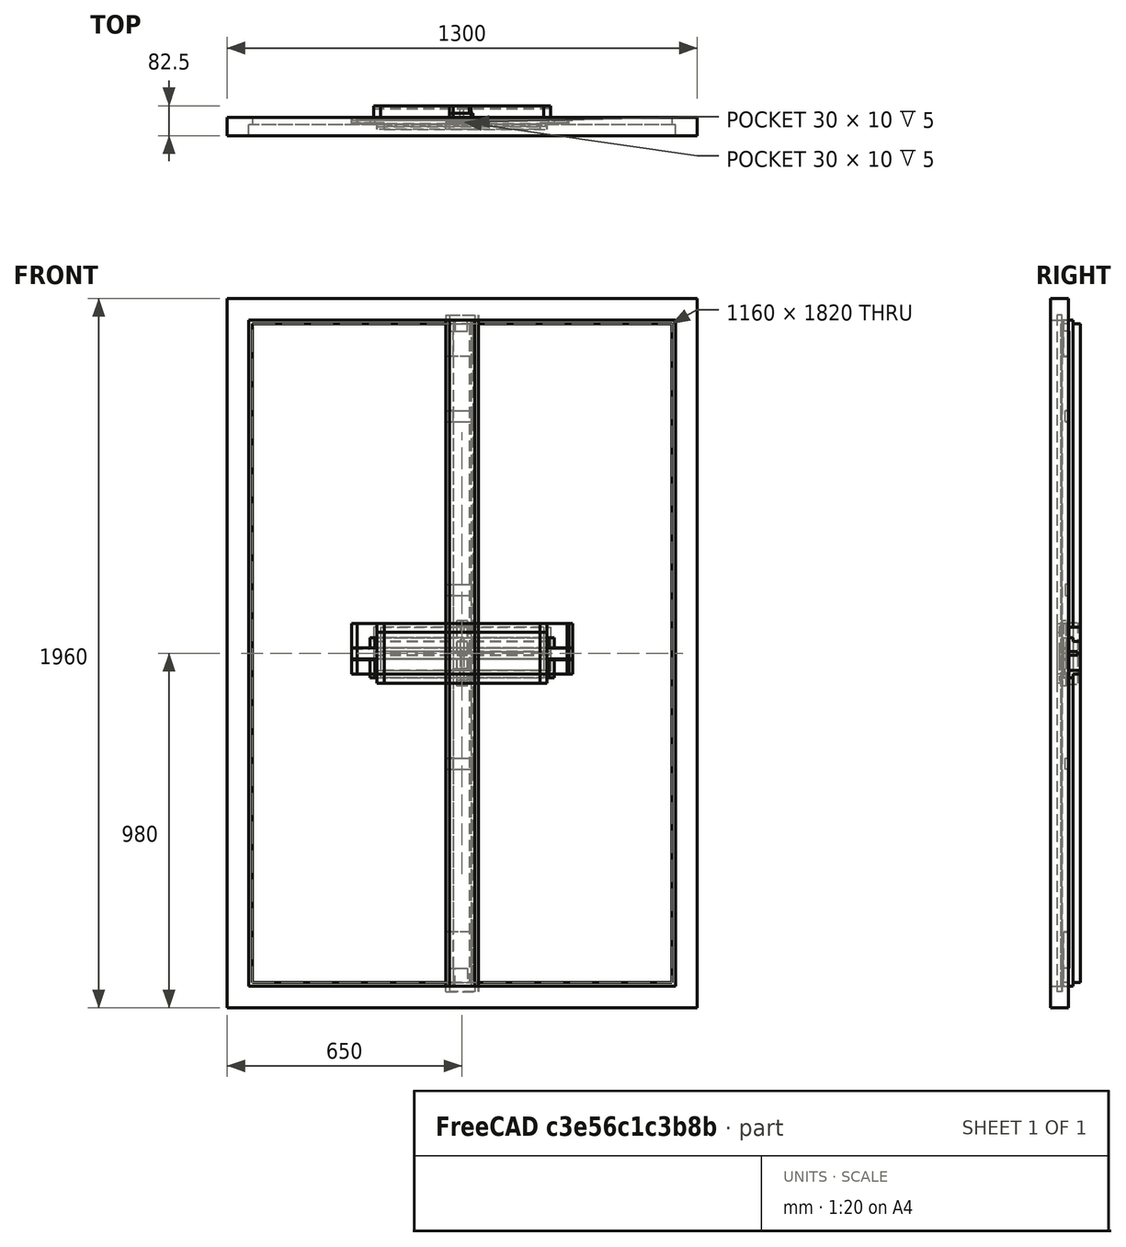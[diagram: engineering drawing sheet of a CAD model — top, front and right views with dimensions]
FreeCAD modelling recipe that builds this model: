
FCSTD DOCUMENT  (FreeCAD 1.1R38898 (Git))
Label: F4.0
License: All rights reserved
LicenseURL: https://en.wikipedia.org/wiki/All_rights_reserved
objects: Sketcher::SketchObject×54, PartDesign::Pocket×45, PartDesign::Plane×39, App::Link×27, App::FeaturePython×27, PartDesign::Body×14, PartDesign::Pad×7, PartDesign::FeatureBase×7, PartDesign::SubShapeBinder×6, Part::Mirroring×6, App::DocumentObjectGroup×6, PartDesign::Mirrored×5, App::VarSet×1, Assembly::JointGroup×1, Assembly::AssemblyObject×1
note: 353 computed .brp shape members not serialized (recipe doc carries the construction recipe); baked Part::Feature solids carry a one-line shape summary decoded from their .brp
EXTERNAL_REF file=F4.2.FCStd obj=Assembly
EXTERNAL_REF file=F4.1.FCStd obj=Assembly

FEATURE [App::VarSet] VarSet  label="Parameters"
  FrameThickness = 50
  GlassFullLength = 470
  GlassFullWidth = 470
  GlassLength = 470
  GlassOpeningHeigth = 450
  GlassOpeningWidth = 450
  GlassRebateDepth = 32
  GlassRebateWidth = 10
  GlassThickness = 24
  GlassThirdLength = 230
  GlassThirdWidth = 170
  GlassWidth = 470
  IntersectionRebateDepth = 10
  IntersectionRebateWidth = 32.5
  MuntinBarLength = 180
  MuntinBarTenonLength = 15
  MuntinTenonThickness = 10
  MuntinThickness = 50
  MuntinWidth = 30
  RailBottomTenonWidth = 100
  RailBottomWidth = 165
  RailLength = 610
  RailTenonThickness = 15
  RailTopTenonWidth = 70
  RailTopWidth = 115
  StileInnerHaunchDepth = 20
  StileInnerWidth = 70
  StileLength = 1870
  StileOuterHaunchDepth = 25
  StileOuterWidth = 90
  WindowFrameRebateDepth = 25
  WindowFrameRebateWidth = 20
  WindowInnerLipWidth = 15
  WindowThickness = 65
  expr: GlassFullLength = GlassOpeningHeigth + 2 * GlassRebateWidth
  expr: GlassFullWidth = GlassOpeningWidth + 2 * GlassRebateWidth
  expr: IntersectionRebateWidth = WindowThickness / 2
FEATURE [PartDesign::Plane] DatumPlane  label="DatumPlane top"
  AttachmentOffset = pos=(0,0,90) rot=(0,0,1;0rad)
  AttachmentSupport = -> [X_Axis]
  Length = 30
  MapMode = 2
  Placement = pos=(0,0,90) rot=(0,0,1;0rad)
  ResizeMode = 1
  Width = 50
  expr: .AttachmentOffset.Base.z = <<Parameters>>.MuntinBarLength / 2
  expr: Length = <<Parameters>>.MuntinWidth
  expr: Width = <<Parameters>>.MuntinThickness
FEATURE [PartDesign::Plane] DatumPlane001  label="DatumPlane right"
  AttachmentOffset = pos=(0,0,15) rot=(0,0,1;0rad)
  AttachmentSupport = -> [X_Axis]
  Length = 50
  MapMode = 4
  Placement = pos=(15,0,0) rot=(0.57735,0.57735,0.57735;2.0944rad)
  ResizeMode = 1
  Width = 180
  expr: .AttachmentOffset.Base.z = <<Parameters>>.MuntinWidth / 2
  expr: Length = <<Parameters>>.MuntinThickness
  expr: Width = <<Parameters>>.MuntinBarLength
FEATURE [PartDesign::Plane] DatumPlane002  label="DatumPlane front"
  AttachmentOffset = pos=(0,0,25) rot=(0,0,1;0rad)
  AttachmentSupport = -> [X_Axis]
  Length = 30
  MapMode = 3
  Placement = pos=(0,-25,5.6e-15) rot=(1,0,0;1.5708rad)
  ResizeMode = 1
  Width = 180
  expr: .AttachmentOffset.Base.z = <<Parameters>>.MuntinThickness / 2
  expr: Length = <<Parameters>>.MuntinWidth
  expr: Width = <<Parameters>>.MuntinBarLength
FEATURE [Sketcher::SketchObject] Sketch
  ArcFitTolerance = 0
  AttachmentSupport = -> [DatumPlane]
  FullyConstrained = true
  MakeInternals = false
  MapMode = 5
  Placement = pos=(0,0,90) rot=(0,0,1;0rad)
  expr: Constraints[10] = <<Parameters>>.MuntinWidth
  expr: Constraints[11] = <<Parameters>>.MuntinThickness
  sketch-geometry (5):
    g0: LineSegment StartX=-15 StartY=25 StartZ=0 EndX=-15 EndY=-25 EndZ=0
    g1: LineSegment StartX=-15 StartY=-25 StartZ=0 EndX=15 EndY=-25 EndZ=0
    g2: LineSegment StartX=15 StartY=-25 StartZ=0 EndX=15 EndY=25 EndZ=0
    g3: LineSegment StartX=15 StartY=25 StartZ=0 EndX=-15 EndY=25 EndZ=0
    g4: GeomPoint [constr] X=0 Y=0 Z=0
  constraints (12):
    c: Coincident(g0,g1)
    c: Coincident(g1,g2)
    c: Coincident(g2,g3)
    c: Coincident(g3,g0)
    c: Vertical(g0)
    c: Vertical(g2)
    c: Horizontal(g1)
    c: Horizontal(g3)
    c: Symmetric(g2,g0,g4)
    c: Coincident(g4,g-1)
    c: DistanceX(g3,g3) = 30
    c: DistanceY(g0,g0) = 50
FEATURE [PartDesign::Pad] Pad  label="Stock"
  Direction = (0,0,1)
  Length = 180
  Length2 = 10
  Placement = pos=(0,0,90) rot=(0,0,1;0rad)
  Profile = -> Sketch
  ReferenceAxis = -> Sketch [N_Axis]
  Refine = true
  Reversed = true
  Suppressed = false
  Type = 0
  expr: Length = <<Parameters>>.MuntinBarLength
FEATURE [Sketcher::SketchObject] Sketch001
  ArcFitTolerance = 0
  AttachmentSupport = -> [DatumPlane001]
  ExternalGeometry = -> [DatumPlane,DatumPlane002]
  FullyConstrained = true
  MakeInternals = false
  MapMode = 5
  Placement = pos=(15,0,0) rot=(0.57735,0.57735,0.57735;2.0944rad)
  expr: Constraints[14] = <<Parameters>>.MuntinBarTenonLength
  expr: Constraints[16] = <<Parameters>>.GlassRebateDepth
  expr: Constraints[18] = <<Parameters>>.MuntinThickness
  expr: Constraints[19] = <<Parameters>>.MuntinTenonThickness
  expr: Constraints[20] = <<Parameters>>.MuntinBarTenonLength - <<Parameters>>.GlassRebateWidth
  sketch-geometry (8):
    g0: LineSegment StartX=-17 StartY=90 StartZ=0 EndX=-17 EndY=75 EndZ=0
    g1: LineSegment StartX=-17 StartY=75 StartZ=0 EndX=-25 EndY=75 EndZ=0
    g2: LineSegment StartX=-25 StartY=75 StartZ=0 EndX=-25 EndY=90 EndZ=0
    g3: LineSegment StartX=-25 StartY=90 StartZ=0 EndX=-17 EndY=90 EndZ=0
    g4: LineSegment StartX=-7 StartY=90 StartZ=0 EndX=-7 EndY=85 EndZ=0
    g5: LineSegment StartX=-7 StartY=85 StartZ=0 EndX=25 EndY=85 EndZ=0
    g6: LineSegment StartX=25 StartY=85 StartZ=0 EndX=25 EndY=90 EndZ=0
    g7: LineSegment StartX=25 StartY=90 StartZ=0 EndX=-7 EndY=90 EndZ=0
  constraints (23):
    c: Coincident(g0,g1)
    c: Coincident(g1,g2)
    c: Coincident(g2,g3)
    c: Coincident(g3,g0)
    c: Vertical(g0)
    c: Horizontal(g1)
    c: Coincident(g4,g5)
    c: Coincident(g5,g6)
    c: Coincident(g6,g7)
    c: Coincident(g7,g4)
    c: Vertical(g4)
    c: Vertical(g6)
    c: Horizontal(g5)
    c: Horizontal(g7)
    c: DistanceY(g0,g0) = 15
    c: DistanceX(g1,g1) = -8
    c: DistanceX(g7,g7) = 32
    c: Horizontal(g4,g2)
    c: DistanceX(g2,g6) = 50
    c: DistanceX(g0,g4) = 10
    c: DistanceY(g6,g6) = 5
    c: Tangent(g2,g-4)
    c: Tangent(g3,g-3)
FEATURE [PartDesign::Pocket] Pocket  label="Tenon top"
  BaseFeature = -> Pad
  Direction = (-1,0,0)
  Length = 5
  Length2 = 5
  Placement = pos=(0,0,90) rot=(0,0,1;0rad)
  Profile = -> Sketch001
  ReferenceAxis = -> Sketch001 [N_Axis]
  Refine = true
  Suppressed = false
  Type = 1
FEATURE [PartDesign::Mirrored] Mirrored  label="Tenon bottom"
  BaseFeature = -> Pocket
  MirrorPlane = -> XY_Plane
  Originals = -> [Pocket]
  Placement = pos=(0,0,90) rot=(0,0,1;0rad)
  Refine = true
  Suppressed = false
  TransformMode = 0
FEATURE [Sketcher::SketchObject] Sketch002
  ArcFitTolerance = 0
  AttachmentSupport = -> [DatumPlane]
  ExternalGeometry = -> [DatumPlane001,DatumPlane002]
  FullyConstrained = true
  MakeInternals = false
  MapMode = 5
  Placement = pos=(0,0,90) rot=(0,0,1;0rad)
  expr: Constraints[7] = <<Parameters>>.GlassRebateDepth
  expr: Constraints[8] = <<Parameters>>.GlassRebateWidth
  expr: Constraints[9] = <<Parameters>>.MuntinThickness
  sketch-geometry (4):
    g0: LineSegment StartX=5 StartY=25 StartZ=0 EndX=5 EndY=-7 EndZ=0
    g1: LineSegment StartX=5 StartY=-7 StartZ=0 EndX=15 EndY=-7 EndZ=0
    g2: LineSegment StartX=15 StartY=-7 StartZ=0 EndX=15 EndY=25 EndZ=0
    g3: LineSegment StartX=15 StartY=25 StartZ=0 EndX=5 EndY=25 EndZ=0
  constraints (11):
    c: Coincident(g0,g1)
    c: Coincident(g1,g2)
    c: Coincident(g2,g3)
    c: Coincident(g3,g0)
    c: Vertical(g0)
    c: Horizontal(g1)
    c: Horizontal(g3)
    c: DistanceY(g0,g0) = 32
    c: DistanceX(g3,g3) = 10
    c: Distance(g2,g-4) = 50
    c: Tangent(g2,g-3)
FEATURE [PartDesign::Pocket] Pocket001  label="Glass rebate right"
  BaseFeature = -> Mirrored
  Direction = (0,0,-1)
  Length = 5
  Length2 = 5
  Placement = pos=(0,0,90) rot=(0,0,1;0rad)
  Profile = -> Sketch002
  ReferenceAxis = -> Sketch002 [N_Axis]
  Refine = true
  Suppressed = false
  Type = 1
FEATURE [PartDesign::Mirrored] Mirrored001  label="Glass rebate left"
  BaseFeature = -> Pocket001
  MirrorPlane = -> Sketch002 [V_Axis]
  Originals = -> [Pocket001]
  Placement = pos=(0,0,90) rot=(0,0,1;0rad)
  Refine = true
  Suppressed = false
  TransformMode = 0
FEATURE [PartDesign::Body] Body  label="Muntin bar"
  AllowCompound = false
  Group = -> [DatumPlane,DatumPlane001,DatumPlane002,Sketch,Pad,Sketch001,Pocket,Mirrored,Sketch002,Pocket001,Mirrored001]
  Origin = -> Origin
  Tip = -> Mirrored001
FEATURE [PartDesign::Plane] DatumPlane003  label="DatumPlane top001"
  AttachmentOffset = pos=(0,0,935) rot=(0,0,1;0rad)
  AttachmentSupport = -> [X_Axis001]
  Length = 90
  MapMode = 2
  Placement = pos=(0,0,935) rot=(0,0,1;0rad)
  ResizeMode = 1
  Width = 65
  expr: .AttachmentOffset.Base.z = <<Parameters>>.StileLength / 2
  expr: Length = <<Parameters>>.StileOuterWidth
  expr: Width = <<Parameters>>.WindowThickness
FEATURE [PartDesign::Plane] DatumPlane004  label="DatumPlane right001"
  AttachmentOffset = pos=(0,0,45) rot=(0,0,1;0rad)
  AttachmentSupport = -> [X_Axis001]
  Length = 65
  MapMode = 4
  Placement = pos=(45,0,0) rot=(0.57735,0.57735,0.57735;2.0944rad)
  ResizeMode = 1
  Width = 1870
  expr: .AttachmentOffset.Base.z = <<Parameters>>.StileOuterWidth / 2
  expr: Length = <<Parameters>>.WindowThickness
  expr: Width = <<Parameters>>.StileLength
FEATURE [PartDesign::Plane] DatumPlane005  label="DatumPlane rear"
  AttachmentOffset = pos=(0,0,32.5) rot=(0,0,1;0rad)
  AttachmentSupport = -> [X_Axis001]
  Length = 90
  MapMode = 3
  Placement = pos=(0,32.5,-7.2e-15) rot=(0,0.707107,0.707107;3.14159rad)
  ResizeMode = 1
  Width = 1870
  expr: .AttachmentOffset.Base.z = <<Parameters>>.WindowThickness / 2
  expr: Length = <<Parameters>>.StileOuterWidth
  expr: Width = <<Parameters>>.StileLength
FEATURE [Sketcher::SketchObject] Sketch003
  ArcFitTolerance = 0
  AttachmentSupport = -> [DatumPlane003]
  FullyConstrained = true
  MakeInternals = false
  MapMode = 5
  Placement = pos=(0,0,935) rot=(0,0,1;0rad)
  expr: Constraints[10] = <<Parameters>>.StileOuterWidth
  expr: Constraints[11] = <<Parameters>>.WindowThickness
  sketch-geometry (5):
    g0: LineSegment StartX=-45 StartY=32.5 StartZ=0 EndX=-45 EndY=-32.5 EndZ=0
    g1: LineSegment StartX=-45 StartY=-32.5 StartZ=0 EndX=45 EndY=-32.5 EndZ=0
    g2: LineSegment StartX=45 StartY=-32.5 StartZ=0 EndX=45 EndY=32.5 EndZ=0
    g3: LineSegment StartX=45 StartY=32.5 StartZ=0 EndX=-45 EndY=32.5 EndZ=0
    g4: GeomPoint [constr] X=0 Y=0 Z=0
  constraints (12):
    c: Coincident(g0,g1)
    c: Coincident(g1,g2)
    c: Coincident(g2,g3)
    c: Coincident(g3,g0)
    c: Vertical(g0)
    c: Vertical(g2)
    c: Horizontal(g1)
    c: Horizontal(g3)
    c: Symmetric(g2,g0,g4)
    c: Coincident(g4,g-1)
    c: DistanceX(g3,g3) = 90
    c: DistanceY(g0,g0) = 65
FEATURE [PartDesign::Pad] Pad001  label="Stock001"
  Direction = (0,0,1)
  Length = 1870
  Length2 = 10
  Placement = pos=(0,0,935) rot=(0,0,1;0rad)
  Profile = -> Sketch003
  ReferenceAxis = -> Sketch003 [N_Axis]
  Refine = true
  Reversed = true
  Suppressed = false
  Type = 0
  expr: Length = <<Parameters>>.StileLength
FEATURE [PartDesign::Plane] DatumPlane006  label="DatumPlane bottom"
  AttachmentOffset = pos=(0,0,935) rot=(0,0,1;0rad)
  AttachmentSupport = -> [X_Axis001]
  Length = 90
  MapMode = 2
  Placement = pos=(0,0,-935) rot=(0,1,0;3.14159rad)
  ResizeMode = 1
  Width = 65
  expr: .AttachmentOffset.Base.z = <<Parameters>>.StileLength / 2
  expr: Length = <<Parameters>>.StileOuterWidth
  expr: Width = <<Parameters>>.WindowThickness
FEATURE [Sketcher::SketchObject] Sketch006
  ArcFitTolerance = 0
  AttachmentSupport = -> [DatumPlane004]
  ExternalGeometry = -> [DatumPlane005,DatumPlane006]
  FullyConstrained = true
  MakeInternals = false
  MapMode = 5
  Placement = pos=(45,0,0) rot=(0.57735,0.57735,0.57735;2.0944rad)
  expr: Constraints[30] = <<Parameters>>.GlassOpeningHeigth
  expr: Constraints[31] = <<Parameters>>.MuntinTenonThickness
  expr: Constraints[32] = <<Parameters>>.GlassRebateDepth
  expr: Constraints[34] = <<Parameters>>.GlassOpeningHeigth + <<Parameters>>.RailBottomWidth
  expr: Constraints[35] = <<Parameters>>.GlassOpeningHeigth
  expr: Constraints[8] = <<Parameters>>.MuntinWidth
  sketch-geometry (12):
    g0: LineSegment StartX=-9.5 StartY=-290 StartZ=0 EndX=-9.5 EndY=-320 EndZ=0
    g1: LineSegment StartX=-9.5 StartY=-320 StartZ=0 EndX=0.5 EndY=-320 EndZ=0
    g2: LineSegment StartX=0.5 StartY=-320 StartZ=0 EndX=0.5 EndY=-290 EndZ=0
    g3: LineSegment StartX=0.5 StartY=-290 StartZ=0 EndX=-9.5 EndY=-290 EndZ=0
    g4: LineSegment StartX=-9.5 StartY=160 StartZ=0 EndX=-9.5 EndY=190 EndZ=0
    g5: LineSegment StartX=-9.5 StartY=190 StartZ=0 EndX=0.5 EndY=190 EndZ=0
    g6: LineSegment StartX=0.5 StartY=190 StartZ=0 EndX=0.5 EndY=160 EndZ=0
    g7: LineSegment StartX=0.5 StartY=160 StartZ=0 EndX=-9.5 EndY=160 EndZ=0
    g8: LineSegment StartX=-9.5 StartY=640 StartZ=0 EndX=-9.5 EndY=670 EndZ=0
    g9: LineSegment StartX=-9.5 StartY=670 StartZ=0 EndX=0.5 EndY=670 EndZ=0
    g10: LineSegment StartX=0.5 StartY=670 StartZ=0 EndX=0.5 EndY=640 EndZ=0
    g11: LineSegment StartX=0.5 StartY=640 StartZ=0 EndX=-9.5 EndY=640 EndZ=0
  constraints (36):
    c: Coincident(g0,g1)
    c: Coincident(g1,g2)
    c: Coincident(g2,g3)
    c: Coincident(g3,g0)
    c: Vertical(g0)
    c: Vertical(g2)
    c: Horizontal(g1)
    c: Horizontal(g3)
    c: DistanceY(g0,g0) = 30
    c: Coincident(g4,g5)
    c: Coincident(g8,g9)
    c: Coincident(g5,g6)
    c: Coincident(g9,g10)
    c: Coincident(g6,g7)
    c: Coincident(g10,g11)
    c: Coincident(g7,g4)
    c: Coincident(g11,g8)
    c: Vertical(g4)
    c: Vertical(g8)
    c: Vertical(g6)
    c: Vertical(g10)
    c: Horizontal(g5)
    c: Horizontal(g9)
    c: Horizontal(g7)
    c: Horizontal(g11)
    c: Equal(g0,g4)
    c: Equal(g0,g8)
    c: Equal(g11,g7)
    c: Equal(g7,g3)
    c: Vertical(g5,g9)
    c: DistanceY(g0,g4) = 450
    c: DistanceX(g1,g1) = 10
    c: Distance(g1,g-3) = 32
    c: Vertical(g9,g2)
    c: Distance(g0,g-4) = 615
    c: DistanceY(g4,g8) = 450
FEATURE [Sketcher::SketchObject] Sketch007  label="Frame rebate opening top002"
  ArcFitTolerance = 0
  AttachmentSupport = -> [DatumPlane004]
  ExternalGeometry = -> [DatumPlane003,DatumPlane005]
  FullyConstrained = true
  MakeInternals = false
  MapMode = 5
  Placement = pos=(45,0,0) rot=(0.57735,0.57735,0.57735;2.0944rad)
  expr: Constraints[6] = <<Parameters>>.WindowFrameRebateWidth
  expr: Constraints[7] = <<Parameters>>.WindowFrameRebateDepth
  sketch-geometry (4):
    g0: LineSegment StartX=12.5 StartY=935 StartZ=0 EndX=12.5 EndY=910 EndZ=0
    g1: LineSegment StartX=12.5 StartY=910 StartZ=0 EndX=32.5 EndY=910 EndZ=0
    g2: LineSegment StartX=32.5 StartY=910 StartZ=0 EndX=32.5 EndY=935 EndZ=0
    g3: LineSegment StartX=32.5 StartY=935 StartZ=0 EndX=12.5 EndY=935 EndZ=0
  constraints (10):
    c: Coincident(g0,g1)
    c: Coincident(g1,g2)
    c: Coincident(g2,g3)
    c: Coincident(g3,g0)
    c: Vertical(g0)
    c: Horizontal(g1)
    c: DistanceX(g3,g3) = 20
    c: Distance(g2,g2) = 25
    c: Tangent(g2,g-4)
    c: Tangent(g3,g-3)
FEATURE [Sketcher::SketchObject] Sketch008  label="Frame rebate closure top002"
  ArcFitTolerance = 0
  AttachmentSupport = -> [DatumPlane004]
  ExternalGeometry = -> [DatumPlane003,DatumPlane005]
  FullyConstrained = true
  MakeInternals = false
  MapMode = 5
  Placement = pos=(45,0,0) rot=(0.57735,0.57735,0.57735;2.0944rad)
  expr: Constraints[6] = <<Parameters>>.WindowInnerLipWidth
  expr: Constraints[7] = <<Parameters>>.FrameThickness
  sketch-geometry (4):
    g0: LineSegment StartX=-17.5 StartY=935 StartZ=0 EndX=-17.5 EndY=920 EndZ=0
    g1: LineSegment StartX=-17.5 StartY=920 StartZ=0 EndX=32.5 EndY=920 EndZ=0
    g2: LineSegment StartX=32.5 StartY=920 StartZ=0 EndX=32.5 EndY=935 EndZ=0
    g3: LineSegment StartX=32.5 StartY=935 StartZ=0 EndX=-17.5 EndY=935 EndZ=0
  constraints (10):
    c: Coincident(g0,g1)
    c: Coincident(g1,g2)
    c: Coincident(g2,g3)
    c: Coincident(g3,g0)
    c: Vertical(g0)
    c: Horizontal(g1)
    c: DistanceY(g2,g2) = 15
    c: DistanceX(g3,g3) = 50
    c: Tangent(g3,g-3)
    c: Tangent(g-4,g2)
FEATURE [PartDesign::Plane] DatumPlane007  label="DatumPlane left"
  AttachmentOffset = pos=(0,0,45) rot=(0,0,1;0rad)
  AttachmentSupport = -> [X_Axis001]
  Length = 65
  MapMode = 4
  Placement = pos=(-45,0,0) rot=(0.57735,-0.57735,-0.57735;2.0944rad)
  ResizeMode = 1
  Width = 1870
  expr: .AttachmentOffset.Base.z = <<Parameters>>.StileOuterWidth / 2
  expr: Length = <<Parameters>>.WindowThickness
  expr: Width = <<Parameters>>.StileLength
FEATURE [Sketcher::SketchObject] Sketch009  label="Frame rebate opening side002"
  ArcFitTolerance = 0
  AttachmentSupport = -> [DatumPlane003]
  ExternalGeometry = -> [DatumPlane005,DatumPlane007]
  FullyConstrained = true
  MakeInternals = false
  MapMode = 5
  Placement = pos=(0,0,935) rot=(0,0,1;0rad)
  expr: Constraints[6] = <<Parameters>>.WindowFrameRebateDepth
  expr: Constraints[7] = <<Parameters>>.WindowFrameRebateWidth
  sketch-geometry (4):
    g0: LineSegment StartX=-45 StartY=32.5 StartZ=0 EndX=-45 EndY=12.5 EndZ=0
    g1: LineSegment StartX=-45 StartY=12.5 StartZ=0 EndX=-20 EndY=12.5 EndZ=0
    g2: LineSegment StartX=-20 StartY=12.5 StartZ=0 EndX=-20 EndY=32.5 EndZ=0
    g3: LineSegment StartX=-20 StartY=32.5 StartZ=0 EndX=-45 EndY=32.5 EndZ=0
  constraints (10):
    c: Coincident(g0,g1)
    c: Coincident(g1,g2)
    c: Coincident(g2,g3)
    c: Coincident(g3,g0)
    c: Vertical(g2)
    c: Horizontal(g1)
    c: DistanceX(g3,g3) = 25
    c: DistanceY(g0,g0) = 20
    c: Tangent(g3,g-3)
    c: Tangent(g0,g-4)
FEATURE [Sketcher::SketchObject] Sketch010  label="Frame rebate closure right002"
  ArcFitTolerance = 0
  AttachmentSupport = -> [DatumPlane003]
  ExternalGeometry = -> [DatumPlane005,DatumPlane007]
  FullyConstrained = true
  MakeInternals = false
  MapMode = 5
  Placement = pos=(0,0,935) rot=(0,0,1;0rad)
  expr: Constraints[6] = <<Parameters>>.WindowInnerLipWidth
  expr: Constraints[7] = <<Parameters>>.FrameThickness
  sketch-geometry (4):
    g0: LineSegment StartX=-45 StartY=32.5 StartZ=0 EndX=-45 EndY=-17.5 EndZ=0
    g1: LineSegment StartX=-45 StartY=-17.5 StartZ=0 EndX=-30 EndY=-17.5 EndZ=0
    g2: LineSegment StartX=-30 StartY=-17.5 StartZ=0 EndX=-30 EndY=32.5 EndZ=0
    g3: LineSegment StartX=-30 StartY=32.5 StartZ=0 EndX=-45 EndY=32.5 EndZ=0
  constraints (10):
    c: Coincident(g0,g1)
    c: Coincident(g1,g2)
    c: Coincident(g2,g3)
    c: Coincident(g3,g0)
    c: Vertical(g2)
    c: Horizontal(g1)
    c: DistanceX(g3,g3) = 15
    c: DistanceY(g0,g0) = 50
    c: Tangent(g3,g-3)
    c: Tangent(g0,g-4)
FEATURE [PartDesign::SubShapeBinder] Binder  label="Stile outer left binder"
  BindCopyOnChange = 0
  BindMode = 0
  ClaimChildren = false
  Context = -> Body001 [Binder.]
  Fuse = false
  MakeFace = true
  OffsetFill = false
  OffsetIntersection = false
  OffsetJoinType = 0
  OffsetOpenResult = false
  PartialLoad = false
  Refine = true
  Relative = true
  Support = -> [Body001[Pocket017.]]
  _Version = 2
FEATURE [Part::Mirroring] Part__Mirroring  label="Stile outer right (Mirror #1)"
  Base = (0,0,0)
  Normal = (1,0,0)
  Source = -> Binder
FEATURE [PartDesign::FeatureBase] BaseFeature
  BaseFeature = -> Part__Mirroring
  Suppressed = false
FEATURE [PartDesign::Body] Body002  label="Stile outer right"
  AllowCompound = false
  BaseFeature = -> Part__Mirroring
  Group = -> [BaseFeature]
  Origin = -> Origin002
  Tip = -> BaseFeature
FEATURE [Sketcher::SketchObject] Sketch019  label="Mortise rail top002"
  ArcFitTolerance = 0
  AttachmentOffset = pos=(0,0,-32) rot=(0,0,1;0rad)
  AttachmentSupport = -> [DatumPlane005]
  ExternalGeometry = -> [DatumPlane007,DatumPlane003]
  FullyConstrained = true
  MakeInternals = false
  MapMode = 5
  Placement = pos=(0,0.5,-1e-16) rot=(0,0.707107,0.707107;3.14159rad)
  expr: .AttachmentOffset.Base.z = -<<Parameters>>.GlassRebateDepth
  expr: Constraints[10] = <<Parameters>>.StileOuterWidth
  expr: Constraints[11] = <<Parameters>>.RailTopTenonWidth
  expr: Constraints[12] = <<Parameters>>.RailTopWidth
  expr: Constraints[13] = <<Parameters>>.StileOuterHaunchDepth
  sketch-geometry (6):
    g0: LineSegment StartX=-45 StartY=935 StartZ=0 EndX=-20 EndY=935 EndZ=0
    g1: LineSegment StartX=-20 StartY=935 StartZ=0 EndX=-20 EndY=890 EndZ=0
    g2: LineSegment StartX=-20 StartY=890 StartZ=0 EndX=45 EndY=890 EndZ=0
    g3: LineSegment StartX=45 StartY=890 StartZ=0 EndX=45 EndY=820 EndZ=0
    g4: LineSegment StartX=45 StartY=820 StartZ=0 EndX=-45 EndY=820 EndZ=0
    g5: LineSegment StartX=-45 StartY=820 StartZ=0 EndX=-45 EndY=935 EndZ=0
  constraints (16):
    c: Coincident(g0,g1)
    c: Vertical(g1)
    c: Coincident(g1,g2)
    c: Horizontal(g2)
    c: Coincident(g2,g3)
    c: Coincident(g3,g4)
    c: Horizontal(g4)
    c: Coincident(g4,g5)
    c: Coincident(g5,g0)
    c: Vertical(g5)
    c: DistanceX(g4,g4) = 90
    c: DistanceY(g3,g3) = 70
    c: DistanceY(g5,g5) = 115
    c: DistanceX(g0,g0) = 25
    c: Tangent(g-3,g3)
    c: Tangent(g0,g-4)
FEATURE [PartDesign::Pocket] Pocket016  label="Mortise rail top003"
  BaseFeature = -> Pad001
  Direction = (0,-1,2e-16)
  Length = 15
  Length2 = 5
  Placement = pos=(0,0,935) rot=(0,0,1;0rad)
  Profile = -> Sketch019
  ReferenceAxis = -> Sketch019 [N_Axis]
  Refine = true
  Suppressed = false
  Type = 0
  expr: Length = <<Parameters>>.RailTenonThickness
FEATURE [Sketcher::SketchObject] Sketch020
  ArcFitTolerance = 0
  AttachmentSupport = -> [DatumPlane003]
  ExternalGeometry = -> [DatumPlane005,DatumPlane004]
  FullyConstrained = true
  MakeInternals = false
  MapMode = 5
  Placement = pos=(0,0,935) rot=(0,0,1;0rad)
  expr: Constraints[6] = <<Parameters>>.GlassRebateDepth
  expr: Constraints[7] = <<Parameters>>.GlassRebateWidth
  sketch-geometry (4):
    g0: LineSegment StartX=35 StartY=32.5 StartZ=0 EndX=35 EndY=0.5 EndZ=0
    g1: LineSegment StartX=35 StartY=0.5 StartZ=0 EndX=45 EndY=0.5 EndZ=0
    g2: LineSegment StartX=45 StartY=0.5 StartZ=0 EndX=45 EndY=32.5 EndZ=0
    g3: LineSegment StartX=45 StartY=32.5 StartZ=0 EndX=35 EndY=32.5 EndZ=0
  constraints (10):
    c: Coincident(g0,g1)
    c: Coincident(g1,g2)
    c: Coincident(g2,g3)
    c: Coincident(g3,g0)
    c: Vertical(g0)
    c: Horizontal(g1)
    c: DistanceY(g2,g2) = 32
    c: DistanceX(g3,g3) = 10
    c: Tangent(g3,g-3)
    c: Tangent(g2,g-4)
FEATURE [Sketcher::SketchObject] Sketch021
  ArcFitTolerance = 0
  AttachmentOffset = pos=(0,0,-32) rot=(0,0,1;0rad)
  AttachmentSupport = -> [DatumPlane005]
  ExternalGeometry = -> [DatumPlane006,DatumPlane004]
  FullyConstrained = true
  MakeInternals = false
  MapMode = 5
  Placement = pos=(0,0.5,-1e-16) rot=(0,0.707107,0.707107;3.14159rad)
  expr: .AttachmentOffset.Base.z = -<<Parameters>>.GlassRebateDepth
  expr: Constraints[10] = <<Parameters>>.StileOuterWidth
  expr: Constraints[11] = <<Parameters>>.RailBottomTenonWidth
  expr: Constraints[12] = <<Parameters>>.RailBottomWidth
  expr: Constraints[13] = <<Parameters>>.StileOuterHaunchDepth
  sketch-geometry (6):
    g0: LineSegment StartX=45 StartY=-770 StartZ=0 EndX=-45 EndY=-770 EndZ=0
    g1: LineSegment StartX=-45 StartY=-770 StartZ=0 EndX=-45 EndY=-935 EndZ=0
    g2: LineSegment StartX=-45 StartY=-935 StartZ=0 EndX=-20 EndY=-935 EndZ=0
    g3: LineSegment StartX=-20 StartY=-935 StartZ=0 EndX=-20 EndY=-870 EndZ=0
    g4: LineSegment StartX=-20 StartY=-870 StartZ=0 EndX=45 EndY=-870 EndZ=0
    g5: LineSegment StartX=45 StartY=-870 StartZ=0 EndX=45 EndY=-770 EndZ=0
  constraints (16):
    c: Horizontal(g0)
    c: Coincident(g0,g1)
    c: Coincident(g1,g2)
    c: Coincident(g2,g3)
    c: Vertical(g3)
    c: Coincident(g3,g4)
    c: Horizontal(g4)
    c: Coincident(g4,g5)
    c: Coincident(g5,g0)
    c: Vertical(g5)
    c: DistanceX(g0,g0) = 90
    c: DistanceY(g5,g5) = 100
    c: DistanceY(g1,g1) = 165
    c: DistanceX(g2,g2) = 25
    c: Tangent(g2,g-3)
    c: Tangent(g1,g-4)
FEATURE [PartDesign::Pocket] Pocket018  label="Mortise rail bottom002"
  BaseFeature = -> Pocket016
  Direction = (0,-1,2e-16)
  Length = 15
  Length2 = 5
  Placement = pos=(0,0,935) rot=(0,0,1;0rad)
  Profile = -> Sketch021
  ReferenceAxis = -> Sketch021 [N_Axis]
  Refine = true
  Suppressed = false
  Type = 0
  expr: Length = <<Parameters>>.RailTenonThickness
FEATURE [PartDesign::Pocket] Pocket004  label="Mortises muntin"
  BaseFeature = -> Pocket018
  Direction = (-1,0,0)
  Length = 5
  Length2 = 5
  Placement = pos=(0,0,935) rot=(0,0,1;0rad)
  Profile = -> Sketch006
  ReferenceAxis = -> Sketch006 [N_Axis]
  Refine = true
  Suppressed = false
  Type = 1
FEATURE [PartDesign::Pocket] Pocket005  label="Frame rebate opening top"
  BaseFeature = -> Pocket004
  Direction = (-1,0,0)
  Length = 5
  Length2 = 5
  Placement = pos=(0,0,935) rot=(0,0,1;0rad)
  Profile = -> Sketch007
  ReferenceAxis = -> Sketch007 [N_Axis]
  Refine = true
  Suppressed = false
  Type = 1
FEATURE [PartDesign::Pocket] Pocket006  label="Frame rebate lip top"
  BaseFeature = -> Pocket005
  Direction = (-1,0,0)
  Length = 5
  Length2 = 5
  Placement = pos=(0,0,935) rot=(0,0,1;0rad)
  Profile = -> Sketch008
  ReferenceAxis = -> Sketch008 [N_Axis]
  Refine = true
  Suppressed = false
  Type = 1
FEATURE [PartDesign::Mirrored] Mirrored002  label="Frame rebates bottom"
  BaseFeature = -> Pocket006
  MirrorPlane = -> XY_Plane001
  Originals = -> [Pocket005,Pocket006]
  Placement = pos=(0,0,935) rot=(0,0,1;0rad)
  Refine = true
  Suppressed = false
  TransformMode = 0
FEATURE [PartDesign::Pocket] Pocket007  label="Frame rebate opening left"
  BaseFeature = -> Mirrored002
  Direction = (0,0,-1)
  Length = 5
  Length2 = 5
  Placement = pos=(0,0,935) rot=(0,0,1;0rad)
  Profile = -> Sketch009
  ReferenceAxis = -> Sketch009 [N_Axis]
  Refine = true
  Suppressed = false
  Type = 1
FEATURE [PartDesign::Pocket] Pocket008  label="Frame rebate lip left001"
  BaseFeature = -> Pocket007
  Direction = (0,0,-1)
  Length = 5
  Length2 = 5
  Placement = pos=(0,0,935) rot=(0,0,1;0rad)
  Profile = -> Sketch010
  ReferenceAxis = -> Sketch010 [N_Axis]
  Refine = true
  Suppressed = false
  Type = 1
FEATURE [PartDesign::Pocket] Pocket017  label="Glass rebate"
  BaseFeature = -> Pocket008
  Direction = (0,0,-1)
  Length = 5
  Length2 = 5
  Placement = pos=(0,0,935) rot=(0,0,1;0rad)
  Profile = -> Sketch020
  ReferenceAxis = -> Sketch020 [N_Axis]
  Refine = true
  Suppressed = false
  Type = 1
FEATURE [PartDesign::Body] Body001  label="Stile outer left"
  AllowCompound = false
  Group = -> [DatumPlane003,DatumPlane004,DatumPlane005,DatumPlane006,DatumPlane007,Sketch003,Pad001,Pocket016,Pocket018,Sketch006,Pocket004,Sketch007,Pocket005,Sketch008,Pocket006,Mirrored002,Sketch009,Sketch010,Pocket007,Pocket008,Sketch019,Sketch020,Pocket017,Sketch021]
  Origin = -> Origin001
  Tip = -> Pocket017
FEATURE [PartDesign::Plane] DatumPlane008  label="DatumPlane top002"
  AttachmentOffset = pos=(0,0,935) rot=(0,0,1;0rad)
  AttachmentSupport = -> [X_Axis003]
  Length = 70
  MapMode = 2
  Placement = pos=(0,0,935) rot=(0,0,1;0rad)
  ResizeMode = 1
  Width = 65
  expr: .AttachmentOffset.Base.z = <<Parameters>>.StileLength / 2
  expr: Length = <<Parameters>>.StileInnerWidth
  expr: Width = <<Parameters>>.WindowThickness
FEATURE [PartDesign::Plane] DatumPlane009  label="DatumPlane right002"
  AttachmentOffset = pos=(0,0,35) rot=(0,0,1;0rad)
  AttachmentSupport = -> [X_Axis003]
  Length = 65
  MapMode = 4
  Placement = pos=(35,0,0) rot=(0.57735,0.57735,0.57735;2.0944rad)
  ResizeMode = 1
  Width = 1870
  expr: .AttachmentOffset.Base.z = <<Parameters>>.StileInnerWidth / 2
  expr: Length = <<Parameters>>.WindowThickness
  expr: Width = <<Parameters>>.StileLength
FEATURE [PartDesign::Plane] DatumPlane010  label="DatumPlane rear001"
  AttachmentOffset = pos=(0,0,32.5) rot=(0,0,1;0rad)
  AttachmentSupport = -> [X_Axis003]
  Length = 70
  MapMode = 3
  Placement = pos=(0,32.5,-7.2e-15) rot=(0,0.707107,0.707107;3.14159rad)
  ResizeMode = 1
  Width = 1870
  expr: .AttachmentOffset.Base.z = <<Parameters>>.WindowThickness / 2
  expr: Length = <<Parameters>>.StileInnerWidth
  expr: Width = <<Parameters>>.StileLength
FEATURE [PartDesign::Plane] DatumPlane011  label="DatumPlane bottom001"
  AttachmentOffset = pos=(0,0,935) rot=(0,0,1;0rad)
  AttachmentSupport = -> [X_Axis003]
  Length = 70
  MapMode = 2
  Placement = pos=(0,0,-935) rot=(0,1,0;3.14159rad)
  ResizeMode = 1
  Width = 65
  expr: .AttachmentOffset.Base.z = <<Parameters>>.StileLength / 2
  expr: Length = <<Parameters>>.StileInnerWidth
  expr: Width = <<Parameters>>.WindowThickness
FEATURE [PartDesign::Plane] DatumPlane012  label="DatumPlane left001"
  AttachmentOffset = pos=(0,0,35) rot=(0,0,1;0rad)
  AttachmentSupport = -> [X_Axis003]
  Length = 65
  MapMode = 4
  Placement = pos=(-35,0,0) rot=(0.57735,-0.57735,-0.57735;2.0944rad)
  ResizeMode = 1
  Width = 1870
  expr: .AttachmentOffset.Base.z = <<Parameters>>.StileInnerWidth / 2
  expr: Length = <<Parameters>>.WindowThickness
  expr: Width = <<Parameters>>.StileLength
FEATURE [Sketcher::SketchObject] Sketch022
  ArcFitTolerance = 0
  AttachmentSupport = -> [DatumPlane008]
  FullyConstrained = true
  MakeInternals = false
  MapMode = 5
  Placement = pos=(0,0,935) rot=(0,0,1;0rad)
  expr: Constraints[10] = <<Parameters>>.StileInnerWidth
  expr: Constraints[11] = <<Parameters>>.WindowThickness
  sketch-geometry (5):
    g0: LineSegment StartX=-35 StartY=32.5 StartZ=0 EndX=-35 EndY=-32.5 EndZ=0
    g1: LineSegment StartX=-35 StartY=-32.5 StartZ=0 EndX=35 EndY=-32.5 EndZ=0
    g2: LineSegment StartX=35 StartY=-32.5 StartZ=0 EndX=35 EndY=32.5 EndZ=0
    g3: LineSegment StartX=35 StartY=32.5 StartZ=0 EndX=-35 EndY=32.5 EndZ=0
    g4: GeomPoint [constr] X=0 Y=0 Z=0
  constraints (12):
    c: Coincident(g0,g1)
    c: Coincident(g1,g2)
    c: Coincident(g2,g3)
    c: Coincident(g3,g0)
    c: Vertical(g0)
    c: Vertical(g2)
    c: Horizontal(g1)
    c: Horizontal(g3)
    c: Symmetric(g2,g0,g4)
    c: Coincident(g4,g-1)
    c: DistanceX(g3,g3) = 70
    c: DistanceY(g0,g0) = 65
FEATURE [PartDesign::Pad] Pad002  label="Stock002"
  Direction = (0,0,1)
  Length = 1870
  Length2 = 10
  Placement = pos=(0,0,935) rot=(0,0,1;0rad)
  Profile = -> Sketch022
  ReferenceAxis = -> Sketch022 [N_Axis]
  Refine = true
  Reversed = true
  Suppressed = false
  Type = 0
  expr: Length = <<Parameters>>.StileLength
FEATURE [Sketcher::SketchObject] Sketch023
  ArcFitTolerance = 0
  AttachmentSupport = -> [DatumPlane009]
  ExternalGeometry = -> [DatumPlane010,DatumPlane011]
  FullyConstrained = true
  MakeInternals = false
  MapMode = 5
  Placement = pos=(35,0,0) rot=(0.57735,0.57735,0.57735;2.0944rad)
  expr: Constraints[30] = <<Parameters>>.GlassOpeningHeigth
  expr: Constraints[31] = <<Parameters>>.GlassOpeningHeigth
  expr: Constraints[32] = <<Parameters>>.MuntinTenonThickness
  expr: Constraints[33] = <<Parameters>>.GlassRebateDepth
  expr: Constraints[34] = <<Parameters>>.GlassOpeningHeigth + <<Parameters>>.RailBottomWidth
  expr: Constraints[8] = <<Parameters>>.MuntinWidth
  sketch-geometry (12):
    g0: LineSegment StartX=-9.5 StartY=-290 StartZ=0 EndX=-9.5 EndY=-320 EndZ=0
    g1: LineSegment StartX=-9.5 StartY=-320 StartZ=0 EndX=0.5 EndY=-320 EndZ=0
    g2: LineSegment StartX=0.5 StartY=-320 StartZ=0 EndX=0.5 EndY=-290 EndZ=0
    g3: LineSegment StartX=0.5 StartY=-290 StartZ=0 EndX=-9.5 EndY=-290 EndZ=0
    g4: LineSegment StartX=-9.5 StartY=160 StartZ=0 EndX=-9.5 EndY=190 EndZ=0
    g5: LineSegment StartX=-9.5 StartY=190 StartZ=0 EndX=0.5 EndY=190 EndZ=0
    g6: LineSegment StartX=0.5 StartY=190 StartZ=0 EndX=0.5 EndY=160 EndZ=0
    g7: LineSegment StartX=0.5 StartY=160 StartZ=0 EndX=-9.5 EndY=160 EndZ=0
    g8: LineSegment StartX=-9.5 StartY=670 StartZ=0 EndX=-9.5 EndY=640 EndZ=0
    g9: LineSegment StartX=-9.5 StartY=640 StartZ=0 EndX=0.5 EndY=640 EndZ=0
    g10: LineSegment StartX=0.5 StartY=640 StartZ=0 EndX=0.5 EndY=670 EndZ=0
    g11: LineSegment StartX=0.5 StartY=670 StartZ=0 EndX=-9.5 EndY=670 EndZ=0
  constraints (36):
    c: Coincident(g0,g1)
    c: Coincident(g1,g2)
    c: Coincident(g2,g3)
    c: Coincident(g3,g0)
    c: Vertical(g0)
    c: Vertical(g2)
    c: Horizontal(g1)
    c: Horizontal(g3)
    c: DistanceY(g0,g0) = 30
    c: Coincident(g4,g5)
    c: Coincident(g8,g9)
    c: Coincident(g5,g6)
    c: Coincident(g9,g10)
    c: Coincident(g6,g7)
    c: Coincident(g10,g11)
    c: Coincident(g7,g4)
    c: Coincident(g11,g8)
    c: Vertical(g4)
    c: Vertical(g8)
    c: Vertical(g6)
    c: Vertical(g10)
    c: Horizontal(g5)
    c: Horizontal(g9)
    c: Horizontal(g7)
    c: Horizontal(g11)
    c: Equal(g0,g4)
    c: Equal(g0,g8)
    c: Equal(g11,g7)
    c: Equal(g7,g3)
    c: Vertical(g5,g9)
    c: DistanceY(g0,g4) = 450
    c: DistanceY(g4,g8) = 450
    c: DistanceX(g1,g1) = 10
    c: Distance(g1,g-3) = 32
    c: Distance(g0,g-4) = 615
    c: Vertical(g6,g2)
FEATURE [Sketcher::SketchObject] Sketch024  label="Frame rebate opening top004"
  ArcFitTolerance = 0
  AttachmentSupport = -> [DatumPlane009]
  ExternalGeometry = -> [DatumPlane008,DatumPlane010]
  FullyConstrained = true
  MakeInternals = false
  MapMode = 5
  Placement = pos=(35,0,0) rot=(0.57735,0.57735,0.57735;2.0944rad)
  expr: Constraints[6] = <<Parameters>>.WindowFrameRebateWidth
  expr: Constraints[7] = <<Parameters>>.WindowFrameRebateDepth
  sketch-geometry (4):
    g0: LineSegment StartX=12.5 StartY=935 StartZ=0 EndX=12.5 EndY=910 EndZ=0
    g1: LineSegment StartX=12.5 StartY=910 StartZ=0 EndX=32.5 EndY=910 EndZ=0
    g2: LineSegment StartX=32.5 StartY=910 StartZ=0 EndX=32.5 EndY=935 EndZ=0
    g3: LineSegment StartX=32.5 StartY=935 StartZ=0 EndX=12.5 EndY=935 EndZ=0
  constraints (10):
    c: Coincident(g0,g1)
    c: Coincident(g1,g2)
    c: Coincident(g2,g3)
    c: Coincident(g3,g0)
    c: Vertical(g0)
    c: Horizontal(g1)
    c: DistanceX(g3,g3) = 20
    c: Distance(g2,g2) = 25
    c: Tangent(g2,g-4)
    c: Tangent(g3,g-3)
FEATURE [Sketcher::SketchObject] Sketch025  label="Frame rebate closure top004"
  ArcFitTolerance = 0
  AttachmentSupport = -> [DatumPlane009]
  ExternalGeometry = -> [DatumPlane008,DatumPlane010]
  FullyConstrained = true
  MakeInternals = false
  MapMode = 5
  Placement = pos=(35,0,0) rot=(0.57735,0.57735,0.57735;2.0944rad)
  expr: Constraints[6] = <<Parameters>>.WindowInnerLipWidth
  expr: Constraints[7] = <<Parameters>>.FrameThickness
  sketch-geometry (4):
    g0: LineSegment StartX=-17.5 StartY=935 StartZ=0 EndX=-17.5 EndY=920 EndZ=0
    g1: LineSegment StartX=-17.5 StartY=920 StartZ=0 EndX=32.5 EndY=920 EndZ=0
    g2: LineSegment StartX=32.5 StartY=920 StartZ=0 EndX=32.5 EndY=935 EndZ=0
    g3: LineSegment StartX=32.5 StartY=935 StartZ=0 EndX=-17.5 EndY=935 EndZ=0
  constraints (10):
    c: Coincident(g0,g1)
    c: Coincident(g1,g2)
    c: Coincident(g2,g3)
    c: Coincident(g3,g0)
    c: Vertical(g0)
    c: Horizontal(g1)
    c: DistanceY(g2,g2) = 15
    c: DistanceX(g3,g3) = 50
    c: Tangent(g3,g-3)
    c: Tangent(g-4,g2)
FEATURE [Sketcher::SketchObject] Sketch026  label="Frame rebate opening right"
  ArcFitTolerance = 0
  AttachmentSupport = -> [DatumPlane008]
  ExternalGeometry = -> [DatumPlane010,DatumPlane012]
  FullyConstrained = true
  MakeInternals = false
  MapMode = 5
  Placement = pos=(0,0,935) rot=(0,0,1;0rad)
  expr: Constraints[6] = <<Parameters>>.WindowFrameRebateDepth
  expr: Constraints[7] = <<Parameters>>.WindowFrameRebateWidth
  sketch-geometry (4):
    g0: LineSegment StartX=-35 StartY=32.5 StartZ=0 EndX=-35 EndY=12.5 EndZ=0
    g1: LineSegment StartX=-35 StartY=12.5 StartZ=0 EndX=-10 EndY=12.5 EndZ=0
    g2: LineSegment StartX=-10 StartY=12.5 StartZ=0 EndX=-10 EndY=32.5 EndZ=0
    g3: LineSegment StartX=-10 StartY=32.5 StartZ=0 EndX=-35 EndY=32.5 EndZ=0
  constraints (10):
    c: Coincident(g0,g1)
    c: Coincident(g1,g2)
    c: Coincident(g2,g3)
    c: Coincident(g3,g0)
    c: Vertical(g2)
    c: Horizontal(g1)
    c: DistanceX(g3,g3) = 25
    c: DistanceY(g0,g0) = 20
    c: Tangent(g3,g-3)
    c: Tangent(g0,g-4)
FEATURE [Sketcher::SketchObject] Sketch027  label="Frame rebate lip right004"
  ArcFitTolerance = 0
  AttachmentSupport = -> [DatumPlane008]
  ExternalGeometry = -> [DatumPlane010,DatumPlane012]
  FullyConstrained = true
  MakeInternals = false
  MapMode = 5
  Placement = pos=(0,0,935) rot=(0,0,1;0rad)
  expr: Constraints[6] = <<Parameters>>.WindowInnerLipWidth
  expr: Constraints[7] = <<Parameters>>.FrameThickness
  sketch-geometry (4):
    g0: LineSegment StartX=-35 StartY=32.5 StartZ=0 EndX=-35 EndY=-17.5 EndZ=0
    g1: LineSegment StartX=-35 StartY=-17.5 StartZ=0 EndX=-20 EndY=-17.5 EndZ=0
    g2: LineSegment StartX=-20 StartY=-17.5 StartZ=0 EndX=-20 EndY=32.5 EndZ=0
    g3: LineSegment StartX=-20 StartY=32.5 StartZ=0 EndX=-35 EndY=32.5 EndZ=0
  constraints (10):
    c: Coincident(g0,g1)
    c: Coincident(g1,g2)
    c: Coincident(g2,g3)
    c: Coincident(g3,g0)
    c: Vertical(g2)
    c: Horizontal(g1)
    c: DistanceX(g3,g3) = 15
    c: DistanceY(g0,g0) = 50
    c: Tangent(g3,g-3)
    c: Tangent(g0,g-4)
FEATURE [Sketcher::SketchObject] Sketch028  label="Mortise rail top005"
  ArcFitTolerance = 0
  AttachmentOffset = pos=(0,0,-32) rot=(0,0,1;0rad)
  AttachmentSupport = -> [DatumPlane010]
  ExternalGeometry = -> [DatumPlane012,DatumPlane008]
  FullyConstrained = true
  MakeInternals = false
  MapMode = 5
  Placement = pos=(0,0.5,-1e-16) rot=(0,0.707107,0.707107;3.14159rad)
  expr: .AttachmentOffset.Base.z = -<<Parameters>>.GlassRebateDepth
  expr: Constraints[10] = <<Parameters>>.RailTopWidth
  expr: Constraints[11] = <<Parameters>>.RailTopTenonWidth
  expr: Constraints[13] = <<Parameters>>.StileInnerHaunchDepth
  expr: Constraints[9] = <<Parameters>>.StileInnerWidth
  sketch-geometry (6):
    g0: LineSegment StartX=-35 StartY=890 StartZ=0 EndX=15 EndY=890 EndZ=0
    g1: LineSegment StartX=15 StartY=890 StartZ=0 EndX=15 EndY=935 EndZ=0
    g2: LineSegment StartX=15 StartY=935 StartZ=0 EndX=35 EndY=935 EndZ=0
    g3: LineSegment StartX=35 StartY=935 StartZ=0 EndX=35 EndY=820 EndZ=0
    g4: LineSegment StartX=35 StartY=820 StartZ=0 EndX=-35 EndY=820 EndZ=0
    g5: LineSegment StartX=-35 StartY=820 StartZ=0 EndX=-35 EndY=890 EndZ=0
  constraints (16):
    c: Coincident(g0,g1)
    c: Vertical(g1)
    c: Coincident(g1,g2)
    c: Coincident(g2,g3)
    c: Coincident(g3,g4)
    c: Horizontal(g4)
    c: Coincident(g4,g5)
    c: Coincident(g5,g0)
    c: Vertical(g5)
    c: DistanceX(g4,g4) = 70
    c: DistanceY(g3,g3) = 115
    c: DistanceY(g5,g5) = 70
    c: Tangent(g-3,g3)
    c: DistanceX(g2,g2) = 20
    c: Horizontal(g0,g0)
    c: Tangent(g2,g-4)
FEATURE [PartDesign::Pocket] Pocket024  label="Mortise rail top004"
  BaseFeature = -> Pad002
  Direction = (0,-1,2e-16)
  Length = 15
  Length2 = 5
  Placement = pos=(0,0,935) rot=(0,0,1;0rad)
  Profile = -> Sketch028
  ReferenceAxis = -> Sketch028 [N_Axis]
  Refine = true
  Suppressed = false
  Type = 0
  expr: Length = <<Parameters>>.RailTenonThickness
FEATURE [Sketcher::SketchObject] Sketch029
  ArcFitTolerance = 0
  AttachmentSupport = -> [DatumPlane008]
  ExternalGeometry = -> [DatumPlane010,DatumPlane012]
  FullyConstrained = true
  MakeInternals = false
  MapMode = 5
  Placement = pos=(0,0,935) rot=(0,0,1;0rad)
  expr: Constraints[5] = <<Parameters>>.GlassRebateDepth
  expr: Constraints[6] = <<Parameters>>.GlassRebateWidth
  sketch-geometry (4):
    g0: LineSegment StartX=-35 StartY=32.5 StartZ=0 EndX=-35 EndY=0.5 EndZ=0
    g1: LineSegment StartX=-35 StartY=0.5 StartZ=0 EndX=-25 EndY=0.5 EndZ=0
    g2: LineSegment StartX=-25 StartY=0.5 StartZ=0 EndX=-25 EndY=32.5 EndZ=0
    g3: LineSegment StartX=-25 StartY=32.5 StartZ=0 EndX=-35 EndY=32.5 EndZ=0
  constraints (10):
    c: Coincident(g0,g1)
    c: Coincident(g1,g2)
    c: Coincident(g2,g3)
    c: Coincident(g3,g0)
    c: Horizontal(g1)
    c: DistanceY(g2,g2) = 32
    c: DistanceX(g3,g3) = 10
    c: Tangent(g3,g-3)
    c: Vertical(g1,g2)
    c: Tangent(g0,g-4)
FEATURE [Sketcher::SketchObject] Sketch030
  ArcFitTolerance = 0
  AttachmentOffset = pos=(0,0,-32) rot=(0,0,1;0rad)
  AttachmentSupport = -> [DatumPlane010]
  ExternalGeometry = -> [DatumPlane011,DatumPlane009]
  FullyConstrained = true
  MakeInternals = false
  MapMode = 5
  Placement = pos=(0,0.5,-1e-16) rot=(0,0.707107,0.707107;3.14159rad)
  expr: .AttachmentOffset.Base.z = -<<Parameters>>.GlassRebateDepth
  expr: Constraints[10] = <<Parameters>>.RailBottomWidth
  expr: Constraints[11] = <<Parameters>>.RailBottomTenonWidth
  expr: Constraints[14] = <<Parameters>>.StileInnerHaunchDepth
  expr: Constraints[9] = <<Parameters>>.StileInnerWidth
  sketch-geometry (6):
    g0: LineSegment StartX=35 StartY=-770 StartZ=0 EndX=-35 EndY=-770 EndZ=0
    g1: LineSegment StartX=-35 StartY=-770 StartZ=0 EndX=-35 EndY=-870 EndZ=0
    g2: LineSegment StartX=-35 StartY=-870 StartZ=0 EndX=15 EndY=-870 EndZ=0
    g3: LineSegment StartX=15 StartY=-870 StartZ=0 EndX=15 EndY=-935 EndZ=0
    g4: LineSegment StartX=15 StartY=-935 StartZ=0 EndX=35 EndY=-935 EndZ=0
    g5: LineSegment StartX=35 StartY=-935 StartZ=0 EndX=35 EndY=-770 EndZ=0
  constraints (16):
    c: Horizontal(g0)
    c: Coincident(g0,g1)
    c: Coincident(g1,g2)
    c: Coincident(g2,g3)
    c: Vertical(g3)
    c: Coincident(g3,g4)
    c: Coincident(g4,g5)
    c: Coincident(g5,g0)
    c: Vertical(g5)
    c: DistanceX(g0,g0) = 70
    c: DistanceY(g5,g5) = 165
    c: DistanceY(g1,g1) = 100
    c: Tangent(g1,g-4)
    c: Horizontal(g2,g1)
    c: DistanceX(g4,g4) = 20
    c: Tangent(g4,g-3)
FEATURE [PartDesign::Pocket] Pocket026  label="Mortise rail bottom003"
  BaseFeature = -> Pocket024
  Direction = (0,-1,2e-16)
  Length = 15
  Length2 = 5
  Placement = pos=(0,0,935) rot=(0,0,1;0rad)
  Profile = -> Sketch030
  ReferenceAxis = -> Sketch030 [N_Axis]
  Refine = true
  Suppressed = false
  Type = 0
  expr: Length = <<Parameters>>.RailTenonThickness
FEATURE [PartDesign::Pocket] Pocket019  label="Mortises muntin001"
  BaseFeature = -> Pocket026
  Direction = (-1,0,0)
  Length = 5
  Length2 = 5
  Placement = pos=(0,0,935) rot=(0,0,1;0rad)
  Profile = -> Sketch023
  ReferenceAxis = -> Sketch023 [N_Axis]
  Refine = true
  Suppressed = false
  Type = 1
FEATURE [PartDesign::Pocket] Pocket020  label="Frame rebate opening top003"
  BaseFeature = -> Pocket019
  Direction = (-1,0,0)
  Length = 5
  Length2 = 5
  Placement = pos=(0,0,935) rot=(0,0,1;0rad)
  Profile = -> Sketch024
  ReferenceAxis = -> Sketch024 [N_Axis]
  Refine = true
  Suppressed = false
  Type = 1
FEATURE [PartDesign::Pocket] Pocket021  label="Frame rebate lip top003"
  BaseFeature = -> Pocket020
  Direction = (-1,0,0)
  Length = 5
  Length2 = 5
  Placement = pos=(0,0,935) rot=(0,0,1;0rad)
  Profile = -> Sketch025
  ReferenceAxis = -> Sketch025 [N_Axis]
  Refine = true
  Suppressed = false
  Type = 1
FEATURE [PartDesign::Mirrored] Mirrored003  label="Frame rebates bottom001"
  BaseFeature = -> Pocket021
  MirrorPlane = -> XY_Plane003
  Originals = -> [Pocket020,Pocket021]
  Placement = pos=(0,0,935) rot=(0,0,1;0rad)
  Refine = true
  Suppressed = false
  TransformMode = 0
FEATURE [PartDesign::Pocket] Pocket025  label="Glass rebate001"
  BaseFeature = -> Mirrored003
  Direction = (0,0,-1)
  Length = 5
  Length2 = 5
  Placement = pos=(0,0,935) rot=(0,0,1;0rad)
  Profile = -> Sketch029
  ReferenceAxis = -> Sketch029 [N_Axis]
  Refine = true
  Suppressed = false
  Type = 1
FEATURE [PartDesign::Plane] DatumPlane013  label="DatumPlane front001"
  AttachmentOffset = pos=(0,0,32.5) rot=(0,0,1;0rad)
  AttachmentSupport = -> [X_Axis003]
  Length = 70
  MapMode = 3
  Placement = pos=(0,-32.5,7.2e-15) rot=(1,0,0;1.5708rad)
  ResizeMode = 1
  Width = 1870
  expr: .AttachmentOffset.Base.z = <<Parameters>>.WindowThickness / 2
  expr: Length = <<Parameters>>.StileInnerWidth
  expr: Width = <<Parameters>>.StileLength
FEATURE [Sketcher::SketchObject] Sketch031
  ArcFitTolerance = 0
  AttachmentSupport = -> [DatumPlane008]
  ExternalGeometry = -> [DatumPlane009,DatumPlane013]
  FullyConstrained = true
  MakeInternals = false
  MapMode = 5
  Placement = pos=(0,0,935) rot=(0,0,1;0rad)
  expr: Constraints[6] = <<Parameters>>.IntersectionRebateWidth
  expr: Constraints[7] = <<Parameters>>.IntersectionRebateDepth
  sketch-geometry (4):
    g0: LineSegment StartX=25 StartY=-7.1e-15 StartZ=0 EndX=25 EndY=-32.5 EndZ=0
    g1: LineSegment StartX=25 StartY=-32.5 StartZ=0 EndX=35 EndY=-32.5 EndZ=0
    g2: LineSegment StartX=35 StartY=-32.5 StartZ=0 EndX=35 EndY=-7.1e-15 EndZ=0
    g3: LineSegment StartX=35 StartY=-7.1e-15 StartZ=0 EndX=25 EndY=-7.1e-15 EndZ=0
  constraints (10):
    c: Coincident(g0,g1)
    c: Coincident(g1,g2)
    c: Coincident(g2,g3)
    c: Coincident(g3,g0)
    c: Vertical(g0)
    c: Horizontal(g3)
    c: DistanceY(g2,g2) = 32.5
    c: Distance(g1,g1) = 10
    c: Tangent(g2,g-3)
    c: Tangent(g1,g-4)
FEATURE [PartDesign::Pocket] Pocket027  label="Rebate intersection left"
  BaseFeature = -> Pocket025
  Direction = (0,0,-1)
  Length = 5
  Length2 = 5
  Placement = pos=(0,0,935) rot=(0,0,1;0rad)
  Profile = -> Sketch031
  ReferenceAxis = -> Sketch031 [N_Axis]
  Refine = true
  Suppressed = false
  Type = 1
FEATURE [PartDesign::Body] Body003  label="Stile inner left"
  AllowCompound = false
  Group = -> [DatumPlane008,DatumPlane009,DatumPlane010,DatumPlane011,DatumPlane012,DatumPlane013,Sketch022,Pad002,Pocket024,Pocket026,Sketch023,Pocket019,Sketch024,Pocket020,Sketch025,Pocket021,Mirrored003,Sketch026,Sketch027,Sketch028,Sketch029,Pocket025,Sketch030,Sketch031,Pocket027]
  Origin = -> Origin003
  Tip = -> Pocket027
FEATURE [PartDesign::SubShapeBinder] Binder001  label="Stile inner left001"
  BindCopyOnChange = 0
  BindMode = 0
  ClaimChildren = false
  Context = -> Body003 [Binder001.]
  Fuse = false
  MakeFace = true
  OffsetFill = false
  OffsetIntersection = false
  OffsetJoinType = 0
  OffsetOpenResult = false
  PartialLoad = false
  Refine = true
  Relative = true
  Support = -> [Pocket025]
  _Version = 2
FEATURE [Part::Mirroring] Part__Mirroring001  label="Stile inner right (Mirror #2)"
  Base = (0,0,0)
  Normal = (1,0,0)
  Source = -> Binder001
FEATURE [PartDesign::FeatureBase] BaseFeature001
  BaseFeature = -> Part__Mirroring001
  Suppressed = false
FEATURE [PartDesign::Plane] DatumPlane014  label="DatumPlane top003"
  AttachmentOffset = pos=(0,0,935) rot=(0,0,1;0rad)
  AttachmentSupport = -> [X_Axis004]
  Length = 70
  MapMode = 2
  Placement = pos=(0,0,935) rot=(0,0,1;0rad)
  ResizeMode = 1
  Width = 65
  expr: .AttachmentOffset.Base.z = <<Parameters>>.StileLength / 2
  expr: Length = <<Parameters>>.StileInnerWidth
  expr: Width = <<Parameters>>.WindowThickness
FEATURE [PartDesign::Plane] DatumPlane016  label="DatumPlane rear002"
  AttachmentOffset = pos=(0,0,32.5) rot=(0,0,1;0rad)
  AttachmentSupport = -> [X_Axis004]
  Length = 70
  MapMode = 3
  Placement = pos=(0,32.5,-7.2e-15) rot=(0,0.707107,0.707107;3.14159rad)
  ResizeMode = 1
  Width = 1870
  expr: .AttachmentOffset.Base.z = <<Parameters>>.WindowThickness / 2
  expr: Length = <<Parameters>>.StileInnerWidth
  expr: Width = <<Parameters>>.StileLength
FEATURE [PartDesign::Plane] DatumPlane017  label="DatumPlane left002"
  AttachmentOffset = pos=(0,0,35) rot=(0,0,1;0rad)
  AttachmentSupport = -> [X_Axis004]
  Length = 65
  MapMode = 4
  Placement = pos=(-35,0,0) rot=(0.57735,-0.57735,-0.57735;2.0944rad)
  ResizeMode = 1
  Width = 1870
  expr: .AttachmentOffset.Base.z = <<Parameters>>.StileInnerWidth / 2
  expr: Length = <<Parameters>>.WindowThickness
  expr: Width = <<Parameters>>.StileLength
FEATURE [Sketcher::SketchObject] Sketch032
  ArcFitTolerance = 0
  AttachmentSupport = -> [DatumPlane014]
  ExternalGeometry = -> [DatumPlane016,DatumPlane017]
  FullyConstrained = true
  MakeInternals = false
  MapMode = 5
  Placement = pos=(0,0,935) rot=(0,0,1;0rad)
  expr: Constraints[6] = <<Parameters>>.IntersectionRebateDepth
  expr: Constraints[7] = <<Parameters>>.IntersectionRebateWidth
  sketch-geometry (4):
    g0: LineSegment StartX=-35 StartY=32.5 StartZ=0 EndX=-35 EndY=0 EndZ=0
    g1: LineSegment StartX=-35 StartY=0 StartZ=0 EndX=-25 EndY=0 EndZ=0
    g2: LineSegment StartX=-25 StartY=0 StartZ=0 EndX=-25 EndY=32.5 EndZ=0
    g3: LineSegment StartX=-25 StartY=32.5 StartZ=0 EndX=-35 EndY=32.5 EndZ=0
  constraints (10):
    c: Coincident(g0,g1)
    c: Coincident(g1,g2)
    c: Coincident(g2,g3)
    c: Coincident(g3,g0)
    c: Vertical(g2)
    c: Horizontal(g1)
    c: DistanceX(g3,g3) = 10
    c: DistanceY(g0,g0) = 32.5
    c: Tangent(g0,g-4)
    c: Tangent(g3,g-3)
FEATURE [PartDesign::Pocket] Pocket028  label="Rebate intersection right"
  BaseFeature = -> BaseFeature001
  Direction = (0,0,-1)
  Length = 5
  Length2 = 5
  Profile = -> Sketch032
  ReferenceAxis = -> Sketch032 [N_Axis]
  Refine = true
  Suppressed = false
  Type = 1
FEATURE [PartDesign::Body] Body004  label="Stile inner right"
  AllowCompound = false
  BaseFeature = -> Part__Mirroring001
  Group = -> [BaseFeature001,DatumPlane014,DatumPlane016,DatumPlane017,Sketch032,Pocket028]
  Origin = -> Origin004
  Tip = -> Pocket028
FEATURE [PartDesign::Plane] DatumPlane018  label="DatumPlane top004"
  AttachmentOffset = pos=(0,0,15) rot=(0,0,1;0rad)
  AttachmentSupport = -> [X_Axis005]
  Length = 610
  MapMode = 2
  Placement = pos=(0,0,15) rot=(0,0,1;0rad)
  ResizeMode = 1
  Width = 50
  expr: .AttachmentOffset.Base.z = <<Parameters>>.MuntinWidth / 2
  expr: Length = <<Parameters>>.RailLength
  expr: Width = <<Parameters>>.MuntinThickness
FEATURE [PartDesign::Plane] DatumPlane019  label="DatumPlane right003"
  AttachmentOffset = pos=(0,0,305) rot=(0,0,1;0rad)
  AttachmentSupport = -> [X_Axis005]
  Length = 50
  MapMode = 4
  Placement = pos=(305,0,0) rot=(0.57735,0.57735,0.57735;2.0944rad)
  ResizeMode = 1
  Width = 30
  expr: .AttachmentOffset.Base.z = <<Parameters>>.RailLength / 2
  expr: Length = <<Parameters>>.MuntinThickness
  expr: Width = <<Parameters>>.MuntinWidth
FEATURE [PartDesign::Plane] DatumPlane020  label="DatumPlane front002"
  AttachmentOffset = pos=(0,0,25) rot=(0,0,1;0rad)
  AttachmentSupport = -> [X_Axis005]
  Length = 610
  MapMode = 3
  Placement = pos=(0,-25,5.6e-15) rot=(1,0,0;1.5708rad)
  ResizeMode = 1
  Width = 30
  expr: .AttachmentOffset.Base.z = <<Parameters>>.MuntinThickness / 2
  expr: Length = <<Parameters>>.RailLength
  expr: Width = <<Parameters>>.MuntinWidth
FEATURE [Sketcher::SketchObject] Sketch033
  ArcFitTolerance = 0
  AttachmentSupport = -> [DatumPlane019]
  FullyConstrained = true
  MakeInternals = false
  MapMode = 5
  Placement = pos=(305,0,0) rot=(0.57735,0.57735,0.57735;2.0944rad)
  expr: Constraints[10] = <<Parameters>>.MuntinThickness
  expr: Constraints[11] = <<Parameters>>.MuntinWidth
  sketch-geometry (5):
    g0: LineSegment StartX=-25 StartY=15 StartZ=0 EndX=-25 EndY=-15 EndZ=0
    g1: LineSegment StartX=-25 StartY=-15 StartZ=0 EndX=25 EndY=-15 EndZ=0
    g2: LineSegment StartX=25 StartY=-15 StartZ=0 EndX=25 EndY=15 EndZ=0
    g3: LineSegment StartX=25 StartY=15 StartZ=0 EndX=-25 EndY=15 EndZ=0
    g4: GeomPoint [constr] X=0 Y=0 Z=0
  constraints (12):
    c: Coincident(g0,g1)
    c: Coincident(g1,g2)
    c: Coincident(g2,g3)
    c: Coincident(g3,g0)
    c: Vertical(g0)
    c: Vertical(g2)
    c: Horizontal(g1)
    c: Horizontal(g3)
    c: Symmetric(g2,g0,g4)
    c: Coincident(g4,g-1)
    c: DistanceX(g3,g3) = 50
    c: DistanceY(g0,g0) = 30
FEATURE [PartDesign::Pad] Pad003  label="Stock003"
  Direction = (1,0,0)
  Length = 610
  Length2 = 10
  Placement = pos=(305,0,0) rot=(0.57735,0.57735,0.57735;2.0944rad)
  Profile = -> Sketch033
  ReferenceAxis = -> Sketch033 [N_Axis]
  Refine = true
  Reversed = true
  Suppressed = false
  Type = 0
  expr: Length = <<Parameters>>.RailLength
FEATURE [Sketcher::SketchObject] Sketch034
  ArcFitTolerance = 0
  AttachmentSupport = -> [DatumPlane018]
  ExternalGeometry = -> [DatumPlane019,DatumPlane020]
  FullyConstrained = true
  MakeInternals = false
  MapMode = 5
  Placement = pos=(0,0,15) rot=(0,0,1;0rad)
  expr: Constraints[14] = <<Parameters>>.StileInnerWidth - <<Parameters>>.GlassRebateWidth
  expr: Constraints[15] = <<Parameters>>.MuntinThickness
  expr: Constraints[16] = <<Parameters>>.GlassRebateDepth
  expr: Constraints[17] = <<Parameters>>.MuntinTenonThickness
  expr: Constraints[18] = <<Parameters>>.StileInnerWidth
  sketch-geometry (8):
    g0: LineSegment StartX=305 StartY=-17 StartZ=0 EndX=235 EndY=-17 EndZ=0
    g1: LineSegment StartX=235 StartY=-17 StartZ=0 EndX=235 EndY=-25 EndZ=0
    g2: LineSegment StartX=235 StartY=-25 StartZ=0 EndX=305 EndY=-25 EndZ=0
    g3: LineSegment StartX=305 StartY=-25 StartZ=0 EndX=305 EndY=-17 EndZ=0
    g4: LineSegment StartX=305 StartY=25 StartZ=0 EndX=245 EndY=25 EndZ=0
    g5: LineSegment StartX=245 StartY=25 StartZ=0 EndX=245 EndY=-7 EndZ=0
    g6: LineSegment StartX=245 StartY=-7 StartZ=0 EndX=305 EndY=-7 EndZ=0
    g7: LineSegment StartX=305 StartY=-7 StartZ=0 EndX=305 EndY=25 EndZ=0
  constraints (22):
    c: Coincident(g0,g1)
    c: Coincident(g1,g2)
    c: Coincident(g2,g3)
    c: Coincident(g3,g0)
    c: Horizontal(g0)
    c: Vertical(g1)
    c: Vertical(g3)
    c: Coincident(g4,g5)
    c: Coincident(g5,g6)
    c: Coincident(g6,g7)
    c: Coincident(g7,g4)
    c: Horizontal(g4)
    c: Horizontal(g6)
    c: Vertical(g5)
    c: DistanceX(g4,g4) = 60
    c: DistanceY(g2,g4) = 50
    c: DistanceY(g7,g7) = 32
    c: DistanceY(g0,g6) = 10
    c: Distance(g2,g2) = 70
    c: Tangent(g7,g-3)
    c: Vertical(g0,g6)
    c: Tangent(g2,g-4)
FEATURE [PartDesign::Pocket] Pocket029  label="Tenon inner"
  BaseFeature = -> Pad003
  Direction = (0,0,-1)
  Length = 5
  Length2 = 5
  Placement = pos=(305,0,0) rot=(0.57735,0.57735,0.57735;2.0944rad)
  Profile = -> Sketch034
  ReferenceAxis = -> Sketch034 [N_Axis]
  Refine = true
  Suppressed = false
  Type = 1
FEATURE [PartDesign::Plane] DatumPlane021  label="DatumPlane left003"
  AttachmentOffset = pos=(0,0,305) rot=(0,0,1;0rad)
  AttachmentSupport = -> [X_Axis005]
  Length = 50
  MapMode = 4
  Placement = pos=(-305,0,0) rot=(0.57735,-0.57735,-0.57735;2.0944rad)
  ResizeMode = 1
  Width = 30
  expr: .AttachmentOffset.Base.z = <<Parameters>>.RailLength / 2
  expr: Length = <<Parameters>>.MuntinThickness
  expr: Width = <<Parameters>>.MuntinWidth
FEATURE [Sketcher::SketchObject] Sketch036
  ArcFitTolerance = 0
  AttachmentSupport = -> [DatumPlane018]
  ExternalGeometry = -> [DatumPlane021,DatumPlane020]
  FullyConstrained = true
  MakeInternals = false
  MapMode = 5
  Placement = pos=(0,0,15) rot=(0,0,1;0rad)
  expr: Constraints[14] = <<Parameters>>.StileOuterWidth
  expr: Constraints[16] = <<Parameters>>.StileOuterWidth - <<Parameters>>.GlassRebateWidth
  expr: Constraints[17] = <<Parameters>>.GlassRebateDepth
  expr: Constraints[18] = <<Parameters>>.MuntinTenonThickness
  expr: Constraints[19] = <<Parameters>>.MuntinThickness
  sketch-geometry (8):
    g0: LineSegment StartX=-305 StartY=25 StartZ=0 EndX=-305 EndY=-7 EndZ=0
    g1: LineSegment StartX=-305 StartY=-7 StartZ=0 EndX=-225 EndY=-7 EndZ=0
    g2: LineSegment StartX=-225 StartY=-7 StartZ=0 EndX=-225 EndY=25 EndZ=0
    g3: LineSegment StartX=-225 StartY=25 StartZ=0 EndX=-305 EndY=25 EndZ=0
    g4: LineSegment StartX=-305 StartY=-17 StartZ=0 EndX=-305 EndY=-25 EndZ=0
    g5: LineSegment StartX=-305 StartY=-25 StartZ=0 EndX=-215 EndY=-25 EndZ=0
    g6: LineSegment StartX=-215 StartY=-25 StartZ=0 EndX=-215 EndY=-17 EndZ=0
    g7: LineSegment StartX=-215 StartY=-17 StartZ=0 EndX=-305 EndY=-17 EndZ=0
  constraints (22):
    c: Coincident(g0,g1)
    c: Coincident(g1,g2)
    c: Coincident(g2,g3)
    c: Coincident(g3,g0)
    c: Vertical(g2)
    c: Horizontal(g1)
    c: Horizontal(g3)
    c: Coincident(g4,g5)
    c: Coincident(g5,g6)
    c: Coincident(g6,g7)
    c: Coincident(g7,g4)
    c: Vertical(g4)
    c: Vertical(g6)
    c: Horizontal(g7)
    c: DistanceX(g5,g5) = 90
    c: Vertical(g4,g0)
    c: DistanceX(g3,g3) = 80
    c: DistanceY(g0,g0) = 32
    c: Distance(g0,g4) = 10
    c: DistanceY(g4,g0) = 50
    c: Tangent(g0,g-3)
    c: Tangent(g5,g-4)
FEATURE [PartDesign::Pocket] Pocket031  label="Tenon outer"
  BaseFeature = -> Pocket029
  Direction = (0,0,-1)
  Length = 5
  Length2 = 5
  Placement = pos=(305,0,0) rot=(0.57735,0.57735,0.57735;2.0944rad)
  Profile = -> Sketch036
  ReferenceAxis = -> Sketch036 [N_Axis]
  Refine = true
  Suppressed = false
  Type = 1
FEATURE [PartDesign::Plane] DatumPlane022  label="DatumPlane rear003"
  AttachmentOffset = pos=(0,0,25) rot=(0,0,1;0rad)
  AttachmentSupport = -> [X_Axis005]
  Length = 610
  MapMode = 3
  Placement = pos=(0,25,-5.6e-15) rot=(0,0.707107,0.707107;3.14159rad)
  ResizeMode = 1
  Width = 30
  expr: .AttachmentOffset.Base.z = <<Parameters>>.MuntinThickness / 2
  expr: Length = <<Parameters>>.RailLength
  expr: Width = <<Parameters>>.MuntinWidth
FEATURE [Sketcher::SketchObject] Sketch037
  ArcFitTolerance = 0
  AttachmentSupport = -> [DatumPlane019]
  ExternalGeometry = -> [DatumPlane018,DatumPlane022]
  FullyConstrained = true
  MakeInternals = false
  MapMode = 5
  Placement = pos=(305,0,0) rot=(0.57735,0.57735,0.57735;2.0944rad)
  expr: Constraints[6] = <<Parameters>>.GlassRebateDepth
  expr: Constraints[7] = <<Parameters>>.GlassRebateWidth
  sketch-geometry (4):
    g0: LineSegment StartX=25 StartY=15 StartZ=0 EndX=-7 EndY=15 EndZ=0
    g1: LineSegment StartX=-7 StartY=15 StartZ=0 EndX=-7 EndY=5 EndZ=0
    g2: LineSegment StartX=-7 StartY=5 StartZ=0 EndX=25 EndY=5 EndZ=0
    g3: LineSegment StartX=25 StartY=5 StartZ=0 EndX=25 EndY=15 EndZ=0
  constraints (10):
    c: Coincident(g0,g1)
    c: Coincident(g1,g2)
    c: Coincident(g2,g3)
    c: Coincident(g3,g0)
    c: Horizontal(g2)
    c: Vertical(g1)
    c: DistanceX(g0,g0) = 32
    c: DistanceY(g3,g3) = 10
    c: Tangent(g-4,g3)
    c: Tangent(g0,g-3)
FEATURE [PartDesign::Pocket] Pocket032  label="Glass rebate top"
  BaseFeature = -> Pocket031
  Direction = (-1,0,0)
  Length = 5
  Length2 = 5
  Placement = pos=(305,0,0) rot=(0.57735,0.57735,0.57735;2.0944rad)
  Profile = -> Sketch037
  ReferenceAxis = -> Sketch037 [N_Axis]
  Refine = true
  Suppressed = false
  Type = 1
FEATURE [PartDesign::Mirrored] Mirrored004  label="Glass rebate bottom"
  BaseFeature = -> Pocket032
  MirrorPlane = -> Sketch037 [H_Axis]
  Originals = -> [Pocket032]
  Placement = pos=(305,0,0) rot=(0.57735,0.57735,0.57735;2.0944rad)
  Refine = true
  Suppressed = false
  TransformMode = 0
FEATURE [Sketcher::SketchObject] Sketch038
  ArcFitTolerance = 0
  AttachmentSupport = -> [DatumPlane018]
  ExternalGeometry = -> [DatumPlane021,DatumPlane020]
  FullyConstrained = true
  MakeInternals = false
  MapMode = 5
  Placement = pos=(0,0,15) rot=(0,0,1;0rad)
  expr: Constraints[6] = <<Parameters>>.WindowInnerLipWidth
  expr: Constraints[7] = <<Parameters>>.MuntinThickness
  sketch-geometry (4):
    g0: LineSegment StartX=-305 StartY=25 StartZ=0 EndX=-305 EndY=-25 EndZ=0
    g1: LineSegment StartX=-305 StartY=-25 StartZ=0 EndX=-290 EndY=-25 EndZ=0
    g2: LineSegment StartX=-290 StartY=-25 StartZ=0 EndX=-290 EndY=25 EndZ=0
    g3: LineSegment StartX=-290 StartY=25 StartZ=0 EndX=-305 EndY=25 EndZ=0
  constraints (10):
    c: Coincident(g0,g1)
    c: Coincident(g1,g2)
    c: Coincident(g2,g3)
    c: Coincident(g3,g0)
    c: Vertical(g2)
    c: Horizontal(g3)
    c: Distance(g3,g3) = 15
    c: DistanceY(g0,g0) = 50
    c: Tangent(g0,g-3)
    c: Tangent(g1,g-4)
FEATURE [Sketcher::SketchObject] Sketch039
  ArcFitTolerance = 0
  AttachmentSupport = -> [DatumPlane018]
  ExternalGeometry = -> [DatumPlane019,DatumPlane022]
  FullyConstrained = true
  MakeInternals = false
  MapMode = 5
  Placement = pos=(0,0,15) rot=(0,0,1;0rad)
  expr: Constraints[10] = <<Parameters>>.IntersectionRebateWidth
  expr: Constraints[5] = <<Parameters>>.IntersectionRebateDepth
  expr: Constraints[6] = <<Parameters>>.IntersectionRebateWidth
  sketch-geometry (4):
    g0: LineSegment StartX=295 StartY=-7.5 StartZ=0 EndX=295 EndY=-40 EndZ=0
    g1: LineSegment StartX=295 StartY=-40 StartZ=0 EndX=305 EndY=-40 EndZ=0
    g2: LineSegment StartX=305 StartY=-40 StartZ=0 EndX=305 EndY=-7.5 EndZ=0
    g3: LineSegment StartX=305 StartY=-7.5 StartZ=0 EndX=295 EndY=-7.5 EndZ=0
  constraints (11):
    c: Coincident(g0,g1)
    c: Coincident(g1,g2)
    c: Coincident(g2,g3)
    c: Coincident(g3,g0)
    c: Horizontal(g3)
    c: Distance(g3,g3) = 10
    c: DistanceY(g0,g0) = 32.5
    c: Vertical(g0,g0)
    c: Tangent(g2,g-3)
    c: Horizontal(g0,g1)
    c: Distance(g2,g-4) = 32.5
FEATURE [PartDesign::Pocket] Pocket033  label="Frame outer rebate"
  BaseFeature = -> Mirrored004
  Direction = (0,0,-1)
  Length = 5
  Length2 = 5
  Placement = pos=(305,0,0) rot=(0.57735,0.57735,0.57735;2.0944rad)
  Profile = -> Sketch038
  ReferenceAxis = -> Sketch038 [N_Axis]
  Refine = true
  Suppressed = false
  Type = 1
FEATURE [PartDesign::Pocket] Pocket034  label="Frame inner intersection rebate"
  BaseFeature = -> Pocket033
  Direction = (0,0,-1)
  Length = 5
  Length2 = 5
  Placement = pos=(305,0,0) rot=(0.57735,0.57735,0.57735;2.0944rad)
  Profile = -> Sketch039
  ReferenceAxis = -> Sketch039 [N_Axis]
  Refine = true
  Suppressed = false
  Type = 1
FEATURE [PartDesign::Body] Body005  label="Muntin single left"
  AllowCompound = false
  Group = -> [DatumPlane018,DatumPlane019,DatumPlane020,DatumPlane021,DatumPlane022,Sketch033,Pad003,Sketch034,Pocket029,Pocket031,Sketch036,Sketch037,Pocket032,Mirrored004,Sketch038,Sketch039,Pocket033,Pocket034]
  Origin = -> Origin005
  Tip = -> Pocket034
FEATURE [PartDesign::SubShapeBinder] Binder002  label="Muntin single left binder"
  BindCopyOnChange = 0
  BindMode = 0
  ClaimChildren = false
  Context = -> Body005 [Binder002.]
  Fuse = false
  MakeFace = true
  OffsetFill = false
  OffsetIntersection = false
  OffsetJoinType = 0
  OffsetOpenResult = false
  PartialLoad = false
  Refine = true
  Relative = true
  Support = -> [Pocket033]
  _Version = 2
FEATURE [PartDesign::FeatureBase] BaseFeature002
  BaseFeature = -> Binder002
  Suppressed = false
FEATURE [PartDesign::Plane] DatumPlane023  label="DatumPlane top005"
  AttachmentOffset = pos=(0,0,15) rot=(0,0,1;0rad)
  AttachmentSupport = -> [X_Axis006]
  Length = 610
  MapMode = 2
  Placement = pos=(0,0,15) rot=(0,0,1;0rad)
  ResizeMode = 1
  Width = 50
  expr: .AttachmentOffset.Base.z = <<Parameters>>.MuntinWidth / 2
  expr: Length = <<Parameters>>.RailLength
  expr: Width = <<Parameters>>.MuntinThickness
FEATURE [PartDesign::Plane] DatumPlane024  label="DatumPlane right004"
  AttachmentOffset = pos=(0,0,305) rot=(0,0,1;0rad)
  AttachmentSupport = -> [X_Axis006]
  Length = 50
  MapMode = 4
  Placement = pos=(305,0,0) rot=(0.57735,0.57735,0.57735;2.0944rad)
  ResizeMode = 1
  Width = 30
  expr: .AttachmentOffset.Base.z = <<Parameters>>.RailLength / 2
  expr: Length = <<Parameters>>.MuntinThickness
  expr: Width = <<Parameters>>.MuntinWidth
FEATURE [PartDesign::Plane] DatumPlane025  label="DatumPlane front003"
  AttachmentOffset = pos=(0,0,25) rot=(0,0,1;0rad)
  AttachmentSupport = -> [X_Axis006]
  Length = 610
  MapMode = 3
  Placement = pos=(0,-25,5.6e-15) rot=(1,0,0;1.5708rad)
  ResizeMode = 1
  Width = 30
  expr: .AttachmentOffset.Base.z = <<Parameters>>.MuntinThickness / 2
  expr: Length = <<Parameters>>.RailLength
  expr: Width = <<Parameters>>.MuntinWidth
FEATURE [PartDesign::Plane] DatumPlane026  label="DatumPlane left004"
  AttachmentOffset = pos=(0,0,305) rot=(0,0,1;0rad)
  AttachmentSupport = -> [X_Axis006]
  Length = 50
  MapMode = 4
  Placement = pos=(-305,0,0) rot=(0.57735,-0.57735,-0.57735;2.0944rad)
  ResizeMode = 1
  Width = 30
  expr: .AttachmentOffset.Base.z = <<Parameters>>.RailLength / 2
  expr: Length = <<Parameters>>.MuntinThickness
  expr: Width = <<Parameters>>.MuntinWidth
FEATURE [PartDesign::Plane] DatumPlane027  label="DatumPlane rear004"
  AttachmentOffset = pos=(0,0,25) rot=(0,0,1;0rad)
  AttachmentSupport = -> [X_Axis006]
  Length = 610
  MapMode = 3
  Placement = pos=(0,25,-5.6e-15) rot=(0,0.707107,0.707107;3.14159rad)
  ResizeMode = 1
  Width = 30
  expr: .AttachmentOffset.Base.z = <<Parameters>>.MuntinThickness / 2
  expr: Length = <<Parameters>>.RailLength
  expr: Width = <<Parameters>>.MuntinWidth
FEATURE [Sketcher::SketchObject] Sketch040
  ArcFitTolerance = 0
  AttachmentSupport = -> [DatumPlane023]
  ExternalGeometry = -> [DatumPlane027,DatumPlane024]
  FullyConstrained = true
  MakeInternals = false
  MapMode = 5
  Placement = pos=(0,0,15) rot=(0,0,1;0rad)
  expr: Constraints[10] = <<Parameters>>.GlassRebateDepth
  expr: Constraints[11] = <<Parameters>>.GlassOpeningWidth / 2 - <<Parameters>>.MuntinWidth / 2 + <<Parameters>>.StileInnerWidth
  expr: Constraints[8] = <<Parameters>>.MuntinTenonThickness
  expr: Constraints[9] = <<Parameters>>.MuntinWidth
  sketch-geometry (4):
    g0: LineSegment StartX=-5 StartY=-7 StartZ=0 EndX=-5 EndY=-17 EndZ=0
    g1: LineSegment StartX=-5 StartY=-17 StartZ=0 EndX=25 EndY=-17 EndZ=0
    g2: LineSegment StartX=25 StartY=-17 StartZ=0 EndX=25 EndY=-7 EndZ=0
    g3: LineSegment StartX=25 StartY=-7 StartZ=0 EndX=-5 EndY=-7 EndZ=0
  constraints (12):
    c: Coincident(g0,g1)
    c: Coincident(g1,g2)
    c: Coincident(g2,g3)
    c: Coincident(g3,g0)
    c: Vertical(g0)
    c: Vertical(g2)
    c: Horizontal(g1)
    c: Horizontal(g3)
    c: DistanceY(g2,g2) = 10
    c: DistanceX(g1,g1) = 30
    c: Distance(g0,g-3) = 32
    c: Distance(g2,g-4) = 280
FEATURE [PartDesign::Pocket] Pocket035  label="Muntin bar mortise"
  BaseFeature = -> BaseFeature002
  Direction = (0,0,-1)
  Length = 15
  Length2 = 5
  Profile = -> Sketch040
  ReferenceAxis = -> Sketch040 [N_Axis]
  Refine = true
  Suppressed = false
  Type = 0
  expr: Length = <<Parameters>>.MuntinBarTenonLength
FEATURE [Sketcher::SketchObject] Sketch041
  ArcFitTolerance = 0
  AttachmentSupport = -> [DatumPlane023]
  ExternalGeometry = -> [DatumPlane024,DatumPlane027]
  FullyConstrained = true
  MakeInternals = false
  MapMode = 5
  Placement = pos=(0,0,15) rot=(0,0,1;0rad)
  expr: Constraints[10] = <<Parameters>>.IntersectionRebateWidth
  expr: Constraints[5] = <<Parameters>>.IntersectionRebateDepth
  expr: Constraints[6] = <<Parameters>>.IntersectionRebateWidth
  sketch-geometry (4):
    g0: LineSegment StartX=295 StartY=-7.5 StartZ=0 EndX=295 EndY=-40 EndZ=0
    g1: LineSegment StartX=295 StartY=-40 StartZ=0 EndX=305 EndY=-40 EndZ=0
    g2: LineSegment StartX=305 StartY=-40 StartZ=0 EndX=305 EndY=-7.5 EndZ=0
    g3: LineSegment StartX=305 StartY=-7.5 StartZ=0 EndX=295 EndY=-7.5 EndZ=0
  constraints (11):
    c: Coincident(g0,g1)
    c: Coincident(g1,g2)
    c: Coincident(g2,g3)
    c: Coincident(g3,g0)
    c: Horizontal(g3)
    c: Distance(g3,g3) = 10
    c: DistanceY(g0,g0) = 32.5
    c: Vertical(g0,g0)
    c: Horizontal(g0,g1)
    c: Tangent(g2,g-3)
    c: Distance(g2,g-4) = 32.5
FEATURE [PartDesign::Pocket] Pocket036  label="Frame inner intersection rebate001"
  BaseFeature = -> Pocket035
  Direction = (0,0,-1)
  Length = 5
  Length2 = 5
  Profile = -> Sketch041
  ReferenceAxis = -> Sketch041 [N_Axis]
  Refine = true
  Suppressed = false
  Type = 1
FEATURE [PartDesign::Body] Body006  label="Muntin partitioned left"
  AllowCompound = false
  Group = -> [DatumPlane023,DatumPlane024,DatumPlane025,DatumPlane026,DatumPlane027,BaseFeature002,Sketch040,Pocket035,Sketch041,Pocket036]
  Origin = -> Origin006
  Tip = -> Pocket036
FEATURE [Part::Mirroring] Part__Mirroring002  label="Muntin single right (Mirror #3)"
  Base = (0,0,0)
  Normal = (1,0,0)
  Source = -> Binder002
FEATURE [PartDesign::FeatureBase] BaseFeature003
  BaseFeature = -> Part__Mirroring002
  Suppressed = false
FEATURE [PartDesign::Body] Body007  label="Muntin single right"
  AllowCompound = false
  BaseFeature = -> Part__Mirroring002
  Group = -> [BaseFeature003]
  Origin = -> Origin007
  Tip = -> BaseFeature003
FEATURE [PartDesign::SubShapeBinder] Binder003  label="Muntin single left partitioned binder"
  BindCopyOnChange = 0
  BindMode = 0
  ClaimChildren = false
  Context = -> Body007 [Binder003.]
  Fuse = false
  MakeFace = true
  OffsetFill = false
  OffsetIntersection = false
  OffsetJoinType = 0
  OffsetOpenResult = false
  PartialLoad = false
  Refine = true
  Relative = true
  Support = -> [Body006[Pocket035.]]
  _Version = 2
FEATURE [Part::Mirroring] Part__Mirroring003  label="Muntin partitioned right (Mirror #4)"
  Base = (0,0,0)
  Normal = (1,0,0)
  Source = -> Binder003
FEATURE [PartDesign::FeatureBase] BaseFeature004
  BaseFeature = -> Part__Mirroring003
  Suppressed = false
FEATURE [PartDesign::Body] Body008  label="Muntin partitioned right"
  AllowCompound = false
  BaseFeature = -> Part__Mirroring003
  Group = -> [BaseFeature004]
  Origin = -> Origin008
  Tip = -> BaseFeature004
FEATURE [PartDesign::Plane] DatumPlane028  label="DatumPlane top006"
  AttachmentOffset = pos=(0,0,57.5) rot=(0,0,1;0rad)
  AttachmentSupport = -> [X_Axis009]
  Length = 610
  MapMode = 2
  Placement = pos=(0,0,57.5) rot=(0,0,1;0rad)
  ResizeMode = 1
  Width = 65
  expr: .AttachmentOffset.Base.z = <<Parameters>>.RailTopWidth / 2
  expr: Length = <<Parameters>>.RailLength
  expr: Width = <<Parameters>>.WindowThickness
FEATURE [PartDesign::Plane] DatumPlane029  label="DatumPlane right005"
  AttachmentOffset = pos=(0,0,305) rot=(0,0,1;0rad)
  AttachmentSupport = -> [X_Axis009]
  Length = 65
  MapMode = 4
  Placement = pos=(305,0,0) rot=(0.57735,0.57735,0.57735;2.0944rad)
  ResizeMode = 1
  Width = 115
  expr: .AttachmentOffset.Base.z = <<Parameters>>.RailLength / 2
  expr: Length = <<Parameters>>.WindowThickness
  expr: Width = <<Parameters>>.RailTopWidth
FEATURE [PartDesign::Plane] DatumPlane031  label="DatumPlane front004"
  AttachmentOffset = pos=(0,0,32.5) rot=(0,0,1;0rad)
  AttachmentSupport = -> [X_Axis009]
  Length = 610
  MapMode = 3
  Placement = pos=(0,-32.5,7.2e-15) rot=(1,0,0;1.5708rad)
  ResizeMode = 1
  Width = 115
  expr: .AttachmentOffset.Base.z = <<Parameters>>.WindowThickness / 2
  expr: Length = <<Parameters>>.RailLength
  expr: Width = <<Parameters>>.RailTopWidth
FEATURE [Sketcher::SketchObject] Sketch042
  ArcFitTolerance = 0
  AttachmentSupport = -> [DatumPlane031]
  FullyConstrained = true
  MakeInternals = false
  MapMode = 5
  Placement = pos=(0,-32.5,7.2e-15) rot=(1,0,0;1.5708rad)
  expr: Constraints[10] = <<Parameters>>.RailLength
  expr: Constraints[11] = <<Parameters>>.RailTopWidth
  sketch-geometry (5):
    g0: LineSegment StartX=-305 StartY=57.5 StartZ=0 EndX=-305 EndY=-57.5 EndZ=0
    g1: LineSegment StartX=-305 StartY=-57.5 StartZ=0 EndX=305 EndY=-57.5 EndZ=0
    g2: LineSegment StartX=305 StartY=-57.5 StartZ=0 EndX=305 EndY=57.5 EndZ=0
    g3: LineSegment StartX=305 StartY=57.5 StartZ=0 EndX=-305 EndY=57.5 EndZ=0
    g4: GeomPoint [constr] X=0 Y=0 Z=0
  constraints (12):
    c: Coincident(g0,g1)
    c: Coincident(g1,g2)
    c: Coincident(g2,g3)
    c: Coincident(g3,g0)
    c: Vertical(g0)
    c: Vertical(g2)
    c: Horizontal(g1)
    c: Horizontal(g3)
    c: Symmetric(g2,g0,g4)
    c: Coincident(g4,g-1)
    c: DistanceX(g3,g3) = 610
    c: DistanceY(g2,g2) = 115
FEATURE [PartDesign::Pad] Pad004  label="Stock004"
  Direction = (0,-1,2e-16)
  Length = 65
  Length2 = 10
  Placement = pos=(0,-32.5,7.2e-15) rot=(1,0,0;1.5708rad)
  Profile = -> Sketch042
  ReferenceAxis = -> Sketch042 [N_Axis]
  Refine = true
  Reversed = true
  Suppressed = false
  Type = 0
  expr: Length = <<Parameters>>.WindowThickness
FEATURE [Sketcher::SketchObject] Sketch043
  ArcFitTolerance = 0
  AttachmentSupport = -> [DatumPlane028]
  ExternalGeometry = -> [DatumPlane029,DatumPlane031]
  FullyConstrained = true
  MakeInternals = false
  MapMode = 5
  Placement = pos=(0,0,57.5) rot=(0,0,1;0rad)
  expr: Constraints[15] = <<Parameters>>.StileInnerWidth
  expr: Constraints[16] = <<Parameters>>.StileInnerWidth - <<Parameters>>.GlassRebateWidth
  expr: Constraints[17] = <<Parameters>>.GlassRebateDepth
  expr: Constraints[18] = <<Parameters>>.RailTenonThickness
  expr: Constraints[19] = <<Parameters>>.WindowThickness
  sketch-geometry (8):
    g0: LineSegment StartX=305 StartY=32.5 StartZ=0 EndX=245 EndY=32.5 EndZ=0
    g1: LineSegment StartX=245 StartY=32.5 StartZ=0 EndX=245 EndY=0.5 EndZ=0
    g2: LineSegment StartX=245 StartY=0.5 StartZ=0 EndX=305 EndY=0.5 EndZ=0
    g3: LineSegment StartX=305 StartY=0.5 StartZ=0 EndX=305 EndY=32.5 EndZ=0
    g4: LineSegment StartX=305 StartY=-32.5 StartZ=0 EndX=305 EndY=-14.5 EndZ=0
    g5: LineSegment StartX=305 StartY=-14.5 StartZ=0 EndX=235 EndY=-14.5 EndZ=0
    g6: LineSegment StartX=235 StartY=-14.5 StartZ=0 EndX=235 EndY=-32.5 EndZ=0
    g7: LineSegment StartX=235 StartY=-32.5 StartZ=0 EndX=305 EndY=-32.5 EndZ=0
  constraints (22):
    c: Coincident(g0,g1)
    c: Coincident(g1,g2)
    c: Coincident(g2,g3)
    c: Coincident(g3,g0)
    c: Horizontal(g0)
    c: Horizontal(g2)
    c: Vertical(g1)
    c: Coincident(g4,g5)
    c: Coincident(g5,g6)
    c: Coincident(g6,g7)
    c: Coincident(g7,g4)
    c: Vertical(g4)
    c: Vertical(g6)
    c: Horizontal(g5)
    c: Vertical(g4,g2)
    c: DistanceX(g7,g7) = 70
    c: DistanceX(g0,g0) = 60
    c: DistanceY(g3,g3) = 32
    c: Distance(g2,g4) = 15
    c: DistanceY(g4,g0) = 65
    c: Tangent(g3,g-3)
    c: Tangent(g7,g-4)
FEATURE [PartDesign::Plane] DatumPlane032  label="DatumPlane left005"
  AttachmentOffset = pos=(0,0,305) rot=(0,0,1;0rad)
  AttachmentSupport = -> [X_Axis009]
  Length = 65
  MapMode = 4
  Placement = pos=(-305,0,0) rot=(0.57735,-0.57735,-0.57735;2.0944rad)
  ResizeMode = 1
  Width = 115
  expr: .AttachmentOffset.Base.z = <<Parameters>>.RailLength / 2
  expr: Length = <<Parameters>>.WindowThickness
  expr: Width = <<Parameters>>.RailTopWidth
FEATURE [PartDesign::Pocket] Pocket037  label="Tenon inner001"
  BaseFeature = -> Pad004
  Direction = (0,0,-1)
  Length = 5
  Length2 = 5
  Placement = pos=(0,-32.5,7.2e-15) rot=(1,0,0;1.5708rad)
  Profile = -> Sketch043
  ReferenceAxis = -> Sketch043 [N_Axis]
  Refine = true
  Suppressed = false
  Type = 1
FEATURE [Sketcher::SketchObject] Sketch044
  ArcFitTolerance = 0
  AttachmentSupport = -> [DatumPlane028]
  ExternalGeometry = -> [DatumPlane031,DatumPlane032]
  FullyConstrained = true
  MakeInternals = false
  MapMode = 5
  Placement = pos=(0,0,57.5) rot=(0,0,1;0rad)
  expr: Constraints[15] = <<Parameters>>.WindowThickness
  expr: Constraints[16] = <<Parameters>>.GlassRebateDepth
  expr: Constraints[17] = <<Parameters>>.RailTenonThickness
  expr: Constraints[18] = <<Parameters>>.StileOuterWidth
  expr: Constraints[19] = <<Parameters>>.StileOuterWidth - <<Parameters>>.GlassRebateWidth
  sketch-geometry (8):
    g0: LineSegment StartX=-305 StartY=32.5 StartZ=0 EndX=-305 EndY=0.5 EndZ=0
    g1: LineSegment StartX=-305 StartY=0.5 StartZ=0 EndX=-225 EndY=0.5 EndZ=0
    g2: LineSegment StartX=-225 StartY=0.5 StartZ=0 EndX=-225 EndY=32.5 EndZ=0
    g3: LineSegment StartX=-225 StartY=32.5 StartZ=0 EndX=-305 EndY=32.5 EndZ=0
    g4: LineSegment StartX=-305 StartY=-14.5 StartZ=0 EndX=-305 EndY=-32.5 EndZ=0
    g5: LineSegment StartX=-305 StartY=-32.5 StartZ=0 EndX=-215 EndY=-32.5 EndZ=0
    g6: LineSegment StartX=-215 StartY=-32.5 StartZ=0 EndX=-215 EndY=-14.5 EndZ=0
    g7: LineSegment StartX=-215 StartY=-14.5 StartZ=0 EndX=-305 EndY=-14.5 EndZ=0
  constraints (22):
    c: Coincident(g0,g1)
    c: Coincident(g1,g2)
    c: Coincident(g2,g3)
    c: Coincident(g3,g0)
    c: Vertical(g2)
    c: Horizontal(g1)
    c: Horizontal(g3)
    c: Coincident(g4,g5)
    c: Coincident(g5,g6)
    c: Coincident(g6,g7)
    c: Coincident(g7,g4)
    c: Vertical(g4)
    c: Vertical(g6)
    c: Horizontal(g7)
    c: Vertical(g4,g0)
    c: DistanceY(g4,g0) = 65
    c: DistanceY(g2,g2) = 32
    c: DistanceY(g4,g0) = 15
    c: DistanceX(g5,g5) = 90
    c: DistanceX(g3,g3) = 80
    c: Tangent(g0,g-4)
    c: Tangent(g5,g-3)
FEATURE [PartDesign::Pocket] Pocket038  label="Tenon outer001"
  BaseFeature = -> Pocket037
  Direction = (0,0,-1)
  Length = 5
  Length2 = 5
  Placement = pos=(0,-32.5,7.2e-15) rot=(1,0,0;1.5708rad)
  Profile = -> Sketch044
  ReferenceAxis = -> Sketch044 [N_Axis]
  Refine = true
  Suppressed = false
  Type = 1
FEATURE [Sketcher::SketchObject] Sketch045
  ArcFitTolerance = 0
  AttachmentSupport = -> [DatumPlane031]
  ExternalGeometry = -> [DatumPlane028,DatumPlane029]
  FullyConstrained = true
  MakeInternals = false
  MapMode = 5
  Placement = pos=(0,-32.5,7.2e-15) rot=(1,0,0;1.5708rad)
  expr: Constraints[6] = <<Parameters>>.RailTopWidth - <<Parameters>>.RailTopTenonWidth
  expr: Constraints[7] = <<Parameters>>.StileInnerWidth - <<Parameters>>.StileInnerHaunchDepth
  sketch-geometry (4):
    g0: LineSegment StartX=305 StartY=57.5 StartZ=0 EndX=255 EndY=57.5 EndZ=0
    g1: LineSegment StartX=255 StartY=57.5 StartZ=0 EndX=255 EndY=12.5 EndZ=0
    g2: LineSegment StartX=255 StartY=12.5 StartZ=0 EndX=305 EndY=12.5 EndZ=0
    g3: LineSegment StartX=305 StartY=12.5 StartZ=0 EndX=305 EndY=57.5 EndZ=0
  constraints (10):
    c: Coincident(g0,g1)
    c: Coincident(g1,g2)
    c: Coincident(g2,g3)
    c: Coincident(g3,g0)
    c: Horizontal(g2)
    c: Vertical(g1)
    c: DistanceY(g3,g3) = 45
    c: DistanceX(g0,g0) = 50
    c: Tangent(g3,g-4)
    c: Tangent(g0,g-3)
FEATURE [PartDesign::Pocket] Pocket039  label="Haunch inner"
  BaseFeature = -> Pocket038
  Direction = (0,1,-2e-16)
  Length = 5
  Length2 = 5
  Placement = pos=(0,-32.5,7.2e-15) rot=(1,0,0;1.5708rad)
  Profile = -> Sketch045
  ReferenceAxis = -> Sketch045 [N_Axis]
  Refine = true
  Suppressed = false
  Type = 1
FEATURE [Sketcher::SketchObject] Sketch046
  ArcFitTolerance = 0
  AttachmentSupport = -> [DatumPlane031]
  ExternalGeometry = -> [DatumPlane028,DatumPlane032]
  FullyConstrained = true
  MakeInternals = false
  MapMode = 5
  Placement = pos=(0,-32.5,7.2e-15) rot=(1,0,0;1.5708rad)
  expr: Constraints[6] = <<Parameters>>.StileOuterWidth - <<Parameters>>.StileOuterHaunchDepth
  expr: Constraints[7] = <<Parameters>>.RailTopWidth - <<Parameters>>.RailTopTenonWidth
  sketch-geometry (4):
    g0: LineSegment StartX=-305 StartY=57.5 StartZ=0 EndX=-305 EndY=12.5 EndZ=0
    g1: LineSegment StartX=-305 StartY=12.5 StartZ=0 EndX=-240 EndY=12.5 EndZ=0
    g2: LineSegment StartX=-240 StartY=12.5 StartZ=0 EndX=-240 EndY=57.5 EndZ=0
    g3: LineSegment StartX=-240 StartY=57.5 StartZ=0 EndX=-305 EndY=57.5 EndZ=0
  constraints (10):
    c: Coincident(g0,g1)
    c: Coincident(g1,g2)
    c: Coincident(g2,g3)
    c: Coincident(g3,g0)
    c: Vertical(g2)
    c: Horizontal(g1)
    c: DistanceX(g3,g3) = 65
    c: DistanceY(g0,g0) = 45
    c: Tangent(g3,g-3)
    c: Tangent(g-4,g0)
FEATURE [PartDesign::Pocket] Pocket040  label="Haunch outer"
  BaseFeature = -> Pocket039
  Direction = (0,1,-2e-16)
  Length = 5
  Length2 = 5
  Placement = pos=(0,-32.5,7.2e-15) rot=(1,0,0;1.5708rad)
  Profile = -> Sketch046
  ReferenceAxis = -> Sketch046 [N_Axis]
  Refine = true
  Suppressed = false
  Type = 1
FEATURE [PartDesign::Plane] DatumPlane033  label="DatumPlane bottom002"
  AttachmentOffset = pos=(0,0,57.5) rot=(0,0,1;0rad)
  AttachmentSupport = -> [X_Axis009]
  Length = 610
  MapMode = 2
  Placement = pos=(0,0,-57.5) rot=(0,1,0;3.14159rad)
  ResizeMode = 1
  Width = 65
  expr: .AttachmentOffset.Base.z = <<Parameters>>.RailTopWidth / 2
  expr: Length = <<Parameters>>.RailLength
  expr: Width = <<Parameters>>.WindowThickness
FEATURE [PartDesign::Plane] DatumPlane034  label="DatumPlane front005"
  AttachmentOffset = pos=(0,0,32.5) rot=(0,0,1;0rad)
  AttachmentSupport = -> [X_Axis009]
  Length = 610
  MapMode = 3
  Placement = pos=(0,32.5,-7.2e-15) rot=(0,0.707107,0.707107;3.14159rad)
  ResizeMode = 1
  Width = 115
  expr: .AttachmentOffset.Base.z = <<Parameters>>.WindowThickness / 2
  expr: Length = <<Parameters>>.RailLength
  expr: Width = <<Parameters>>.RailTopWidth
FEATURE [Sketcher::SketchObject] Sketch047
  ArcFitTolerance = 0
  AttachmentSupport = -> [DatumPlane033]
  ExternalGeometry = -> [DatumPlane034,DatumPlane029]
  FullyConstrained = true
  MakeInternals = false
  MapMode = 5
  Placement = pos=(0,0,-57.5) rot=(0,1,0;3.14159rad)
  expr: Constraints[10] = <<Parameters>>.GlassRebateDepth
  expr: Constraints[11] = <<Parameters>>.GlassOpeningWidth / 2 - <<Parameters>>.MuntinWidth / 2 + <<Parameters>>.StileInnerWidth
  expr: Constraints[8] = <<Parameters>>.MuntinWidth
  expr: Constraints[9] = <<Parameters>>.MuntinTenonThickness
  sketch-geometry (4):
    g0: LineSegment StartX=-25 StartY=0.5 StartZ=0 EndX=-25 EndY=-9.5 EndZ=0
    g1: LineSegment StartX=-25 StartY=-9.5 StartZ=0 EndX=5 EndY=-9.5 EndZ=0
    g2: LineSegment StartX=5 StartY=-9.5 StartZ=0 EndX=5 EndY=0.5 EndZ=0
    g3: LineSegment StartX=5 StartY=0.5 StartZ=0 EndX=-25 EndY=0.5 EndZ=0
  constraints (12):
    c: Coincident(g0,g1)
    c: Coincident(g1,g2)
    c: Coincident(g2,g3)
    c: Coincident(g3,g0)
    c: Vertical(g0)
    c: Vertical(g2)
    c: Horizontal(g1)
    c: Horizontal(g3)
    c: DistanceX(g1,g1) = 30
    c: DistanceY(g2,g2) = 10
    c: Distance(g2,g-3) = 32
    c: Distance(g0,g-4) = 280
FEATURE [PartDesign::Pocket] Pocket041  label="Muntin bar mortise001"
  BaseFeature = -> Pocket040
  Direction = (0,0,1)
  Length = 15
  Length2 = 5
  Placement = pos=(0,-32.5,7.2e-15) rot=(1,0,0;1.5708rad)
  Profile = -> Sketch047
  ReferenceAxis = -> Sketch047 [N_Axis]
  Refine = true
  Suppressed = false
  Type = 0
  expr: Length = <<Parameters>>.MuntinBarTenonLength
FEATURE [Sketcher::SketchObject] Sketch048
  ArcFitTolerance = 0
  AttachmentSupport = -> [DatumPlane033]
  ExternalGeometry = -> [DatumPlane034]
  FullyConstrained = true
  MakeInternals = false
  MapMode = 5
  Placement = pos=(0,0,-57.5) rot=(0,1,0;3.14159rad)
  expr: Constraints[10] = <<Parameters>>.GlassRebateDepth
  expr: Constraints[7] = <<Parameters>>.RailLength
  expr: Constraints[8] = <<Parameters>>.GlassRebateDepth
  sketch-geometry (4):
    g0: LineSegment StartX=-305 StartY=32.5 StartZ=0 EndX=-305 EndY=0.5 EndZ=0
    g1: LineSegment StartX=-305 StartY=0.5 StartZ=0 EndX=305 EndY=0.5 EndZ=0
    g2: LineSegment StartX=305 StartY=0.5 StartZ=0 EndX=305 EndY=32.5 EndZ=0
    g3: LineSegment StartX=305 StartY=32.5 StartZ=0 EndX=-305 EndY=32.5 EndZ=0
  constraints (11):
    c: Coincident(g0,g1)
    c: Coincident(g1,g2)
    c: Coincident(g2,g3)
    c: Coincident(g3,g0)
    c: Vertical(g0)
    c: Vertical(g2)
    c: Horizontal(g1)
    c: DistanceX(g3,g3) = 610
    c: DistanceY(g0,g0) = 32
    c: Symmetric(g0,g2,g-2)
    c: Distance(g0,g-3) = 32
FEATURE [PartDesign::Pocket] Pocket042  label="Glass rebate002"
  BaseFeature = -> Pocket041
  Direction = (0,0,1)
  Length = 10
  Length2 = 5
  Placement = pos=(0,-32.5,7.2e-15) rot=(1,0,0;1.5708rad)
  Profile = -> Sketch048
  ReferenceAxis = -> Sketch048 [N_Axis]
  Refine = true
  Suppressed = false
  Type = 0
  expr: Length = <<Parameters>>.GlassRebateWidth
FEATURE [Sketcher::SketchObject] Sketch049
  ArcFitTolerance = 0
  AttachmentSupport = -> [DatumPlane029]
  ExternalGeometry = -> [DatumPlane028,DatumPlane034]
  FullyConstrained = true
  MakeInternals = false
  MapMode = 5
  Placement = pos=(305,0,0) rot=(0.57735,0.57735,0.57735;2.0944rad)
  expr: Constraints[6] = <<Parameters>>.WindowFrameRebateWidth
  expr: Constraints[7] = <<Parameters>>.WindowFrameRebateDepth
  sketch-geometry (4):
    g0: LineSegment StartX=12.5 StartY=57.5 StartZ=0 EndX=12.5 EndY=32.5 EndZ=0
    g1: LineSegment StartX=12.5 StartY=32.5 StartZ=0 EndX=32.5 EndY=32.5 EndZ=0
    g2: LineSegment StartX=32.5 StartY=32.5 StartZ=0 EndX=32.5 EndY=57.5 EndZ=0
    g3: LineSegment StartX=32.5 StartY=57.5 StartZ=0 EndX=12.5 EndY=57.5 EndZ=0
  constraints (10):
    c: Coincident(g0,g1)
    c: Coincident(g1,g2)
    c: Coincident(g2,g3)
    c: Coincident(g3,g0)
    c: Vertical(g0)
    c: Horizontal(g1)
    c: DistanceX(g3,g3) = 20
    c: DistanceY(g2,g2) = 25
    c: Tangent(g2,g-4)
    c: Tangent(g3,g-3)
FEATURE [PartDesign::Pocket] Pocket043  label="Frame rebate opening top005"
  BaseFeature = -> Pocket042
  Direction = (-1,0,0)
  Length = 5
  Length2 = 5
  Placement = pos=(0,-32.5,7.2e-15) rot=(1,0,0;1.5708rad)
  Profile = -> Sketch049
  ReferenceAxis = -> Sketch049 [N_Axis]
  Refine = true
  Suppressed = false
  Type = 1
FEATURE [Sketcher::SketchObject] Sketch050
  ArcFitTolerance = 0
  AttachmentSupport = -> [DatumPlane029]
  ExternalGeometry = -> [DatumPlane034,DatumPlane028]
  FullyConstrained = true
  MakeInternals = false
  MapMode = 5
  Placement = pos=(305,0,0) rot=(0.57735,0.57735,0.57735;2.0944rad)
  expr: Constraints[6] = <<Parameters>>.WindowInnerLipWidth
  expr: Constraints[7] = <<Parameters>>.FrameThickness
  sketch-geometry (4):
    g0: LineSegment StartX=32.5 StartY=57.5 StartZ=0 EndX=-17.5 EndY=57.5 EndZ=0
    g1: LineSegment StartX=-17.5 StartY=57.5 StartZ=0 EndX=-17.5 EndY=42.5 EndZ=0
    g2: LineSegment StartX=-17.5 StartY=42.5 StartZ=0 EndX=32.5 EndY=42.5 EndZ=0
    g3: LineSegment StartX=32.5 StartY=42.5 StartZ=0 EndX=32.5 EndY=57.5 EndZ=0
  constraints (10):
    c: Coincident(g0,g1)
    c: Coincident(g1,g2)
    c: Coincident(g2,g3)
    c: Coincident(g3,g0)
    c: Horizontal(g2)
    c: Vertical(g1)
    c: DistanceY(g3,g3) = 15
    c: DistanceX(g0,g0) = 50
    c: Tangent(g0,g-4)
    c: Tangent(g3,g-3)
FEATURE [PartDesign::Pocket] Pocket044  label="Frame rebate lip top004"
  BaseFeature = -> Pocket043
  Direction = (-1,0,0)
  Length = 5
  Length2 = 5
  Placement = pos=(0,-32.5,7.2e-15) rot=(1,0,0;1.5708rad)
  Profile = -> Sketch050
  ReferenceAxis = -> Sketch050 [N_Axis]
  Refine = true
  Suppressed = false
  Type = 1
FEATURE [Sketcher::SketchObject] Sketch051
  ArcFitTolerance = 0
  AttachmentSupport = -> [DatumPlane028]
  ExternalGeometry = -> [DatumPlane034,DatumPlane032]
  FullyConstrained = true
  MakeInternals = false
  MapMode = 5
  Placement = pos=(0,0,57.5) rot=(0,0,1;0rad)
  expr: Constraints[6] = <<Parameters>>.WindowInnerLipWidth
  expr: Constraints[7] = <<Parameters>>.WindowThickness
  sketch-geometry (4):
    g0: LineSegment StartX=-305 StartY=32.5 StartZ=0 EndX=-305 EndY=-32.5 EndZ=0
    g1: LineSegment StartX=-305 StartY=-32.5 StartZ=0 EndX=-290 EndY=-32.5 EndZ=0
    g2: LineSegment StartX=-290 StartY=-32.5 StartZ=0 EndX=-290 EndY=32.5 EndZ=0
    g3: LineSegment StartX=-290 StartY=32.5 StartZ=0 EndX=-305 EndY=32.5 EndZ=0
  constraints (10):
    c: Coincident(g0,g1)
    c: Coincident(g1,g2)
    c: Coincident(g2,g3)
    c: Coincident(g3,g0)
    c: Vertical(g2)
    c: Horizontal(g1)
    c: DistanceX(g3,g3) = 15
    c: DistanceY(g0,g0) = 65
    c: Tangent(g3,g-3)
    c: Tangent(g0,g-4)
FEATURE [Sketcher::SketchObject] Sketch052
  ArcFitTolerance = 0
  AttachmentSupport = -> [DatumPlane028]
  ExternalGeometry = -> [DatumPlane029,DatumPlane031]
  FullyConstrained = true
  MakeInternals = false
  MapMode = 5
  Placement = pos=(0,0,57.5) rot=(0,0,1;0rad)
  expr: Constraints[6] = <<Parameters>>.IntersectionRebateDepth
  expr: Constraints[7] = <<Parameters>>.IntersectionRebateWidth
  sketch-geometry (4):
    g0: LineSegment StartX=305 StartY=-5.68e-14 StartZ=0 EndX=295 EndY=-5.68e-14 EndZ=0
    g1: LineSegment StartX=295 StartY=-5.68e-14 StartZ=0 EndX=295 EndY=-32.5 EndZ=0
    g2: LineSegment StartX=295 StartY=-32.5 StartZ=0 EndX=305 EndY=-32.5 EndZ=0
    g3: LineSegment StartX=305 StartY=-32.5 StartZ=0 EndX=305 EndY=-5.68e-14 EndZ=0
  constraints (10):
    c: Coincident(g0,g1)
    c: Coincident(g1,g2)
    c: Coincident(g2,g3)
    c: Coincident(g3,g0)
    c: Horizontal(g0)
    c: Vertical(g1)
    c: DistanceX(g2,g2) = 10
    c: DistanceY(g3,g3) = 32.5
    c: Tangent(g2,g-4)
    c: Tangent(g3,g-3)
FEATURE [PartDesign::Pocket] Pocket045  label="Frame rebate lip left"
  BaseFeature = -> Pocket044
  Direction = (0,0,-1)
  Length = 5
  Length2 = 5
  Placement = pos=(0,-32.5,7.2e-15) rot=(1,0,0;1.5708rad)
  Profile = -> Sketch051
  ReferenceAxis = -> Sketch051 [N_Axis]
  Refine = true
  Suppressed = false
  Type = 1
FEATURE [PartDesign::Pocket] Pocket046  label="Frame rebate intersection right"
  BaseFeature = -> Pocket045
  Direction = (0,0,-1)
  Length = 5
  Length2 = 5
  Placement = pos=(0,-32.5,7.2e-15) rot=(1,0,0;1.5708rad)
  Profile = -> Sketch052
  ReferenceAxis = -> Sketch052 [N_Axis]
  Refine = true
  Suppressed = false
  Type = 1
FEATURE [PartDesign::Body] Body009  label="Rail top left"
  AllowCompound = false
  Group = -> [DatumPlane028,DatumPlane029,DatumPlane031,DatumPlane032,DatumPlane033,DatumPlane034,Sketch042,Pad004,Sketch043,Pocket037,Sketch044,Pocket038,Sketch045,Pocket039,Sketch046,Pocket040,Sketch047,Pocket041,Sketch048,Pocket042,Sketch049,Pocket043,Sketch050,Pocket044,Sketch051,Sketch052,Pocket045,Pocket046]
  Origin = -> Origin009
  Tip = -> Pocket046
FEATURE [PartDesign::Plane] DatumPlane035  label="DatumPlane top007"
  AttachmentOffset = pos=(0,0,82.5) rot=(0,0,1;0rad)
  AttachmentSupport = -> [X_Axis010]
  Length = 610
  MapMode = 2
  Placement = pos=(0,0,82.5) rot=(0,0,1;0rad)
  ResizeMode = 1
  Width = 65
  expr: .AttachmentOffset.Base.z = <<Parameters>>.RailBottomWidth / 2
  expr: Length = <<Parameters>>.RailLength
  expr: Width = <<Parameters>>.WindowThickness
FEATURE [PartDesign::Plane] DatumPlane036  label="DatumPlane right006"
  AttachmentOffset = pos=(0,0,305) rot=(0,0,1;0rad)
  AttachmentSupport = -> [X_Axis010]
  Length = 65
  MapMode = 4
  Placement = pos=(305,0,0) rot=(0.57735,0.57735,0.57735;2.0944rad)
  ResizeMode = 1
  Width = 165
  expr: .AttachmentOffset.Base.z = <<Parameters>>.RailLength / 2
  expr: Length = <<Parameters>>.WindowThickness
  expr: Width = <<Parameters>>.RailBottomWidth
FEATURE [PartDesign::Plane] DatumPlane037  label="DatumPlane front006"
  AttachmentOffset = pos=(0,0,32.5) rot=(0,0,1;0rad)
  AttachmentSupport = -> [X_Axis010]
  Length = 610
  MapMode = 3
  Placement = pos=(0,-32.5,7.2e-15) rot=(1,0,0;1.5708rad)
  ResizeMode = 1
  Width = 165
  expr: .AttachmentOffset.Base.z = <<Parameters>>.WindowThickness / 2
  expr: Length = <<Parameters>>.RailLength
  expr: Width = <<Parameters>>.RailBottomWidth
FEATURE [PartDesign::Plane] DatumPlane038  label="DatumPlane left006"
  AttachmentOffset = pos=(0,0,305) rot=(0,0,1;0rad)
  AttachmentSupport = -> [X_Axis010]
  Length = 65
  MapMode = 4
  Placement = pos=(-305,0,0) rot=(0.57735,-0.57735,-0.57735;2.0944rad)
  ResizeMode = 1
  Width = 165
  expr: .AttachmentOffset.Base.z = <<Parameters>>.RailLength / 2
  expr: Length = <<Parameters>>.WindowThickness
  expr: Width = <<Parameters>>.RailBottomWidth
FEATURE [PartDesign::Plane] DatumPlane039  label="DatumPlane bottom003"
  AttachmentOffset = pos=(0,0,82.5) rot=(0,0,1;0rad)
  AttachmentSupport = -> [X_Axis010]
  Length = 610
  MapMode = 2
  Placement = pos=(0,0,-82.5) rot=(0,1,0;3.14159rad)
  ResizeMode = 1
  Width = 65
  expr: .AttachmentOffset.Base.z = <<Parameters>>.RailBottomWidth / 2
  expr: Length = <<Parameters>>.RailLength
  expr: Width = <<Parameters>>.WindowThickness
FEATURE [PartDesign::Plane] DatumPlane040  label="DatumPlane front007"
  AttachmentOffset = pos=(0,0,32.5) rot=(0,0,1;0rad)
  AttachmentSupport = -> [X_Axis010]
  Length = 610
  MapMode = 3
  Placement = pos=(0,32.5,-7.2e-15) rot=(0,0.707107,0.707107;3.14159rad)
  ResizeMode = 1
  Width = 165
  expr: .AttachmentOffset.Base.z = <<Parameters>>.WindowThickness / 2
  expr: Length = <<Parameters>>.RailLength
  expr: Width = <<Parameters>>.RailBottomWidth
FEATURE [Sketcher::SketchObject] Sketch053
  ArcFitTolerance = 0
  AttachmentSupport = -> [DatumPlane037]
  FullyConstrained = true
  MakeInternals = false
  MapMode = 5
  Placement = pos=(0,-32.5,7.2e-15) rot=(1,0,0;1.5708rad)
  expr: Constraints[10] = <<Parameters>>.RailLength
  expr: Constraints[11] = <<Parameters>>.RailBottomWidth
  sketch-geometry (5):
    g0: LineSegment StartX=-305 StartY=82.5 StartZ=0 EndX=-305 EndY=-82.5 EndZ=0
    g1: LineSegment StartX=-305 StartY=-82.5 StartZ=0 EndX=305 EndY=-82.5 EndZ=0
    g2: LineSegment StartX=305 StartY=-82.5 StartZ=0 EndX=305 EndY=82.5 EndZ=0
    g3: LineSegment StartX=305 StartY=82.5 StartZ=0 EndX=-305 EndY=82.5 EndZ=0
    g4: GeomPoint [constr] X=0 Y=0 Z=0
  constraints (12):
    c: Coincident(g0,g1)
    c: Coincident(g1,g2)
    c: Coincident(g2,g3)
    c: Coincident(g3,g0)
    c: Vertical(g0)
    c: Vertical(g2)
    c: Horizontal(g1)
    c: Horizontal(g3)
    c: Symmetric(g2,g0,g4)
    c: Coincident(g4,g-1)
    c: DistanceX(g3,g3) = 610
    c: DistanceY(g2,g2) = 165
FEATURE [PartDesign::Pad] Pad005  label="Stock005"
  Direction = (0,-1,2e-16)
  Length = 65
  Length2 = 10
  Placement = pos=(0,-32.5,7.2e-15) rot=(1,0,0;1.5708rad)
  Profile = -> Sketch053
  ReferenceAxis = -> Sketch053 [N_Axis]
  Refine = true
  Reversed = true
  Suppressed = false
  Type = 0
  expr: Length = <<Parameters>>.WindowThickness
FEATURE [Sketcher::SketchObject] Sketch054
  ArcFitTolerance = 0
  AttachmentSupport = -> [DatumPlane035]
  ExternalGeometry = -> [DatumPlane036,DatumPlane037]
  FullyConstrained = true
  MakeInternals = false
  MapMode = 5
  Placement = pos=(0,0,82.5) rot=(0,0,1;0rad)
  expr: Constraints[15] = <<Parameters>>.StileInnerWidth
  expr: Constraints[16] = <<Parameters>>.StileInnerWidth - <<Parameters>>.GlassRebateWidth
  expr: Constraints[17] = <<Parameters>>.GlassRebateDepth
  expr: Constraints[18] = <<Parameters>>.RailTenonThickness
  expr: Constraints[19] = <<Parameters>>.WindowThickness
  sketch-geometry (8):
    g0: LineSegment StartX=305 StartY=32.5 StartZ=0 EndX=245 EndY=32.5 EndZ=0
    g1: LineSegment StartX=245 StartY=32.5 StartZ=0 EndX=245 EndY=0.5 EndZ=0
    g2: LineSegment StartX=245 StartY=0.5 StartZ=0 EndX=305 EndY=0.5 EndZ=0
    g3: LineSegment StartX=305 StartY=0.5 StartZ=0 EndX=305 EndY=32.5 EndZ=0
    g4: LineSegment StartX=305 StartY=-32.5 StartZ=0 EndX=305 EndY=-14.5 EndZ=0
    g5: LineSegment StartX=305 StartY=-14.5 StartZ=0 EndX=235 EndY=-14.5 EndZ=0
    g6: LineSegment StartX=235 StartY=-14.5 StartZ=0 EndX=235 EndY=-32.5 EndZ=0
    g7: LineSegment StartX=235 StartY=-32.5 StartZ=0 EndX=305 EndY=-32.5 EndZ=0
  constraints (22):
    c: Coincident(g0,g1)
    c: Coincident(g1,g2)
    c: Coincident(g2,g3)
    c: Coincident(g3,g0)
    c: Horizontal(g0)
    c: Horizontal(g2)
    c: Vertical(g1)
    c: Coincident(g4,g5)
    c: Coincident(g5,g6)
    c: Coincident(g6,g7)
    c: Coincident(g7,g4)
    c: Vertical(g4)
    c: Vertical(g6)
    c: Horizontal(g5)
    c: Vertical(g4,g2)
    c: DistanceX(g7,g7) = 70
    c: DistanceX(g0,g0) = 60
    c: DistanceY(g3,g3) = 32
    c: Distance(g2,g4) = 15
    c: DistanceY(g4,g0) = 65
    c: Tangent(g3,g-3)
    c: Tangent(g7,g-4)
FEATURE [PartDesign::Pocket] Pocket047  label="Tenon inner002"
  BaseFeature = -> Pad005
  Direction = (0,0,-1)
  Length = 5
  Length2 = 5
  Placement = pos=(0,-32.5,7.2e-15) rot=(1,0,0;1.5708rad)
  Profile = -> Sketch054
  ReferenceAxis = -> Sketch054 [N_Axis]
  Refine = true
  Suppressed = false
  Type = 1
FEATURE [Sketcher::SketchObject] Sketch055
  ArcFitTolerance = 0
  AttachmentSupport = -> [DatumPlane035]
  ExternalGeometry = -> [DatumPlane037,DatumPlane038]
  FullyConstrained = true
  MakeInternals = false
  MapMode = 5
  Placement = pos=(0,0,82.5) rot=(0,0,1;0rad)
  expr: Constraints[15] = <<Parameters>>.WindowThickness
  expr: Constraints[16] = <<Parameters>>.GlassRebateDepth
  expr: Constraints[17] = <<Parameters>>.RailTenonThickness
  expr: Constraints[18] = <<Parameters>>.StileOuterWidth
  expr: Constraints[19] = <<Parameters>>.StileOuterWidth - <<Parameters>>.GlassRebateWidth
  sketch-geometry (8):
    g0: LineSegment StartX=-305 StartY=32.5 StartZ=0 EndX=-305 EndY=0.5 EndZ=0
    g1: LineSegment StartX=-305 StartY=0.5 StartZ=0 EndX=-225 EndY=0.5 EndZ=0
    g2: LineSegment StartX=-225 StartY=0.5 StartZ=0 EndX=-225 EndY=32.5 EndZ=0
    g3: LineSegment StartX=-225 StartY=32.5 StartZ=0 EndX=-305 EndY=32.5 EndZ=0
    g4: LineSegment StartX=-305 StartY=-14.5 StartZ=0 EndX=-305 EndY=-32.5 EndZ=0
    g5: LineSegment StartX=-305 StartY=-32.5 StartZ=0 EndX=-215 EndY=-32.5 EndZ=0
    g6: LineSegment StartX=-215 StartY=-32.5 StartZ=0 EndX=-215 EndY=-14.5 EndZ=0
    g7: LineSegment StartX=-215 StartY=-14.5 StartZ=0 EndX=-305 EndY=-14.5 EndZ=0
  constraints (22):
    c: Coincident(g0,g1)
    c: Coincident(g1,g2)
    c: Coincident(g2,g3)
    c: Coincident(g3,g0)
    c: Vertical(g2)
    c: Horizontal(g1)
    c: Horizontal(g3)
    c: Coincident(g4,g5)
    c: Coincident(g5,g6)
    c: Coincident(g6,g7)
    c: Coincident(g7,g4)
    c: Vertical(g4)
    c: Vertical(g6)
    c: Horizontal(g7)
    c: Vertical(g4,g0)
    c: DistanceY(g4,g0) = 65
    c: DistanceY(g2,g2) = 32
    c: DistanceY(g4,g0) = 15
    c: DistanceX(g5,g5) = 90
    c: DistanceX(g3,g3) = 80
    c: Tangent(g0,g-4)
    c: Tangent(g5,g-3)
FEATURE [PartDesign::Pocket] Pocket048  label="Tenon outer002"
  BaseFeature = -> Pocket047
  Direction = (0,0,-1)
  Length = 5
  Length2 = 5
  Placement = pos=(0,-32.5,7.2e-15) rot=(1,0,0;1.5708rad)
  Profile = -> Sketch055
  ReferenceAxis = -> Sketch055 [N_Axis]
  Refine = true
  Suppressed = false
  Type = 1
FEATURE [Sketcher::SketchObject] Sketch056
  ArcFitTolerance = 0
  AttachmentSupport = -> [DatumPlane037]
  ExternalGeometry = -> [DatumPlane036,DatumPlane039]
  FullyConstrained = true
  MakeInternals = false
  MapMode = 5
  Placement = pos=(0,-32.5,7.2e-15) rot=(1,0,0;1.5708rad)
  expr: Constraints[5] = <<Parameters>>.RailBottomWidth - <<Parameters>>.RailBottomTenonWidth
  expr: Constraints[6] = <<Parameters>>.StileInnerWidth - <<Parameters>>.StileInnerHaunchDepth
  sketch-geometry (4):
    g0: LineSegment StartX=305 StartY=-17.5 StartZ=0 EndX=255 EndY=-17.5 EndZ=0
    g1: LineSegment StartX=255 StartY=-17.5 StartZ=0 EndX=255 EndY=-82.5 EndZ=0
    g2: LineSegment StartX=255 StartY=-82.5 StartZ=0 EndX=305 EndY=-82.5 EndZ=0
    g3: LineSegment StartX=305 StartY=-82.5 StartZ=0 EndX=305 EndY=-17.5 EndZ=0
  constraints (10):
    c: Coincident(g0,g1)
    c: Coincident(g1,g2)
    c: Coincident(g2,g3)
    c: Coincident(g3,g0)
    c: Vertical(g1)
    c: DistanceY(g3,g3) = 65
    c: DistanceX(g0,g0) = 50
    c: Tangent(g3,g-3)
    c: Horizontal(g0,g0)
    c: Tangent(g2,g-4)
FEATURE [PartDesign::Pocket] Pocket049  label="Haunch inner001"
  BaseFeature = -> Pocket048
  Direction = (0,1,-2e-16)
  Length = 5
  Length2 = 5
  Placement = pos=(0,-32.5,7.2e-15) rot=(1,0,0;1.5708rad)
  Profile = -> Sketch056
  ReferenceAxis = -> Sketch056 [N_Axis]
  Refine = true
  Suppressed = false
  Type = 1
FEATURE [Sketcher::SketchObject] Sketch057
  ArcFitTolerance = 0
  AttachmentSupport = -> [DatumPlane037]
  ExternalGeometry = -> [DatumPlane038,DatumPlane039]
  FullyConstrained = true
  MakeInternals = false
  MapMode = 5
  Placement = pos=(0,-32.5,7.2e-15) rot=(1,0,0;1.5708rad)
  expr: Constraints[5] = <<Parameters>>.StileOuterWidth - <<Parameters>>.StileOuterHaunchDepth
  expr: Constraints[6] = <<Parameters>>.RailBottomWidth - <<Parameters>>.RailBottomTenonWidth
  sketch-geometry (4):
    g0: LineSegment StartX=-305 StartY=-17.5 StartZ=0 EndX=-305 EndY=-82.5 EndZ=0
    g1: LineSegment StartX=-305 StartY=-82.5 StartZ=0 EndX=-240 EndY=-82.5 EndZ=0
    g2: LineSegment StartX=-240 StartY=-82.5 StartZ=0 EndX=-240 EndY=-17.5 EndZ=0
    g3: LineSegment StartX=-240 StartY=-17.5 StartZ=0 EndX=-305 EndY=-17.5 EndZ=0
  constraints (10):
    c: Coincident(g0,g1)
    c: Coincident(g1,g2)
    c: Coincident(g2,g3)
    c: Coincident(g3,g0)
    c: Vertical(g2)
    c: DistanceX(g3,g3) = 65
    c: DistanceY(g0,g0) = 65
    c: Tangent(g-3,g0)
    c: Horizontal(g0,g2)
    c: Tangent(g1,g-4)
FEATURE [PartDesign::Pocket] Pocket050  label="Haunch outer001"
  BaseFeature = -> Pocket049
  Direction = (0,1,-2e-16)
  Length = 5
  Length2 = 5
  Placement = pos=(0,-32.5,7.2e-15) rot=(1,0,0;1.5708rad)
  Profile = -> Sketch057
  ReferenceAxis = -> Sketch057 [N_Axis]
  Refine = true
  Suppressed = false
  Type = 1
FEATURE [Sketcher::SketchObject] Sketch059
  ArcFitTolerance = 0
  AttachmentSupport = -> [DatumPlane035]
  ExternalGeometry = -> [DatumPlane040]
  FullyConstrained = true
  MakeInternals = false
  MapMode = 5
  Placement = pos=(0,0,82.5) rot=(0,0,1;0rad)
  expr: Constraints[10] = <<Parameters>>.GlassRebateDepth
  expr: Constraints[7] = <<Parameters>>.RailLength
  expr: Constraints[8] = <<Parameters>>.GlassRebateDepth
  sketch-geometry (4):
    g0: LineSegment StartX=-305 StartY=32.5 StartZ=0 EndX=-305 EndY=0.5 EndZ=0
    g1: LineSegment StartX=-305 StartY=0.5 StartZ=0 EndX=305 EndY=0.5 EndZ=0
    g2: LineSegment StartX=305 StartY=0.5 StartZ=0 EndX=305 EndY=32.5 EndZ=0
    g3: LineSegment StartX=305 StartY=32.5 StartZ=0 EndX=-305 EndY=32.5 EndZ=0
  constraints (11):
    c: Coincident(g0,g1)
    c: Coincident(g1,g2)
    c: Coincident(g2,g3)
    c: Coincident(g3,g0)
    c: Vertical(g0)
    c: Vertical(g2)
    c: Horizontal(g1)
    c: DistanceX(g3,g3) = 610
    c: DistanceY(g0,g0) = 32
    c: Symmetric(g0,g2,g-2)
    c: Distance(g0,g-3) = 32
FEATURE [PartDesign::Pocket] Pocket052  label="Glass rebate003"
  BaseFeature = -> Pocket050
  Direction = (0,0,-1)
  Length = 10
  Length2 = 5
  Placement = pos=(0,-32.5,7.2e-15) rot=(1,0,0;1.5708rad)
  Profile = -> Sketch059
  ReferenceAxis = -> Sketch059 [N_Axis]
  Refine = true
  Suppressed = false
  Type = 0
  expr: Length = <<Parameters>>.GlassRebateWidth
FEATURE [Sketcher::SketchObject] Sketch060
  ArcFitTolerance = 0
  AttachmentSupport = -> [DatumPlane036]
  ExternalGeometry = -> [DatumPlane040,DatumPlane039]
  FullyConstrained = true
  MakeInternals = false
  MapMode = 5
  Placement = pos=(305,0,0) rot=(0.57735,0.57735,0.57735;2.0944rad)
  expr: Constraints[5] = <<Parameters>>.WindowFrameRebateWidth
  expr: Constraints[6] = <<Parameters>>.WindowFrameRebateDepth
  sketch-geometry (4):
    g0: LineSegment StartX=12.5 StartY=-57.5 StartZ=0 EndX=12.5 EndY=-82.5 EndZ=0
    g1: LineSegment StartX=12.5 StartY=-82.5 StartZ=0 EndX=32.5 EndY=-82.5 EndZ=0
    g2: LineSegment StartX=32.5 StartY=-82.5 StartZ=0 EndX=32.5 EndY=-57.5 EndZ=0
    g3: LineSegment StartX=32.5 StartY=-57.5 StartZ=0 EndX=12.5 EndY=-57.5 EndZ=0
  constraints (10):
    c: Coincident(g0,g1)
    c: Coincident(g1,g2)
    c: Coincident(g2,g3)
    c: Coincident(g3,g0)
    c: Vertical(g0)
    c: DistanceX(g3,g3) = 20
    c: DistanceY(g2,g2) = 25
    c: Tangent(g2,g-3)
    c: Tangent(g1,g-4)
    c: Horizontal(g0,g2)
FEATURE [PartDesign::Pocket] Pocket053  label="Frame rebate opening top006"
  BaseFeature = -> Pocket052
  Direction = (-1,0,0)
  Length = 5
  Length2 = 5
  Placement = pos=(0,-32.5,7.2e-15) rot=(1,0,0;1.5708rad)
  Profile = -> Sketch060
  ReferenceAxis = -> Sketch060 [N_Axis]
  Refine = true
  Suppressed = false
  Type = 1
FEATURE [Sketcher::SketchObject] Sketch061
  ArcFitTolerance = 0
  AttachmentSupport = -> [DatumPlane036]
  ExternalGeometry = -> [DatumPlane040,DatumPlane039]
  FullyConstrained = true
  MakeInternals = false
  MapMode = 5
  Placement = pos=(305,0,0) rot=(0.57735,0.57735,0.57735;2.0944rad)
  expr: Constraints[5] = <<Parameters>>.WindowInnerLipWidth
  expr: Constraints[6] = <<Parameters>>.FrameThickness
  sketch-geometry (4):
    g0: LineSegment StartX=32.5 StartY=-67.5 StartZ=0 EndX=-17.5 EndY=-67.5 EndZ=0
    g1: LineSegment StartX=-17.5 StartY=-67.5 StartZ=0 EndX=-17.5 EndY=-82.5 EndZ=0
    g2: LineSegment StartX=-17.5 StartY=-82.5 StartZ=0 EndX=32.5 EndY=-82.5 EndZ=0
    g3: LineSegment StartX=32.5 StartY=-82.5 StartZ=0 EndX=32.5 EndY=-67.5 EndZ=0
  constraints (10):
    c: Coincident(g0,g1)
    c: Coincident(g1,g2)
    c: Coincident(g2,g3)
    c: Coincident(g3,g0)
    c: Vertical(g1)
    c: DistanceY(g3,g3) = 15
    c: DistanceX(g0,g0) = 50
    c: Tangent(g3,g-3)
    c: Horizontal(g0,g0)
    c: Tangent(g2,g-4)
FEATURE [PartDesign::Pocket] Pocket054  label="Frame rebate lip top005"
  BaseFeature = -> Pocket053
  Direction = (-1,0,0)
  Length = 5
  Length2 = 5
  Placement = pos=(0,-32.5,7.2e-15) rot=(1,0,0;1.5708rad)
  Profile = -> Sketch061
  ReferenceAxis = -> Sketch061 [N_Axis]
  Refine = true
  Suppressed = false
  Type = 1
FEATURE [Sketcher::SketchObject] Sketch062
  ArcFitTolerance = 0
  AttachmentSupport = -> [DatumPlane035]
  ExternalGeometry = -> [DatumPlane040,DatumPlane038]
  FullyConstrained = true
  MakeInternals = false
  MapMode = 5
  Placement = pos=(0,0,82.5) rot=(0,0,1;0rad)
  expr: Constraints[6] = <<Parameters>>.WindowInnerLipWidth
  expr: Constraints[7] = <<Parameters>>.WindowThickness
  sketch-geometry (4):
    g0: LineSegment StartX=-305 StartY=32.5 StartZ=0 EndX=-305 EndY=-32.5 EndZ=0
    g1: LineSegment StartX=-305 StartY=-32.5 StartZ=0 EndX=-290 EndY=-32.5 EndZ=0
    g2: LineSegment StartX=-290 StartY=-32.5 StartZ=0 EndX=-290 EndY=32.5 EndZ=0
    g3: LineSegment StartX=-290 StartY=32.5 StartZ=0 EndX=-305 EndY=32.5 EndZ=0
  constraints (10):
    c: Coincident(g0,g1)
    c: Coincident(g1,g2)
    c: Coincident(g2,g3)
    c: Coincident(g3,g0)
    c: Vertical(g2)
    c: Horizontal(g1)
    c: DistanceX(g3,g3) = 15
    c: DistanceY(g0,g0) = 65
    c: Tangent(g3,g-3)
    c: Tangent(g0,g-4)
FEATURE [PartDesign::Pocket] Pocket055  label="Frame rebate lip left002"
  BaseFeature = -> Pocket054
  Direction = (0,0,-1)
  Length = 5
  Length2 = 5
  Placement = pos=(0,-32.5,7.2e-15) rot=(1,0,0;1.5708rad)
  Profile = -> Sketch062
  ReferenceAxis = -> Sketch062 [N_Axis]
  Refine = true
  Suppressed = false
  Type = 1
FEATURE [Sketcher::SketchObject] Sketch063
  ArcFitTolerance = 0
  AttachmentSupport = -> [DatumPlane035]
  ExternalGeometry = -> [DatumPlane036,DatumPlane037]
  FullyConstrained = true
  MakeInternals = false
  MapMode = 5
  Placement = pos=(0,0,82.5) rot=(0,0,1;0rad)
  expr: Constraints[6] = <<Parameters>>.IntersectionRebateDepth
  expr: Constraints[7] = <<Parameters>>.IntersectionRebateWidth
  sketch-geometry (4):
    g0: LineSegment StartX=305 StartY=-5.68e-14 StartZ=0 EndX=295 EndY=-5.68e-14 EndZ=0
    g1: LineSegment StartX=295 StartY=-5.68e-14 StartZ=0 EndX=295 EndY=-32.5 EndZ=0
    g2: LineSegment StartX=295 StartY=-32.5 StartZ=0 EndX=305 EndY=-32.5 EndZ=0
    g3: LineSegment StartX=305 StartY=-32.5 StartZ=0 EndX=305 EndY=-5.68e-14 EndZ=0
  constraints (10):
    c: Coincident(g0,g1)
    c: Coincident(g1,g2)
    c: Coincident(g2,g3)
    c: Coincident(g3,g0)
    c: Horizontal(g0)
    c: Vertical(g1)
    c: DistanceX(g2,g2) = 10
    c: DistanceY(g3,g3) = 32.5
    c: Tangent(g2,g-4)
    c: Tangent(g3,g-3)
FEATURE [PartDesign::Pocket] Pocket056  label="Frame rebate intersection right001"
  BaseFeature = -> Pocket055
  Direction = (0,0,-1)
  Length = 5
  Length2 = 5
  Placement = pos=(0,-32.5,7.2e-15) rot=(1,0,0;1.5708rad)
  Profile = -> Sketch063
  ReferenceAxis = -> Sketch063 [N_Axis]
  Refine = true
  Suppressed = false
  Type = 1
FEATURE [PartDesign::Body] Body010  label="Rail bottom left"
  AllowCompound = false
  Group = -> [DatumPlane035,DatumPlane036,DatumPlane037,DatumPlane038,DatumPlane039,DatumPlane040,Sketch053,Pad005,Sketch054,Pocket047,Sketch055,Pocket048,Sketch056,Pocket049,Sketch057,Pocket050,Sketch059,Pocket052,Sketch060,Pocket053,Sketch061,Pocket054,Sketch062,Sketch063,Pocket055,Pocket056]
  Origin = -> Origin010
  Tip = -> Pocket056
FEATURE [PartDesign::SubShapeBinder] Binder004  label="Rail top left binder"
  BindCopyOnChange = 0
  BindMode = 0
  ClaimChildren = false
  Context = -> Body009 [Binder004.]
  Fuse = false
  MakeFace = true
  OffsetFill = false
  OffsetIntersection = false
  OffsetJoinType = 0
  OffsetOpenResult = false
  PartialLoad = false
  Refine = true
  Relative = true
  Support = -> [Pocket045]
  _Version = 2
FEATURE [Part::Mirroring] Part__Mirroring004  label="Rail top right (Mirror #5)"
  Base = (0,0,0)
  Normal = (1,0,0)
  Source = -> Binder004
FEATURE [PartDesign::FeatureBase] BaseFeature005
  BaseFeature = -> Part__Mirroring004
  Suppressed = false
FEATURE [PartDesign::Body] Body011  label="Rail top right"
  AllowCompound = false
  BaseFeature = -> Part__Mirroring004
  Group = -> [BaseFeature005]
  Origin = -> Origin011
  Tip = -> BaseFeature005
FEATURE [PartDesign::SubShapeBinder] Binder005  label="Rail bottom left binder"
  BindCopyOnChange = 0
  BindMode = 0
  ClaimChildren = false
  Context = -> Body011 [Binder005.]
  Fuse = false
  MakeFace = true
  OffsetFill = false
  OffsetIntersection = false
  OffsetJoinType = 0
  OffsetOpenResult = false
  PartialLoad = false
  Refine = true
  Relative = true
  Support = -> [Body010[Pocket055.]]
  _Version = 2
FEATURE [Part::Mirroring] Part__Mirroring005  label="Rail bottom right (Mirror #6)"
  Base = (0,0,0)
  Normal = (1,0,0)
  Source = -> Binder005
FEATURE [App::DocumentObjectGroup] Group001  label="Artifacts"
  Group = -> [Part__Mirroring,Part__Mirroring001,Part__Mirroring002,Part__Mirroring003,Part__Mirroring004,Part__Mirroring005]
FEATURE [PartDesign::FeatureBase] BaseFeature006
  BaseFeature = -> Part__Mirroring005
  Suppressed = false
FEATURE [PartDesign::Body] Body012  label="Rail bottom right"
  AllowCompound = false
  BaseFeature = -> Part__Mirroring005
  Group = -> [BaseFeature006]
  Origin = -> Origin012
  Tip = -> BaseFeature006
FEATURE [Sketcher::SketchObject] Sketch064  label="FrameSketch"
  ArcFitTolerance = 0
  AttachmentSupport = -> [XZ_Plane013]
  FullyConstrained = true
  MakeInternals = false
  MapMode = 5
  Placement = pos=(0,0,0) rot=(1,0,0;1.5708rad)
  expr: .Constraints.OpeningHeigth = <<Parameters>>.StileLength - <<Parameters>>.WindowFrameRebateDepth * 2
  expr: .Constraints.OpeningWidth = <<Parameters>>.RailLength * 2 - <<Parameters>>.WindowFrameRebateDepth * 2 - <<Parameters>>.IntersectionRebateDepth
  expr: Constraints[22] = .Constraints.OpeningHeigth + 70 mm * 2
  expr: Constraints[23] = .Constraints.OpeningWidth + 70 mm * 2
  sketch-geometry (10):
    g0: LineSegment StartX=-650 StartY=980 StartZ=0 EndX=-650 EndY=-980 EndZ=0
    g1: LineSegment StartX=-650 StartY=-980 StartZ=0 EndX=650 EndY=-980 EndZ=0
    g2: LineSegment StartX=650 StartY=-980 StartZ=0 EndX=650 EndY=980 EndZ=0
    g3: LineSegment StartX=650 StartY=980 StartZ=0 EndX=-650 EndY=980 EndZ=0
    g4: GeomPoint [constr] X=2.96e-14 Y=2.2e-15 Z=0
    g5: LineSegment StartX=-580 StartY=910 StartZ=0 EndX=-580 EndY=-910 EndZ=0
    g6: LineSegment StartX=-580 StartY=-910 StartZ=0 EndX=580 EndY=-910 EndZ=0
    g7: LineSegment StartX=580 StartY=-910 StartZ=0 EndX=580 EndY=910 EndZ=0
    g8: LineSegment StartX=580 StartY=910 StartZ=0 EndX=-580 EndY=910 EndZ=0
    g9: GeomPoint [constr] X=2.96e-14 Y=2.2e-15 Z=0
  constraints (24):
    c: Coincident(g0,g1)
    c: Coincident(g1,g2)
    c: Coincident(g2,g3)
    c: Coincident(g3,g0)
    c: Vertical(g0)
    c: Vertical(g2)
    c: Horizontal(g1)
    c: Horizontal(g3)
    c: Symmetric(g2,g0,g4)
    c: Coincident(g4,g-1)
    c: Coincident(g5,g6)
    c: Coincident(g6,g7)
    c: Coincident(g7,g8)
    c: Coincident(g8,g5)
    c: Vertical(g5)
    c: Vertical(g7)
    c: Horizontal(g6)
    c: Horizontal(g8)
    c: Symmetric(g7,g5,g9)
    c: Coincident(g9,g4)
    c: DistanceY(g5,g5) = 1820  'OpeningHeigth'
    c: DistanceX(g6,g6) = 1160  'OpeningWidth'
    c: DistanceY(g0,g0) = 1960
    c: DistanceX(g1,g1) = 1300
FEATURE [PartDesign::Pad] Pad006  label="Frame001"
  Direction = (0,-1,2e-16)
  Length = 50
  Length2 = 10
  Placement = pos=(0,0,0) rot=(1,0,0;1.5708rad)
  Profile = -> Sketch064
  ReferenceAxis = -> Sketch064 [N_Axis]
  Refine = true
  Suppressed = false
  Type = 0
  expr: Length = <<Parameters>>.FrameThickness
FEATURE [Sketcher::SketchObject] Sketch065
  ArcFitTolerance = 0
  AttachmentSupport = -> [Pad006]
  FullyConstrained = true
  MakeInternals = false
  MapMode = 5
  Placement = pos=(0,-50,0) rot=(1,0,0;1.5708rad)
  expr: Constraints[10] = <<FrameSketch>>.Constraints.OpeningWidth + 2 * <<Parameters>>.IntersectionRebateDepth
  expr: Constraints[11] = <<FrameSketch>>.Constraints.OpeningHeigth + 2 * <<Parameters>>.IntersectionRebateDepth
  sketch-geometry (5):
    g0: LineSegment StartX=-590 StartY=920 StartZ=0 EndX=-590 EndY=-920 EndZ=0
    g1: LineSegment StartX=-590 StartY=-920 StartZ=0 EndX=590 EndY=-920 EndZ=0
    g2: LineSegment StartX=590 StartY=-920 StartZ=0 EndX=590 EndY=920 EndZ=0
    g3: LineSegment StartX=590 StartY=920 StartZ=0 EndX=-590 EndY=920 EndZ=0
    g4: GeomPoint [constr] X=0 Y=0 Z=0
  constraints (12):
    c: Coincident(g0,g1)
    c: Coincident(g1,g2)
    c: Coincident(g2,g3)
    c: Coincident(g3,g0)
    c: Vertical(g0)
    c: Vertical(g2)
    c: Horizontal(g1)
    c: Horizontal(g3)
    c: Symmetric(g2,g0,g4)
    c: Coincident(g4,g-1)
    c: DistanceX(g3,g3) = 1180
    c: DistanceY(g0,g0) = 1840
FEATURE [PartDesign::Pocket] Pocket057
  BaseFeature = -> Pad006
  Direction = (0,1,-2e-16)
  Length = 30
  Length2 = 5
  Placement = pos=(0,0,0) rot=(1,0,0;1.5708rad)
  Profile = -> Sketch065
  ReferenceAxis = -> Sketch065 [N_Axis]
  Refine = true
  Suppressed = false
  Type = 0
  expr: Length = <<Parameters>>.FrameThickness - <<Parameters>>.WindowFrameRebateWidth
FEATURE [PartDesign::Body] Body013  label="Frame"
  AllowCompound = false
  Group = -> [Sketch064,Pad006,Sketch065,Pocket057]
  Origin = -> Origin013
  Tip = -> Pocket057
FEATURE [App::Link] Frame  label="Frame002"
  LinkedObject = -> Body013
FEATURE [App::FeaturePython] GroundedJoint  # Assembly grounded joint (typed FeaturePython)
  ObjectToGround = -> Frame
FEATURE [App::Link] Stile_outer_left  label="Stile outer left001"
  LinkPlacement = pos=(-560,-32.5,0) rot=(0,0,1;0rad)
  LinkedObject = -> Body001
  Placement = pos=(-560,-32.5,0) rot=(0,0,1;0rad)
FEATURE [App::Link] Stile_outer_right  label="Stile outer right001"
  LinkPlacement = pos=(560,-32.5,0) rot=(0,0,1;0rad)
  LinkedObject = -> Body002
  Placement = pos=(560,-32.5,0) rot=(0,0,1;0rad)
FEATURE [App::FeaturePython] Revolute  # Assembly joint (typed FeaturePython)
  Activated = true
  AngleMax = 0
  AngleMin = 0
  Detach1 = false
  Detach2 = false
  Distance = 0
  Distance2 = 0
  EnableAngleMax = false
  EnableAngleMin = false
  EnableLengthMax = false
  EnableLengthMin = false
  JointType = 1 (Revolute)
  LengthMax = 0
  LengthMin = 0
  Placement1 = pos=(-30,-17.5,920) rot=(0,0,1;0rad)
  Placement2 = pos=(-590,-50,920) rot=(0,0,1;0rad)
  Reference1 = -> Assembly [Stile_outer_left.Vertex5,Stile_outer_left.Vertex5]
  Reference2 = -> Assembly [Frame.Vertex14,Frame.Vertex14]
FEATURE [App::FeaturePython] Fixed  # Assembly joint (typed FeaturePython)
  Activated = true
  AngleMax = 0
  AngleMin = 0
  Detach1 = false
  Detach2 = false
  Distance = 0
  Distance2 = 0
  EnableAngleMax = false
  EnableAngleMin = false
  EnableLengthMax = false
  EnableLengthMin = false
  JointType = 0 (Fixed)
  LengthMax = 0
  LengthMin = 0
  Placement1 = pos=(30,-17.5,920) rot=(0,0,1;0rad)
  Placement2 = pos=(590,-50,920) rot=(0,0,1;0rad)
  Reference1 = -> Assembly [Stile_outer_right.Vertex5,Stile_outer_right.Vertex5]
  Reference2 = -> Assembly [Frame.Vertex13,Frame.Vertex13]
FEATURE [App::Link] Rail_top_left  label="Rail top left001"
  LinkPlacement = pos=(-300,-32.5,877.5) rot=(0,0,1;0rad)
  LinkedObject = -> Body009
  Placement = pos=(-300,-32.5,877.5) rot=(0,0,1;0rad)
FEATURE [App::Link] Rail_bottom_left  label="Rail bottom left001"
  LinkPlacement = pos=(-300,-32.5,-852.5) rot=(0,0,1;0rad)
  LinkedObject = -> Body010
  Placement = pos=(-300,-32.5,-852.5) rot=(0,0,1;0rad)
FEATURE [App::Link] Stile_inner_left  label="Stile inner left002"
  LinkPlacement = pos=(-30,-32.5,-9.095e-13) rot=(0,0,1;0rad)
  LinkedObject = -> Body003
  Placement = pos=(-30,-32.5,-9.095e-13) rot=(0,0,1;0rad)
FEATURE [App::Link] Muntin_bar  label="Muntin bar001"
  LinkPlacement = pos=(-290,-25,745) rot=(0,0,1;0rad)
  LinkedObject = -> Body
  Placement = pos=(-290,-25,745) rot=(0,0,1;0rad)
FEATURE [App::Link] Muntin_partitioned_left  label="Muntin partitioned left001"
  LinkPlacement = pos=(-300,-25,655) rot=(0,0,1;0rad)
  LinkedObject = -> Body006
  Placement = pos=(-300,-25,655) rot=(0,0,1;0rad)
FEATURE [App::Link] Muntin_single_left  label="Muntin single left001"
  LinkPlacement = pos=(-300,-25,175) rot=(0,0,1;0rad)
  LinkedObject = -> Body005
  Placement = pos=(-300,-25,175) rot=(0,0,1;0rad)
FEATURE [App::Link] Muntin_single_left001  label="Muntin single left002"
  LinkPlacement = pos=(-300,-25,-305) rot=(0,0,1;0rad)
  LinkedObject = -> Body005
  Placement = pos=(-300,-25,-305) rot=(0,0,1;0rad)
FEATURE [App::FeaturePython] Fixed001  # Assembly joint (typed FeaturePython)
  Activated = true
  AngleMax = 0
  AngleMin = 0
  Detach1 = false
  Detach2 = false
  Distance = 0
  Distance2 = 0
  EnableAngleMax = false
  EnableAngleMin = false
  EnableLengthMax = false
  EnableLengthMin = false
  JointType = 0 (Fixed)
  LengthMax = 0
  LengthMin = 0
  Placement1 = pos=(-225,0.5,42.5) rot=(0,0,1;0rad)
  Placement2 = pos=(35,0.5,920) rot=(0,0,1;0rad)
  Reference1 = -> Assembly [Rail_top_left.Vertex14,Rail_top_left.Vertex14]
  Reference2 = -> Assembly [Stile_outer_left.Vertex59,Stile_outer_left.Vertex59]
FEATURE [App::FeaturePython] Fixed002  # Assembly joint (typed FeaturePython)
  Activated = true
  AngleMax = 0
  AngleMin = 0
  Detach1 = false
  Detach2 = false
  Distance = 0
  Distance2 = 0
  EnableAngleMax = false
  EnableAngleMin = false
  EnableLengthMax = false
  EnableLengthMin = false
  JointType = 0 (Fixed)
  LengthMax = 0
  LengthMin = 0
  Placement1 = pos=(-35,-32.5,935) rot=(0,0,1;0rad)
  Placement2 = pos=(235,-32.5,57.5) rot=(0,0,1;0rad)
  Reference1 = -> Assembly [Stile_inner_left.Vertex6,Stile_inner_left.Vertex6]
  Reference2 = -> Assembly [Rail_top_left.Vertex34,Rail_top_left.Vertex34]
FEATURE [App::FeaturePython] Fixed003  # Assembly joint (typed FeaturePython)
  Activated = true
  AngleMax = 0
  AngleMin = 0
  Detach1 = false
  Detach2 = false
  Distance = 0
  Distance2 = 0
  EnableAngleMax = false
  EnableAngleMin = false
  EnableLengthMax = false
  EnableLengthMin = false
  JointType = 0 (Fixed)
  LengthMax = 0
  LengthMin = 0
  Placement1 = pos=(295,-14.5,82.5) rot=(0,0,1;0rad)
  Placement2 = pos=(25,-14.5,-770) rot=(0,0,1;0rad)
  Reference1 = -> Assembly [Rail_bottom_left.Vertex7,Rail_bottom_left.Vertex7]
  Reference2 = -> Assembly [Stile_inner_left.Vertex54,Stile_inner_left.Vertex54]
FEATURE [App::FeaturePython] Fixed004  # Assembly joint (typed FeaturePython)
  Activated = true
  AngleMax = 0
  AngleMin = 0
  Detach1 = false
  Detach2 = false
  Distance = 0
  Distance2 = 0
  EnableAngleMax = false
  EnableAngleMin = false
  EnableLengthMax = false
  EnableLengthMin = false
  JointType = 0 (Fixed)
  LengthMax = 0
  LengthMin = 0
  Placement1 = pos=(295,-17,15) rot=(0,0,1;0rad)
  Placement2 = pos=(25,-9.5,670) rot=(0,0,1;0rad)
  Reference1 = -> Assembly [Muntin_partitioned_left.Vertex23,Muntin_partitioned_left.Vertex23]
  Reference2 = -> Assembly [Stile_inner_left.Vertex84,Stile_inner_left.Vertex84]
FEATURE [App::FeaturePython] Fixed005  # Assembly joint (typed FeaturePython)
  Activated = true
  AngleMax = 0
  AngleMin = 0
  Detach1 = false
  Detach2 = false
  Distance = 0
  Distance2 = 0
  EnableAngleMax = false
  EnableAngleMin = false
  EnableLengthMax = false
  EnableLengthMin = false
  JointType = 0 (Fixed)
  LengthMax = 0
  LengthMin = 0
  Placement1 = pos=(15,-17,-75) rot=(0,0,1;0rad)
  Placement2 = pos=(25,-17,15) rot=(0,0,1;0rad)
  Reference1 = -> Assembly [Muntin_bar.Vertex14,Muntin_bar.Vertex14]
  Reference2 = -> Assembly [Muntin_partitioned_left.Vertex18,Muntin_partitioned_left.Vertex18]
FEATURE [App::FeaturePython] Fixed006  # Assembly joint (typed FeaturePython)
  Activated = true
  AngleMax = 0
  AngleMin = 0
  Detach1 = false
  Detach2 = false
  Distance = 0
  Distance2 = 0
  EnableAngleMax = false
  EnableAngleMin = false
  EnableLengthMax = false
  EnableLengthMin = false
  JointType = 0 (Fixed)
  LengthMax = 0
  LengthMin = 0
  Placement1 = pos=(295,-17,15) rot=(0,0,1;0rad)
  Placement2 = pos=(25,-9.5,190) rot=(0,0,1;0rad)
  Reference1 = -> Assembly [Muntin_single_left.Vertex19,Muntin_single_left.Vertex19]
  Reference2 = -> Assembly [Stile_inner_left.Vertex74,Stile_inner_left.Vertex74]
FEATURE [App::FeaturePython] Fixed007  # Assembly joint (typed FeaturePython)
  Activated = true
  AngleMax = 0
  AngleMin = 0
  Detach1 = false
  Detach2 = false
  Distance = 0
  Distance2 = 0
  EnableAngleMax = false
  EnableAngleMin = false
  EnableLengthMax = false
  EnableLengthMin = false
  JointType = 0 (Fixed)
  LengthMax = 0
  LengthMin = 0
  Placement1 = pos=(295,-17,15) rot=(0,0,1;0rad)
  Placement2 = pos=(25,-9.5,-290) rot=(0,0,1;0rad)
  Reference1 = -> Assembly [Muntin_single_left001.Vertex19,Muntin_single_left001.Vertex19]
  Reference2 = -> Assembly [Stile_inner_left.Vertex64,Stile_inner_left.Vertex64]
FEATURE [App::DocumentObjectGroup] Group003  label="Left"
  Group = -> [Body001,Body003,Body005,Body006,Body009,Body010]
FEATURE [App::DocumentObjectGroup] Group004  label="Right"
  Group = -> [Body002,Body004,Body007,Body008,Body011,Body012]
FEATURE [App::DocumentObjectGroup] Group  label="Components"
  Group = -> [Body013,Body,Group003,Group004]
FEATURE [App::Link] Stile_inner_right  label="Stile inner right001"
  LinkPlacement = pos=(30,-32.5,0) rot=(0,0,1;0rad)
  LinkedObject = -> Body004
  Placement = pos=(30,-32.5,0) rot=(0,0,1;0rad)
FEATURE [App::Link] Rail_top_right  label="Rail top right001"
  LinkPlacement = pos=(300,-32.5,877.5) rot=(0,0,1;0rad)
  LinkedObject = -> Body011
  Placement = pos=(300,-32.5,877.5) rot=(0,0,1;0rad)
FEATURE [App::Link] Rail_bottom_right  label="Rail bottom right001"
  LinkPlacement = pos=(300,-32.5,-852.5) rot=(0,0,1;0rad)
  LinkedObject = -> Body012
  Placement = pos=(300,-32.5,-852.5) rot=(0,0,1;0rad)
FEATURE [App::Link] Muntin_bar001  label="Muntin bar002"
  LinkPlacement = pos=(290,-25,745) rot=(0,0,1;0rad)
  LinkedObject = -> Body
  Placement = pos=(290,-25,745) rot=(0,0,1;0rad)
FEATURE [App::Link] Muntin_partitioned_right  label="Muntin partitioned right001"
  LinkPlacement = pos=(300,-25,655) rot=(0,0,1;0rad)
  LinkedObject = -> Body008
  Placement = pos=(300,-25,655) rot=(0,0,1;0rad)
FEATURE [App::Link] Muntin_single_right  label="Muntin single right001"
  LinkPlacement = pos=(300,-25,175) rot=(0,0,1;0rad)
  LinkedObject = -> Body007
  Placement = pos=(300,-25,175) rot=(0,0,1;0rad)
FEATURE [App::Link] Muntin_single_right001  label="Muntin single right002"
  LinkPlacement = pos=(300,-25,-305) rot=(0,0,1;0rad)
  LinkedObject = -> Body007
  Placement = pos=(300,-25,-305) rot=(0,0,1;0rad)
FEATURE [App::FeaturePython] Fixed008  # Assembly joint (typed FeaturePython)
  Activated = true
  AngleMax = 0
  AngleMin = 0
  Detach1 = false
  Detach2 = false
  Distance = 0
  Distance2 = 0
  EnableAngleMax = false
  EnableAngleMin = false
  EnableLengthMax = false
  EnableLengthMin = false
  JointType = 0 (Fixed)
  LengthMax = 0
  LengthMin = 0
  Placement1 = pos=(215,-32.5,57.5) rot=(0,0,1;0rad)
  Placement2 = pos=(-45,-32.5,935) rot=(0,0,1;0rad)
  Reference1 = -> Assembly [Rail_top_right.Vertex29,Rail_top_right.Vertex29]
  Reference2 = -> Assembly [Stile_outer_right.Vertex11,Stile_outer_right.Vertex11]
FEATURE [App::FeaturePython] Fixed009  # Assembly joint (typed FeaturePython)
  Activated = true
  AngleMax = 0
  AngleMin = 0
  Detach1 = false
  Detach2 = false
  Distance = 0
  Distance2 = 0
  EnableAngleMax = false
  EnableAngleMin = false
  EnableLengthMax = false
  EnableLengthMin = false
  JointType = 0 (Fixed)
  LengthMax = 0
  LengthMin = 0
  Placement1 = pos=(35,-32.5,935) rot=(0,0,1;0rad)
  Placement2 = pos=(-235,-32.5,57.5) rot=(0,0,1;0rad)
  Reference1 = -> Assembly [Stile_inner_right.Vertex6,Stile_inner_right.Vertex6]
  Reference2 = -> Assembly [Rail_top_right.Vertex32,Rail_top_right.Vertex32]
FEATURE [App::FeaturePython] Fixed010  # Assembly joint (typed FeaturePython)
  Activated = true
  AngleMax = 0
  AngleMin = 0
  Detach1 = false
  Detach2 = false
  Distance = 0
  Distance2 = 0
  EnableAngleMax = false
  EnableAngleMin = false
  EnableLengthMax = false
  EnableLengthMin = false
  JointType = 0 (Fixed)
  LengthMax = 0
  LengthMin = 0
  Placement1 = pos=(290,-7,15) rot=(0,0,1;0rad)
  Placement2 = pos=(30,0.5,670) rot=(0,0,1;0rad)
  Reference1 = -> Assembly [Muntin_partitioned_right.Vertex13,Muntin_partitioned_right.Vertex13]
  Reference2 = -> Assembly [Stile_outer_right.Vertex27,Stile_outer_right.Vertex27]
FEATURE [App::FeaturePython] Fixed011  # Assembly joint (typed FeaturePython)
  Activated = true
  AngleMax = 0
  AngleMin = 0
  Detach1 = false
  Detach2 = false
  Distance = 0
  Distance2 = 0
  EnableAngleMax = false
  EnableAngleMin = false
  EnableLengthMax = false
  EnableLengthMin = false
  JointType = 0 (Fixed)
  LengthMax = 0
  LengthMin = 0
  Placement1 = pos=(15,-17,-75) rot=(0,0,1;0rad)
  Placement2 = pos=(5,-17,15) rot=(0,0,1;0rad)
  Reference1 = -> Assembly [Muntin_bar001.Vertex14,Muntin_bar001.Vertex14]
  Reference2 = -> Assembly [Muntin_partitioned_right.Vertex15,Muntin_partitioned_right.Vertex15]
FEATURE [App::FeaturePython] Fixed012  # Assembly joint (typed FeaturePython)
  Activated = true
  AngleMax = 0
  AngleMin = 0
  Detach1 = false
  Detach2 = false
  Distance = 0
  Distance2 = 0
  EnableAngleMax = false
  EnableAngleMin = false
  EnableLengthMax = false
  EnableLengthMin = false
  JointType = 0 (Fixed)
  LengthMax = 0
  LengthMin = 0
  Placement1 = pos=(290,-7,15) rot=(0,0,1;0rad)
  Placement2 = pos=(30,0.5,190) rot=(0,0,1;0rad)
  Reference1 = -> Assembly [Muntin_single_right.Vertex13,Muntin_single_right.Vertex13]
  Reference2 = -> Assembly [Stile_outer_right.Vertex23,Stile_outer_right.Vertex23]
FEATURE [App::FeaturePython] Fixed013  # Assembly joint (typed FeaturePython)
  Activated = true
  AngleMax = 0
  AngleMin = 0
  Detach1 = false
  Detach2 = false
  Distance = 0
  Distance2 = 0
  EnableAngleMax = false
  EnableAngleMin = false
  EnableLengthMax = false
  EnableLengthMin = false
  JointType = 0 (Fixed)
  LengthMax = 0
  LengthMin = 0
  Placement1 = pos=(290,-7,15) rot=(0,0,1;0rad)
  Placement2 = pos=(30,0.5,-290) rot=(0,0,1;0rad)
  Reference1 = -> Assembly [Muntin_single_right001.Vertex13,Muntin_single_right001.Vertex13]
  Reference2 = -> Assembly [Stile_outer_right.Vertex21,Stile_outer_right.Vertex21]
FEATURE [App::FeaturePython] Fixed014  # Assembly joint (typed FeaturePython)
  Activated = true
  AngleMax = 0
  AngleMin = 0
  Detach1 = false
  Detach2 = false
  Distance = 0
  Distance2 = 0
  EnableAngleMax = false
  EnableAngleMin = false
  EnableLengthMax = false
  EnableLengthMin = false
  JointType = 0 (Fixed)
  LengthMax = 0
  LengthMin = 0
  Placement1 = pos=(290,0.5,82.5) rot=(0,0,1;0rad)
  Placement2 = pos=(30,0.5,-770) rot=(0,0,1;0rad)
  Reference1 = -> Assembly [Rail_bottom_right.Vertex11,Rail_bottom_right.Vertex11]
  Reference2 = -> Assembly [Stile_outer_right.Vertex16,Stile_outer_right.Vertex16]
FEATURE [App::Link] Glass_full_assembly  label="Glass full assembly"
  LinkPlacement = pos=(-254.096,34.1996,-592.634) rot=(0,0,1;0rad)
  LinkedObject = -> <external F4.2.FCStd>#Assembly
  Placement = pos=(-254.096,34.1996,-592.634) rot=(0,0,1;0rad)
FEATURE [App::Link] Glass_full_assembly001  label="Glass full assembly001"
  LinkPlacement = pos=(-254.096,34.1996,-112.634) rot=(0,0,1;0rad)
  LinkedObject = -> <external F4.2.FCStd>#Assembly
  Placement = pos=(-254.096,34.1996,-112.634) rot=(0,0,1;0rad)
FEATURE [App::Link] Glass_full_assembly002  label="Glass full assembly002"
  LinkPlacement = pos=(-254.096,34.1996,367.366) rot=(0,0,1;0rad)
  LinkedObject = -> <external F4.2.FCStd>#Assembly
  Placement = pos=(-254.096,34.1996,367.366) rot=(0,0,1;0rad)
FEATURE [App::Link] Glass_full_assembly003  label="Glass full assembly003"
  LinkPlacement = pos=(325.904,34.1996,367.366) rot=(0,0,1;0rad)
  LinkedObject = -> <external F4.2.FCStd>#Assembly
  Placement = pos=(325.904,34.1996,367.366) rot=(0,0,1;0rad)
FEATURE [App::Link] Glass_full_assembly004  label="Glass full assembly004"
  LinkPlacement = pos=(325.904,34.1996,-112.634) rot=(0,0,1;0rad)
  LinkedObject = -> <external F4.2.FCStd>#Assembly
  Placement = pos=(325.904,34.1996,-112.634) rot=(0,0,1;0rad)
FEATURE [App::Link] Glass_full_assembly005  label="Glass full assembly005"
  LinkPlacement = pos=(325.904,34.1996,-592.634) rot=(0,0,1;0rad)
  LinkedObject = -> <external F4.2.FCStd>#Assembly
  Placement = pos=(325.904,34.1996,-592.634) rot=(0,0,1;0rad)
FEATURE [App::FeaturePython] Fixed015  # Assembly joint (typed FeaturePython)
  Activated = true
  AngleMax = 0
  AngleMin = 0
  Detach1 = false
  Detach2 = false
  Distance = 0
  Distance2 = 0
  EnableAngleMax = false
  EnableAngleMin = false
  EnableLengthMax = false
  EnableLengthMin = false
  JointType = 0 (Fixed)
  LengthMax = 0
  LengthMin = 0
  Placement1 = pos=(235,-12,235) rot=(0,0,1;0rad)
  Placement2 = pos=(245,-7,-5) rot=(0,0,1;0rad)
  Reference1 = -> Assembly [Glass_full_assembly.Glass_third.Vertex8,Glass_full_assembly.Glass_third.Vertex8]
  Reference2 = -> Assembly [Muntin_single_left001.Vertex24,Muntin_single_left001.Vertex24]
FEATURE [App::FeaturePython] Fixed016  # Assembly joint (typed FeaturePython)
  Activated = true
  AngleMax = 0
  AngleMin = 0
  Detach1 = false
  Detach2 = false
  Distance = 0
  Distance2 = 0
  EnableAngleMax = false
  EnableAngleMin = false
  EnableLengthMax = false
  EnableLengthMin = false
  JointType = 0 (Fixed)
  LengthMax = 0
  LengthMin = 0
  Placement1 = pos=(235,-12,235) rot=(0,0,1;0rad)
  Placement2 = pos=(245,-7,-5) rot=(0,0,1;0rad)
  Reference1 = -> Assembly [Glass_full_assembly001.Glass_third.Vertex8,Glass_full_assembly001.Glass_third.Vertex8]
  Reference2 = -> Assembly [Muntin_single_left.Vertex24,Muntin_single_left.Vertex24]
FEATURE [App::FeaturePython] Fixed017  # Assembly joint (typed FeaturePython)
  Activated = true
  AngleMax = 0
  AngleMin = 0
  Detach1 = false
  Detach2 = false
  Distance = 0
  Distance2 = 0
  EnableAngleMax = false
  EnableAngleMin = false
  EnableLengthMax = false
  EnableLengthMin = false
  JointType = 0 (Fixed)
  LengthMax = 0
  LengthMin = 0
  Placement1 = pos=(245,-7,-5) rot=(0,0,1;0rad)
  Placement2 = pos=(235,-12,235) rot=(0,0,1;0rad)
  Reference1 = -> Assembly [Muntin_partitioned_left.Vertex27,Muntin_partitioned_left.Vertex27]
  Reference2 = -> Assembly [Glass_full_assembly002.Glass_third.Vertex8,Glass_full_assembly002.Glass_third.Vertex8]
FEATURE [App::FeaturePython] Fixed018  # Assembly joint (typed FeaturePython)
  Activated = true
  AngleMax = 0
  AngleMin = 0
  Detach1 = false
  Detach2 = false
  Distance = 0
  Distance2 = 0
  EnableAngleMax = false
  EnableAngleMin = false
  EnableLengthMax = false
  EnableLengthMin = false
  JointType = 0 (Fixed)
  LengthMax = 0
  LengthMin = 0
  Placement1 = pos=(235,-12,235) rot=(0,0,1;0rad)
  Placement2 = pos=(225,-7,-5) rot=(0,0,1;0rad)
  Reference1 = -> Assembly [Glass_full_assembly003.Glass_third.Vertex8,Glass_full_assembly003.Glass_third.Vertex8]
  Reference2 = -> Assembly [Muntin_partitioned_right.Vertex24,Muntin_partitioned_right.Vertex24]
FEATURE [App::FeaturePython] Fixed019  # Assembly joint (typed FeaturePython)
  Activated = true
  AngleMax = 0
  AngleMin = 0
  Detach1 = false
  Detach2 = false
  Distance = 0
  Distance2 = 0
  EnableAngleMax = false
  EnableAngleMin = false
  EnableLengthMax = false
  EnableLengthMin = false
  JointType = 0 (Fixed)
  LengthMax = 0
  LengthMin = 0
  Placement1 = pos=(235,-12,235) rot=(0,0,1;0rad)
  Placement2 = pos=(225,-7,-5) rot=(0,0,1;0rad)
  Reference1 = -> Assembly [Glass_full_assembly004.Glass_third.Vertex8,Glass_full_assembly004.Glass_third.Vertex8]
  Reference2 = -> Assembly [Muntin_single_right.Vertex18,Muntin_single_right.Vertex18]
FEATURE [App::FeaturePython] Fixed020  # Assembly joint (typed FeaturePython)
  Activated = true
  AngleMax = 0
  AngleMin = 0
  Detach1 = false
  Detach2 = false
  Distance = 0
  Distance2 = 0
  EnableAngleMax = false
  EnableAngleMin = false
  EnableLengthMax = false
  EnableLengthMin = false
  JointType = 0 (Fixed)
  LengthMax = 0
  LengthMin = 0
  Placement1 = pos=(235,-12,235) rot=(0,0,1;0rad)
  Placement2 = pos=(225,-7,-5) rot=(0,0,1;0rad)
  Reference1 = -> Assembly [Glass_full_assembly005.Glass_third.Vertex8,Glass_full_assembly005.Glass_third.Vertex8]
  Reference2 = -> Assembly [Muntin_single_right001.Vertex18,Muntin_single_right001.Vertex18]
FEATURE [App::Link] Glass_third_assembly  label="Glass third assembly"
  LinkPlacement = pos=(-134.096,34.1996,697.366) rot=(0,0,1;0rad)
  LinkedObject = -> <external F4.1.FCStd>#Assembly
  Placement = pos=(-134.096,34.1996,697.366) rot=(0,0,1;0rad)
FEATURE [App::Link] Glass_third_assembly001  label="Glass third assembly001"
  LinkPlacement = pos=(-374.096,34.1996,697.366) rot=(0,0,1;0rad)
  LinkedObject = -> <external F4.1.FCStd>#Assembly
  Placement = pos=(-374.096,34.1996,697.366) rot=(0,0,1;0rad)
FEATURE [App::DocumentObjectGroup] Group002  label="Left sash"
  Group = -> [Stile_outer_left,Rail_top_left,Rail_bottom_left,Stile_inner_left,Muntin_bar,Muntin_partitioned_left,Muntin_single_left,Muntin_single_left001,Glass_full_assembly,Glass_full_assembly001,Glass_full_assembly002,Glass_third_assembly,Glass_third_assembly001]
FEATURE [App::Link] Glass_third_assembly002  label="Glass third assembly002"
  LinkPlacement = pos=(445.904,34.1996,697.366) rot=(0,0,1;0rad)
  LinkedObject = -> <external F4.1.FCStd>#Assembly
  Placement = pos=(445.904,34.1996,697.366) rot=(0,0,1;0rad)
FEATURE [App::Link] Glass_third_assembly003  label="Glass third assembly003"
  LinkPlacement = pos=(205.904,34.1996,697.366) rot=(0,0,1;0rad)
  LinkedObject = -> <external F4.1.FCStd>#Assembly
  Placement = pos=(205.904,34.1996,697.366) rot=(0,0,1;0rad)
FEATURE [App::DocumentObjectGroup] Group005  label="Right sash"
  Group = -> [Stile_outer_right,Stile_inner_right,Rail_top_right,Rail_bottom_right,Muntin_bar001,Muntin_partitioned_right,Muntin_single_right,Muntin_single_right001,Glass_full_assembly003,Glass_full_assembly004,Glass_full_assembly005,Glass_third_assembly002,Glass_third_assembly003]
FEATURE [App::FeaturePython] Fixed021  # Assembly joint (typed FeaturePython)
  Activated = true
  AngleMax = 0
  AngleMin = 0
  Detach1 = false
  Detach2 = false
  Distance = 0
  Distance2 = 0
  EnableAngleMax = false
  EnableAngleMin = false
  EnableLengthMax = false
  EnableLengthMin = false
  JointType = 0 (Fixed)
  LengthMax = 0
  LengthMin = 0
  Placement1 = pos=(115,-12,85) rot=(0,0,1;0rad)
  Placement2 = pos=(245,0.5,-47.5) rot=(0,0,1;0rad)
  Reference1 = -> Assembly [Glass_third_assembly.Glass_third.Vertex8,Glass_third_assembly.Glass_third.Vertex8]
  Reference2 = -> Assembly [Rail_top_left.Face26,Rail_top_left.Vertex39]
FEATURE [App::FeaturePython] Fixed022  # Assembly joint (typed FeaturePython)
  Activated = true
  AngleMax = 0
  AngleMin = 0
  Detach1 = false
  Detach2 = false
  Distance = 0
  Distance2 = 0
  EnableAngleMax = false
  EnableAngleMin = false
  EnableLengthMax = false
  EnableLengthMin = false
  JointType = 0 (Fixed)
  LengthMax = 0
  LengthMin = 0
  Placement1 = pos=(115,-12,85) rot=(0,0,1;0rad)
  Placement2 = pos=(-5,-7,85) rot=(0,0,1;0rad)
  Reference1 = -> Assembly [Glass_third_assembly001.Glass_third.Vertex8,Glass_third_assembly001.Glass_third.Vertex8]
  Reference2 = -> Assembly [Muntin_bar.Vertex19,Muntin_bar.Vertex19]
FEATURE [App::FeaturePython] Fixed023  # Assembly joint (typed FeaturePython)
  Activated = true
  AngleMax = 0
  AngleMin = 0
  Detach1 = false
  Detach2 = false
  Distance = 0
  Distance2 = 0
  EnableAngleMax = false
  EnableAngleMin = false
  EnableLengthMax = false
  EnableLengthMin = false
  JointType = 0 (Fixed)
  LengthMax = 0
  LengthMin = 0
  Placement1 = pos=(115,-12,85) rot=(0,0,1;0rad)
  Placement2 = pos=(225,0.5,-47.5) rot=(0,0,1;0rad)
  Reference1 = -> Assembly [Glass_third_assembly002.Glass_third.Vertex8,Glass_third_assembly002.Glass_third.Vertex8]
  Reference2 = -> Assembly [Rail_top_right.Vertex45,Rail_top_right.Vertex45]
FEATURE [App::FeaturePython] Fixed024  # Assembly joint (typed FeaturePython)
  Activated = true
  AngleMax = 0
  AngleMin = 0
  Detach1 = false
  Detach2 = false
  Distance = 0
  Distance2 = 0
  EnableAngleMax = false
  EnableAngleMin = false
  EnableLengthMax = false
  EnableLengthMin = false
  JointType = 0 (Fixed)
  LengthMax = 0
  LengthMin = 0
  Placement1 = pos=(115,-12,85) rot=(0,0,1;0rad)
  Placement2 = pos=(-5,-7,85) rot=(0,0,1;0rad)
  Reference1 = -> Assembly [Glass_third_assembly003.Glass_third.Vertex8,Glass_third_assembly003.Glass_third.Vertex8]
  Reference2 = -> Assembly [Muntin_bar001.Vertex19,Muntin_bar001.Vertex19]
FEATURE [Assembly::JointGroup] Joints
  Group = -> [GroundedJoint,Revolute,Fixed,Fixed001,Fixed002,Fixed003,Fixed004,Fixed005,Fixed006,Fixed007,Fixed008,Fixed009,Fixed010,Fixed011,Fixed012,Fixed013,Fixed014,Fixed015,Fixed016,Fixed017,Fixed018,Fixed019,Fixed020,Fixed021,Fixed022,Fixed023,Fixed024]
FEATURE [Assembly::AssemblyObject] Assembly
  Group = -> [Joints,Frame,GroundedJoint,Revolute,Fixed,Fixed001,Fixed002,Fixed003,Fixed004,Fixed005,Fixed006,Fixed007,Group002,Stile_outer_left,Stile_outer_right,Rail_top_left,Rail_bottom_left,Stile_inner_left,Muntin_bar,Muntin_partitioned_left,Muntin_single_left,Muntin_single_left001,Group005,Fixed008,Fixed009,Fixed010,Fixed011,Fixed012,Fixed013,Fixed014,Stile_inner_right,Rail_top_right,Rail_bottom_right,+24 more]
  Origin = -> Origin014
  Type = Assembly

RESOLVED EXTERNAL PARTS (link-assembly join: the EXTERNAL_REF files above that resolve inside this repo's crawl, each included once):
---- part F4.1.FCStd = doc fcstd_89af0879d9a1 ----
FCSTD DOCUMENT  (FreeCAD 1.1R38894 (Git))
Label: F4.1
License: All rights reserved
LicenseURL: https://en.wikipedia.org/wiki/All_rights_reserved
objects: App::Link×5, App::FeaturePython×5, Sketcher::SketchObject×3, PartDesign::Pad×3, PartDesign::Body×3, PartDesign::Chamfer×2, PartDesign::Fillet×2, App::VarSet×1, App::DocumentObjectGroup×1, Assembly::JointGroup×1, Assembly::AssemblyObject×1
note: 30 computed .brp shape members not serialized (recipe doc carries the construction recipe); baked Part::Feature solids carry a one-line shape summary decoded from their .brp

FEATURE [Sketcher::SketchObject] Sketch
  ArcFitTolerance = 0
  AttachmentSupport = -> [XZ_Plane]
  FullyConstrained = true
  MakeInternals = false
  MapMode = 5
  Placement = pos=(0,0,0) rot=(1,0,0;1.5708rad)
  expr: Constraints[10] = <<Parameters>>.GlassLength
  expr: Constraints[11] = <<Parameters>>.GlassWidth
  sketch-geometry (5):
    g0: LineSegment StartX=-115 StartY=85 StartZ=0 EndX=-115 EndY=-85 EndZ=0
    g1: LineSegment StartX=-115 StartY=-85 StartZ=0 EndX=115 EndY=-85 EndZ=0
    g2: LineSegment StartX=115 StartY=-85 StartZ=0 EndX=115 EndY=85 EndZ=0
    g3: LineSegment StartX=115 StartY=85 StartZ=0 EndX=-115 EndY=85 EndZ=0
    g4: GeomPoint [constr] X=0 Y=0 Z=0
  constraints (12):
    c: Coincident(g0,g1)
    c: Coincident(g1,g2)
    c: Coincident(g2,g3)
    c: Coincident(g3,g0)
    c: Vertical(g0)
    c: Vertical(g2)
    c: Horizontal(g1)
    c: Horizontal(g3)
    c: Symmetric(g2,g0,g4)
    c: Coincident(g4,g-1)
    c: DistanceX(g3,g3) = 230
    c: DistanceY(g2,g2) = 170
FEATURE [Sketcher::SketchObject] Sketch001
  ArcFitTolerance = 0
  AttachmentSupport = -> [XZ_Plane001]
  FullyConstrained = true
  MakeInternals = false
  MapMode = 5
  Placement = pos=(0,0,0) rot=(1,0,0;1.5708rad)
  expr: Constraints[10] = <<Parameters>>.GlazingBeadHalfLength
  expr: Constraints[11] = <<Parameters>>.GlazingBeadHalfWidth
  sketch-geometry (5):
    g0: LineSegment StartX=-115 StartY=-4 StartZ=0 EndX=115 EndY=-4 EndZ=0
    g1: LineSegment StartX=115 StartY=-4 StartZ=0 EndX=115 EndY=4 EndZ=0
    g2: LineSegment StartX=115 StartY=4 StartZ=0 EndX=-115 EndY=4 EndZ=0
    g3: LineSegment StartX=-115 StartY=4 StartZ=0 EndX=-115 EndY=-4 EndZ=0
    g4: GeomPoint [constr] X=0 Y=0 Z=0
  constraints (12):
    c: Coincident(g0,g1)
    c: Coincident(g1,g2)
    c: Coincident(g2,g3)
    c: Coincident(g3,g0)
    c: Horizontal(g0)
    c: Horizontal(g2)
    c: Vertical(g1)
    c: Vertical(g3)
    c: Symmetric(g2,g0,g4)
    c: Coincident(g4,g-1)
    c: DistanceX(g2,g2) = 230
    c: DistanceY(g3,g3) = 8
FEATURE [App::VarSet] VarSet  label="Parameters"
  GlassLength = 230
  GlassThickness = 24
  GlassWidth = 170
  GlazingBeadHalfLength = 230
  GlazingBeadHalfWidth = 8
  GlazingBeadThickness = 8
  GlazingBeadThirdLength = 170
  GlazingBeadThirdWidth = 8
  GlazingBeadWidth = 8
  expr: GlazingBeadHalfLength = GlassLength
  expr: GlazingBeadThirdLength = GlassWidth
FEATURE [PartDesign::Pad] Pad
  Direction = (0,-1,2e-16)
  Length = 24
  Length2 = 10
  Midplane = true
  Placement = pos=(0,0,0) rot=(1,0,0;1.5708rad)
  Profile = -> Sketch
  ReferenceAxis = -> Sketch [N_Axis]
  Refine = true
  Suppressed = false
  Type = 0
  expr: Length = <<Parameters>>.GlassThickness
FEATURE [PartDesign::Body] Body  label="Glass third"
  AllowCompound = false
  Group = -> [Sketch,Pad]
  Length = 230
  Origin = -> Origin
  Thickness = 24
  Tip = -> Pad
  Width = 170
FEATURE [PartDesign::Pad] Pad001  label="Stock"
  Direction = (0,-1,2e-16)
  Length = 8
  Length2 = 10
  Midplane = true
  Placement = pos=(0,0,0) rot=(1,0,0;1.5708rad)
  Profile = -> Sketch001
  ReferenceAxis = -> Sketch001 [N_Axis]
  Refine = true
  Suppressed = false
  Type = 0
  expr: Length = <<Parameters>>.GlazingBeadThickness
FEATURE [PartDesign::Chamfer] Chamfer
  Angle = 45
  Base = -> Pad001 [Edge5,Edge8]
  BaseFeature = -> Pad001
  ChamferType = 0
  FlipDirection = false
  Placement = pos=(0,0,0) rot=(1,0,0;1.5708rad)
  Refine = true
  Size = 7.99
  Size2 = 1
  SupportTransform = false
  Suppressed = false
  UseAllEdges = false
  expr: Size = <<Parameters>>.GlazingBeadWidth - 0.01 mm
FEATURE [PartDesign::Fillet] Fillet
  Base = -> Chamfer [Edge7]
  BaseFeature = -> Chamfer
  Placement = pos=(0,0,0) rot=(1,0,0;1.5708rad)
  Radius = 7.99
  Refine = true
  SupportTransform = false
  Suppressed = false
  UseAllEdges = false
  expr: Radius = <<Parameters>>.GlazingBeadThickness - 0.01 mm
FEATURE [PartDesign::Body] Body001  label="Glazing bead half"
  AllowCompound = false
  Group = -> [Sketch001,Pad001,Chamfer,Fillet]
  Length = 230
  Origin = -> Origin001
  Thickness = 8
  Tip = -> Fillet
  Width = 8
FEATURE [Sketcher::SketchObject] Sketch002
  ArcFitTolerance = 0
  AttachmentSupport = -> [XZ_Plane002]
  FullyConstrained = true
  MakeInternals = false
  MapMode = 5
  Placement = pos=(0,0,0) rot=(1,0,0;1.5708rad)
  expr: Constraints[10] = <<Parameters>>.GlazingBeadThirdLength
  expr: Constraints[11] = <<Parameters>>.GlazingBeadThirdWidth
  sketch-geometry (5):
    g0: LineSegment StartX=-85 StartY=-4 StartZ=0 EndX=85 EndY=-4 EndZ=0
    g1: LineSegment StartX=85 StartY=-4 StartZ=0 EndX=85 EndY=4 EndZ=0
    g2: LineSegment StartX=85 StartY=4 StartZ=0 EndX=-85 EndY=4 EndZ=0
    g3: LineSegment StartX=-85 StartY=4 StartZ=0 EndX=-85 EndY=-4 EndZ=0
    g4: GeomPoint [constr] X=0 Y=0 Z=0
  constraints (12):
    c: Coincident(g0,g1)
    c: Coincident(g1,g2)
    c: Coincident(g2,g3)
    c: Coincident(g3,g0)
    c: Horizontal(g0)
    c: Horizontal(g2)
    c: Vertical(g1)
    c: Vertical(g3)
    c: Symmetric(g2,g0,g4)
    c: Coincident(g4,g-1)
    c: DistanceX(g2,g2) = 170
    c: DistanceY(g3,g3) = 8
FEATURE [PartDesign::Pad] Pad002  label="Stock001"
  Direction = (0,-1,2e-16)
  Length = 8
  Length2 = 10
  Midplane = true
  Placement = pos=(0,0,0) rot=(1,0,0;1.5708rad)
  Profile = -> Sketch002
  ReferenceAxis = -> Sketch002 [N_Axis]
  Refine = true
  Suppressed = false
  Type = 0
  expr: Length = <<Parameters>>.GlazingBeadThickness
FEATURE [PartDesign::Chamfer] Chamfer001
  Angle = 45
  Base = -> Pad002 [Edge5,Edge8]
  BaseFeature = -> Pad002
  ChamferType = 0
  FlipDirection = false
  Placement = pos=(0,0,0) rot=(1,0,0;1.5708rad)
  Refine = true
  Size = 7.99
  Size2 = 1
  SupportTransform = false
  Suppressed = false
  UseAllEdges = false
  expr: Size = <<Parameters>>.GlazingBeadWidth - 0.01 mm
FEATURE [PartDesign::Fillet] Fillet001
  Base = -> Chamfer001 [Edge7]
  BaseFeature = -> Chamfer001
  Placement = pos=(0,0,0) rot=(1,0,0;1.5708rad)
  Radius = 7.99
  Refine = true
  SupportTransform = false
  Suppressed = false
  UseAllEdges = false
  expr: Radius = <<Parameters>>.GlazingBeadThickness - 0.01 mm
FEATURE [PartDesign::Body] Body002  label="Glazing bead third"
  AllowCompound = false
  Group = -> [Sketch002,Pad002,Chamfer001,Fillet001]
  Length = 170
  Origin = -> Origin002
  Thickness = 8
  Tip = -> Fillet001
  Width = 8
FEATURE [App::DocumentObjectGroup] Group  label="Components"
  Group = -> [Body,Body001,Body002]
FEATURE [App::Link] Glass_third  label="Glass third001"
  LinkPlacement = pos=(-35.9039,-54.1996,47.6343) rot=(0,0,1;0rad)
  LinkedObject = -> Body
  Placement = pos=(-35.9039,-54.1996,47.6343) rot=(0,0,1;0rad)
FEATURE [App::FeaturePython] GroundedJoint  # Assembly grounded joint (typed FeaturePython)
  ObjectToGround = -> Glass_third
  Placement = pos=(-35.9039,-54.1996,47.6343) rot=(0,0,1;0rad)
FEATURE [App::Link] Glazing_bead_half  label="Glazing bead half001"
  LinkPlacement = pos=(-35.9039,-38.1996,-33.3757) rot=(0,0,1;0rad)
  LinkedObject = -> Body001
  Placement = pos=(-35.9039,-38.1996,-33.3757) rot=(0,0,1;0rad)
FEATURE [App::Link] Glazing_bead_half001  label="Glazing bead half002"
  LinkPlacement = pos=(-35.9039,-38.1996,128.644) rot=(0,1,0;3.14159rad)
  LinkedObject = -> Body001
  Placement = pos=(-35.9039,-38.1996,128.644) rot=(0,1,0;3.14159rad)
FEATURE [App::Link] Glazing_bead_third  label="Glazing bead third001"
  LinkPlacement = pos=(75.1061,-38.1996,47.6343) rot=(0,1,0;4.71239rad)
  LinkedObject = -> Body002
  Placement = pos=(75.1061,-38.1996,47.6343) rot=(0,1,0;4.71239rad)
FEATURE [App::Link] Glazing_bead_third001  label="Glazing bead third002"
  LinkPlacement = pos=(-146.914,-38.1996,47.6343) rot=(0,1,0;1.5708rad)
  LinkedObject = -> Body002
  Placement = pos=(-146.914,-38.1996,47.6343) rot=(0,1,0;1.5708rad)
FEATURE [App::FeaturePython] Fixed  # Assembly joint (typed FeaturePython)
  Activated = true
  AngleMax = 0
  AngleMin = 0
  Detach1 = false
  Detach2 = false
  Distance = 0
  Distance2 = 0
  EnableAngleMax = false
  EnableAngleMin = false
  EnableLengthMax = false
  EnableLengthMin = false
  JointType = 0 (Fixed)
  LengthMax = 0
  LengthMin = 0
  Placement1 = pos=(115,12,-85) rot=(0,0,1;0rad)
  Placement2 = pos=(115,-4,-3.99) rot=(0,0,1;0rad)
  Reference1 = -> Assembly [Glass_third.Edge9,Glass_third.Vertex5]
  Reference2 = -> Assembly [Glazing_bead_half.Vertex7,Glazing_bead_half.Vertex7]
FEATURE [App::FeaturePython] Fixed001  # Assembly joint (typed FeaturePython)
  Activated = true
  AngleMax = 0
  AngleMin = 0
  Detach1 = false
  Detach2 = false
  Distance = 0
  Distance2 = 0
  EnableAngleMax = false
  EnableAngleMin = false
  EnableLengthMax = false
  EnableLengthMin = false
  JointType = 0 (Fixed)
  LengthMax = 0
  LengthMin = 0
  Offset2 = pos=(0,0,0) rot=(0,0,1;3.14159rad)
  Placement1 = pos=(-115,12,85) rot=(0,0,1;0rad)
  Placement2 = pos=(115,-4,-3.99) rot=(0,0,1;3.14159rad)
  Reference1 = -> Assembly [Glass_third.Vertex1,Glass_third.Vertex1]
  Reference2 = -> Assembly [Glazing_bead_half001.Vertex7,Glazing_bead_half001.Vertex7]
FEATURE [App::FeaturePython] Fixed002  # Assembly joint (typed FeaturePython)
  Activated = true
  AngleMax = 0
  AngleMin = 0
  Detach1 = false
  Detach2 = false
  Distance = 0
  Distance2 = 0
  EnableAngleMax = false
  EnableAngleMin = false
  EnableLengthMax = false
  EnableLengthMin = false
  JointType = 0 (Fixed)
  LengthMax = 0
  LengthMin = 0
  Offset2 = pos=(0,0,0) rot=(0,0,1;1.5708rad)
  Placement1 = pos=(115,12,-85) rot=(0.57735,0.57735,0.57735;4.18879rad)
  Placement2 = pos=(-85,-4,-3.99) rot=(1,0,0;4.71239rad)
  Reference1 = -> Assembly [Glass_third.Face5,Glass_third.Vertex5]
  Reference2 = -> Assembly [Glazing_bead_third.Face9,Glazing_bead_third.Vertex9]
FEATURE [App::FeaturePython] Fixed003  # Assembly joint (typed FeaturePython)
  Activated = true
  AngleMax = 0
  AngleMin = 0
  Detach1 = false
  Detach2 = false
  Distance = 0
  Distance2 = 0
  EnableAngleMax = false
  EnableAngleMin = false
  EnableLengthMax = false
  EnableLengthMin = false
  JointType = 0 (Fixed)
  LengthMax = 0
  LengthMin = 0
  Offset2 = pos=(0,0,0) rot=(0,0,-1;1.5708rad)
  Placement1 = pos=(-115,12,-85) rot=(0.57735,0.57735,0.57735;4.18879rad)
  Placement2 = pos=(85,-4,-3.99) rot=(0,-0.707107,-0.707107;3.14159rad)
  Reference1 = -> Assembly [Glass_third.Face5,Glass_third.Vertex3]
  Reference2 = -> Assembly [Glazing_bead_third001.Face9,Glazing_bead_third001.Vertex7]
FEATURE [Assembly::JointGroup] Joints
  Group = -> [GroundedJoint,Fixed,Fixed001,Fixed002,Fixed003]
FEATURE [Assembly::AssemblyObject] Assembly  label="Glass third assembly"
  Group = -> [Joints,Glass_third,GroundedJoint,Glazing_bead_half,Glazing_bead_half001,Glazing_bead_third,Glazing_bead_third001,Fixed,Fixed001,Fixed002,Fixed003]
  Origin = -> Origin003
  Type = Assembly
---- part F4.2.FCStd = doc fcstd_5b2d5f329509 ----
FCSTD DOCUMENT  (FreeCAD 1.1R38844 (Git))
Label: F4.2
License: All rights reserved
LicenseURL: https://en.wikipedia.org/wiki/All_rights_reserved
objects: App::Link×5, App::FeaturePython×5, Sketcher::SketchObject×2, PartDesign::Pad×2, PartDesign::Body×2, App::VarSet×1, PartDesign::Chamfer×1, PartDesign::Fillet×1, App::DocumentObjectGroup×1, Assembly::JointGroup×1, Assembly::AssemblyObject×1
note: 18 computed .brp shape members not serialized (recipe doc carries the construction recipe); baked Part::Feature solids carry a one-line shape summary decoded from their .brp

FEATURE [Sketcher::SketchObject] Sketch
  ArcFitTolerance = 0
  AttachmentSupport = -> [XZ_Plane]
  FullyConstrained = true
  MakeInternals = false
  MapMode = 5
  Placement = pos=(0,0,0) rot=(1,0,0;1.5708rad)
  expr: Constraints[10] = <<Parameters>>.GlassLength
  expr: Constraints[11] = <<Parameters>>.GlassWidth
  sketch-geometry (5):
    g0: LineSegment StartX=-235 StartY=235 StartZ=0 EndX=-235 EndY=-235 EndZ=0
    g1: LineSegment StartX=-235 StartY=-235 StartZ=0 EndX=235 EndY=-235 EndZ=0
    g2: LineSegment StartX=235 StartY=-235 StartZ=0 EndX=235 EndY=235 EndZ=0
    g3: LineSegment StartX=235 StartY=235 StartZ=0 EndX=-235 EndY=235 EndZ=0
    g4: GeomPoint [constr] X=0 Y=0 Z=0
  constraints (12):
    c: Coincident(g0,g1)
    c: Coincident(g1,g2)
    c: Coincident(g2,g3)
    c: Coincident(g3,g0)
    c: Vertical(g0)
    c: Vertical(g2)
    c: Horizontal(g1)
    c: Horizontal(g3)
    c: Symmetric(g2,g0,g4)
    c: Coincident(g4,g-1)
    c: DistanceX(g3,g3) = 470
    c: DistanceY(g2,g2) = 470
FEATURE [Sketcher::SketchObject] Sketch001
  ArcFitTolerance = 0
  AttachmentSupport = -> [XZ_Plane001]
  FullyConstrained = true
  MakeInternals = false
  MapMode = 5
  Placement = pos=(0,0,0) rot=(1,0,0;1.5708rad)
  expr: Constraints[10] = <<Parameters>>.GlazingBeadFullLength
  expr: Constraints[11] = <<Parameters>>.GlazingBeadWidth
  sketch-geometry (5):
    g0: LineSegment StartX=-235 StartY=-4 StartZ=0 EndX=235 EndY=-4 EndZ=0
    g1: LineSegment StartX=235 StartY=-4 StartZ=0 EndX=235 EndY=4 EndZ=0
    g2: LineSegment StartX=235 StartY=4 StartZ=0 EndX=-235 EndY=4 EndZ=0
    g3: LineSegment StartX=-235 StartY=4 StartZ=0 EndX=-235 EndY=-4 EndZ=0
    g4: GeomPoint [constr] X=0 Y=0 Z=0
  constraints (12):
    c: Coincident(g0,g1)
    c: Coincident(g1,g2)
    c: Coincident(g2,g3)
    c: Coincident(g3,g0)
    c: Horizontal(g0)
    c: Horizontal(g2)
    c: Vertical(g1)
    c: Vertical(g3)
    c: Symmetric(g2,g0,g4)
    c: Coincident(g4,g-1)
    c: DistanceX(g2,g2) = 470
    c: DistanceY(g3,g3) = 8
FEATURE [App::VarSet] VarSet  label="Parameters"
  GlassLength = 470
  GlassThickness = 24
  GlassWidth = 470
  GlazingBeadFullLength = 470
  GlazingBeadFullWidth = 470
  GlazingBeadThickness = 8
  GlazingBeadWidth = 8
  expr: GlazingBeadFullLength = GlassLength
  expr: GlazingBeadFullWidth = GlassWidth
FEATURE [PartDesign::Pad] Pad
  Direction = (0,-1,2e-16)
  Length = 24
  Length2 = 10
  Midplane = true
  Placement = pos=(0,0,0) rot=(1,0,0;1.5708rad)
  Profile = -> Sketch
  ReferenceAxis = -> Sketch [N_Axis]
  Refine = true
  Suppressed = false
  Type = 0
  expr: Length = <<Parameters>>.GlassThickness
FEATURE [PartDesign::Body] Body  label="Glass full"
  AllowCompound = false
  Group = -> [Sketch,Pad]
  Length = 230
  Origin = -> Origin
  Thickness = 24
  Tip = -> Pad
  Width = 170
FEATURE [PartDesign::Pad] Pad001  label="Stock"
  Direction = (0,-1,2e-16)
  Length = 8
  Length2 = 10
  Midplane = true
  Placement = pos=(0,0,0) rot=(1,0,0;1.5708rad)
  Profile = -> Sketch001
  ReferenceAxis = -> Sketch001 [N_Axis]
  Refine = true
  Suppressed = false
  Type = 0
  expr: Length = <<Parameters>>.GlazingBeadThickness
FEATURE [PartDesign::Chamfer] Chamfer
  Angle = 45
  Base = -> Pad001 [Edge5,Edge8]
  BaseFeature = -> Pad001
  ChamferType = 0
  FlipDirection = false
  Placement = pos=(0,0,0) rot=(1,0,0;1.5708rad)
  Refine = true
  Size = 7.99
  Size2 = 1
  SupportTransform = false
  Suppressed = false
  UseAllEdges = false
  expr: Size = <<Parameters>>.GlazingBeadWidth - 0.01 mm
FEATURE [PartDesign::Fillet] Fillet
  Base = -> Chamfer [Edge7]
  BaseFeature = -> Chamfer
  Placement = pos=(0,0,0) rot=(1,0,0;1.5708rad)
  Radius = 7.99
  Refine = true
  SupportTransform = false
  Suppressed = false
  UseAllEdges = false
  expr: Radius = <<Parameters>>.GlazingBeadThickness - 0.01 mm
FEATURE [PartDesign::Body] Body001  label="Glazing bead full"
  AllowCompound = false
  Group = -> [Sketch001,Pad001,Chamfer,Fillet]
  Length = 230
  Origin = -> Origin001
  Thickness = 8
  Tip = -> Fillet
  Width = 8
FEATURE [App::Link] Glass_third  label="Glass full001"
  LinkPlacement = pos=(-35.9039,-54.1996,47.6343) rot=(0,0,1;0rad)
  LinkedObject = -> Body
  Placement = pos=(-35.9039,-54.1996,47.6343) rot=(0,0,1;0rad)
FEATURE [App::DocumentObjectGroup] Group  label="Components"
  Group = -> [Body,Body001]
FEATURE [App::FeaturePython] GroundedJoint  # Assembly grounded joint (typed FeaturePython)
  ObjectToGround = -> Glass_third
  Placement = pos=(-35.9039,-54.1996,47.6343) rot=(0,0,1;0rad)
FEATURE [App::Link] Glazing_bead_full  label="Glazing bead full001"
  LinkPlacement = pos=(-35.9039,-38.1996,-183.366) rot=(0,0,1;0rad)
  LinkedObject = -> Body001
  Placement = pos=(-35.9039,-38.1996,-183.366) rot=(0,0,1;0rad)
FEATURE [App::Link] Glazing_bead_full001  label="Glazing bead full002"
  LinkPlacement = pos=(-35.9039,-38.1996,278.634) rot=(0,1,0;3.14159rad)
  LinkedObject = -> Body001
  Placement = pos=(-35.9039,-38.1996,278.634) rot=(0,1,0;3.14159rad)
FEATURE [App::Link] Glazing_bead_full002  label="Glazing bead full003"
  LinkPlacement = pos=(-266.914,-38.1996,47.6343) rot=(0,1,0;1.5708rad)
  LinkedObject = -> Body001
  Placement = pos=(-266.914,-38.1996,47.6343) rot=(0,1,0;1.5708rad)
FEATURE [App::Link] Glazing_bead_full003  label="Glazing bead full004"
  LinkPlacement = pos=(195.106,-38.1996,47.6343) rot=(0,-1,0;1.5708rad)
  LinkedObject = -> Body001
  Placement = pos=(195.106,-38.1996,47.6343) rot=(0,-1,0;1.5708rad)
FEATURE [App::FeaturePython] Fixed  # Assembly joint (typed FeaturePython)
  Activated = true
  AngleMax = 0
  AngleMin = 0
  Detach1 = false
  Detach2 = false
  Distance = 0
  Distance2 = 0
  EnableAngleMax = false
  EnableAngleMin = false
  EnableLengthMax = false
  EnableLengthMin = false
  JointType = 0 (Fixed)
  LengthMax = 0
  LengthMin = 0
  Placement1 = pos=(-235,-4,-4) rot=(0,0,1;0rad)
  Placement2 = pos=(-235,12,-235) rot=(0,0,1;0rad)
  Reference1 = -> Assembly [Glazing_bead_full.Fillet.Vertex10,Glazing_bead_full.Fillet.Vertex10]
  Reference2 = -> Assembly [Glass_third.Pad.Vertex3,Glass_third.Pad.Vertex3]
FEATURE [App::FeaturePython] Fixed001  # Assembly joint (typed FeaturePython)
  Activated = true
  AngleMax = 0
  AngleMin = 0
  Detach1 = false
  Detach2 = false
  Distance = 0
  Distance2 = 0
  EnableAngleMax = false
  EnableAngleMin = false
  EnableLengthMax = false
  EnableLengthMin = false
  JointType = 0 (Fixed)
  LengthMax = 0
  LengthMin = 0
  Offset2 = pos=(0,0,0) rot=(0,0,1;3.14159rad)
  Placement1 = pos=(235,12,235) rot=(0,0,1;0rad)
  Placement2 = pos=(-235,-4,-4) rot=(0,0,1;3.14159rad)
  Reference1 = -> Assembly [Glass_third.Pad.Vertex7,Glass_third.Pad.Vertex7]
  Reference2 = -> Assembly [Glazing_bead_full001.Fillet.Vertex10,Glazing_bead_full001.Fillet.Vertex10]
FEATURE [App::FeaturePython] Fixed002  # Assembly joint (typed FeaturePython)
  Activated = true
  AngleMax = 0
  AngleMin = 0
  Detach1 = false
  Detach2 = false
  Distance = 0
  Distance2 = 0
  EnableAngleMax = false
  EnableAngleMin = false
  EnableLengthMax = false
  EnableLengthMin = false
  JointType = 0 (Fixed)
  LengthMax = 0
  LengthMin = 0
  Offset2 = pos=(0,0,0) rot=(0,0,-1;1.5708rad)
  Placement1 = pos=(-235,12,235) rot=(0.57735,0.57735,0.57735;4.18879rad)
  Placement2 = pos=(-235,-4,-3.99) rot=(0,-0.707107,-0.707107;3.14159rad)
  Reference1 = -> Assembly [Glass_third.Pad.Face5,Glass_third.Pad.Vertex1]
  Reference2 = -> Assembly [Glazing_bead_full002.Fillet.Face9,Glazing_bead_full002.Fillet.Vertex9]
FEATURE [App::FeaturePython] Fixed003  # Assembly joint (typed FeaturePython)
  Activated = true
  AngleMax = 0
  AngleMin = 0
  Detach1 = false
  Detach2 = false
  Distance = 0
  Distance2 = 0
  EnableAngleMax = false
  EnableAngleMin = false
  EnableLengthMax = false
  EnableLengthMin = false
  JointType = 0 (Fixed)
  LengthMax = 0
  LengthMin = 0
  Offset2 = pos=(0,0,0) rot=(0,0,1;1.5708rad)
  Placement1 = pos=(235,12,-235) rot=(0.57735,0.57735,0.57735;4.18879rad)
  Placement2 = pos=(-235,-4,-3.99) rot=(-1,0,0;1.5708rad)
  Reference1 = -> Assembly [Glass_third.Pad.Face5,Glass_third.Pad.Vertex5]
  Reference2 = -> Assembly [Glazing_bead_full003.Fillet.Face9,Glazing_bead_full003.Fillet.Vertex9]
FEATURE [Assembly::JointGroup] Joints
  Group = -> [GroundedJoint,Fixed,Fixed001,Fixed002,Fixed003]
FEATURE [Assembly::AssemblyObject] Assembly  label="Glass full assembly"
  Group = -> [Joints,Glass_third,GroundedJoint,Glazing_bead_full,Glazing_bead_full001,Glazing_bead_full002,Glazing_bead_full003,Fixed,Fixed001,Fixed002,Fixed003]
  Origin = -> Origin003
  Type = Assembly
